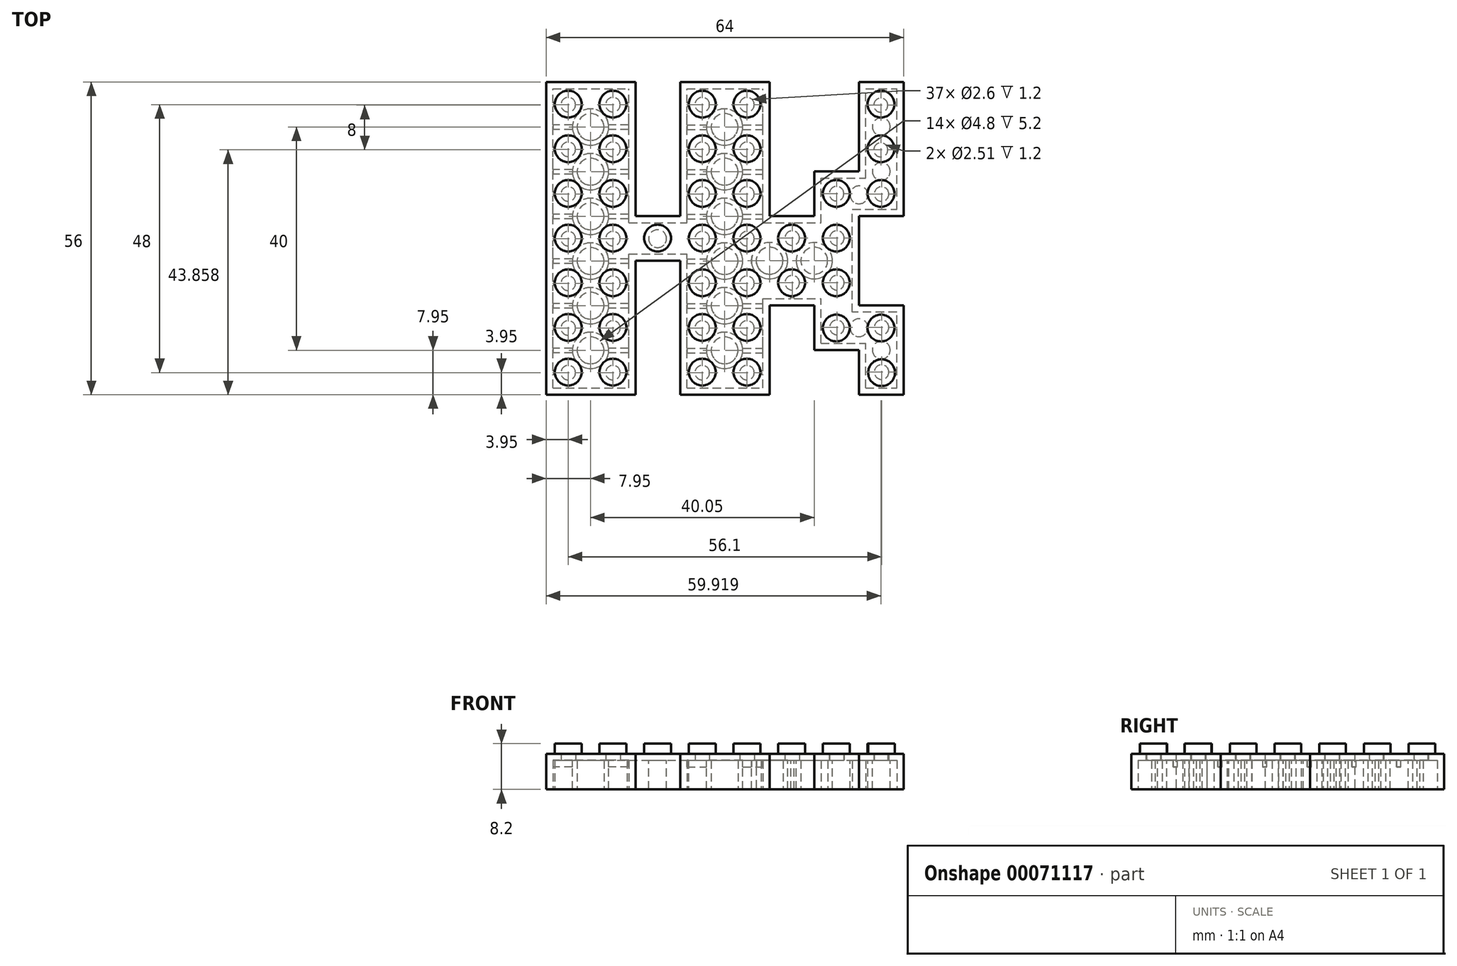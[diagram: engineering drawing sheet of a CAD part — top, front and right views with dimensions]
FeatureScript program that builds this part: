
annotation { "Feature Type Name" : "Feature", "Feature Type Description" : "" }
export const myFeature = defineFeature(function(context is Context, id is Id, definition is map)
    precondition{}
    {
        {
            var Q0;
            Q0=qCreatedBy(makeId("Top.planeOp"),FACE);
            var sketch = newSketch(context, id + "F0", { "sketchPlane" : qUnion([Q0])});
            skLineSegment(sketch, "E0.rect.bottom", {"start": v(20, 28) * mm, "end": v(-20, 28) * mm});
            skLineSegment(sketch, "E0.rect.top", {"start": v(20, -28) * mm, "end": v(-20, -28) * mm});
            skLineSegment(sketch, "E0.rect.left", {"start": v(20, 28) * mm, "end": v(20, -28) * mm});
            skLineSegment(sketch, "E0.rect.right", {"start": v(-20, 28) * mm, "end": v(-20, -28) * mm});
            skPoint(sketch, "E0.rect.middle", {"position": v(0, 0) * mm});
            skSolve(sketch);
        }
        {
            var Q0;
            Q0=makeQuery(id+"F0.imprint","IMPRINT",FACE,{"disambiguationData":[TD([[makeQuery(id+"F0.imprint","IMPRINT",EDGE,{"derivedFrom":sQuery(id+"F0.wireOp",EDGE,"E0.rect.bottom")}),1.0]])]});
            extrude(context, id + "F1", {"entities" : qUnion([Q0]), "depth" : 6.4 * mm});
        }
        {
            var Q0;
            Q0=makeQuery(id+"F1.opExtrude","CAP_FACE",FACE,{"disambiguationData":[OSD([sQuery(id+"F0.wireOp",EDGE,"E0.rect.bottom"),sQuery(id+"F0.wireOp",EDGE,"E0.rect.top"),sQuery(id+"F0.wireOp",EDGE,"E0.rect.left"),sQuery(id+"F0.wireOp",EDGE,"E0.rect.right")])],"isStart":false});
            var sketch = newSketch(context, id + "F2", { "sketchPlane" : qUnion([Q0])});
            skLineSegment(sketch, "E1.bottom", {"start": v(4, 4) * mm, "end": v(-4, 4) * mm});
            skLineSegment(sketch, "E1.top", {"start": v(4, 28) * mm, "end": v(-4, 28) * mm});
            skLineSegment(sketch, "E1.left", {"start": v(4, 4) * mm, "end": v(4, 28) * mm});
            skLineSegment(sketch, "E1.right", {"start": v(-4, 4) * mm, "end": v(-4, 28) * mm});
            skSolve(sketch);
        }
        {
            var Q0;
            Q0=makeQuery(id+"F2.imprint","IMPRINT",FACE,{"disambiguationData":[TD([[makeQuery(id+"F2.imprint","IMPRINT",EDGE,{"derivedFrom":sQuery(id+"F2.wireOp",EDGE,"E1.bottom")}),-1.0]])]});
            extrude(context, id + "F3", {"entities" : qUnion([Q0]), "operationType" : NewBodyOperationType.REMOVE, "oppositeDirection" : true, "depth" : 9.6 * mm});
        }
        {
            var Q0;
            Q0=makeQuery(id+"F1.opExtrude","CAP_FACE",FACE,{"disambiguationData":[OSD([sQuery(id+"F0.wireOp",EDGE,"E0.rect.bottom"),sQuery(id+"F0.wireOp",EDGE,"E0.rect.top"),sQuery(id+"F0.wireOp",EDGE,"E0.rect.left"),sQuery(id+"F0.wireOp",EDGE,"E0.rect.right")])],"isStart":false});
            var sketch = newSketch(context, id + "F4", { "sketchPlane" : qUnion([Q0])});
            skLineSegment(sketch, "E2.bottom", {"start": v(4, -28) * mm, "end": v(-4, -28) * mm});
            skLineSegment(sketch, "E2.top", {"start": v(4, -4) * mm, "end": v(-4, -4) * mm});
            skLineSegment(sketch, "E2.left", {"start": v(4, -28) * mm, "end": v(4, -4) * mm});
            skLineSegment(sketch, "E2.right", {"start": v(-4, -28) * mm, "end": v(-4, -4) * mm});
            skSolve(sketch);
        }
        {
            var Q0;
            Q0=makeQuery(id+"F4.imprint","IMPRINT",FACE,{"disambiguationData":[TD([[makeQuery(id+"F4.imprint","IMPRINT",EDGE,{"derivedFrom":sQuery(id+"F4.wireOp",EDGE,"E2.bottom")}),-1.0]])]});
            extrude(context, id + "F5", {"entities" : qUnion([Q0]), "operationType" : NewBodyOperationType.REMOVE, "oppositeDirection" : true, "depth" : 9.6 * mm});
        }
        {
            var Q0;
            Q0=qCreatedBy(makeId("Top.planeOp"),FACE);
            var sketch = newSketch(context, id + "F6", { "sketchPlane" : qUnion([Q0])});
            skLineSegment(sketch, "E3.bottom", {"start": v(20, 4) * mm, "end": v(36, 4) * mm});
            skLineSegment(sketch, "E3.top", {"start": v(20, -12) * mm, "end": v(36, -12) * mm});
            skLineSegment(sketch, "E3.left", {"start": v(20, 4) * mm, "end": v(20, -12) * mm});
            skLineSegment(sketch, "E3.right", {"start": v(36, 4) * mm, "end": v(36, -12) * mm});
            skSolve(sketch);
        }
        {
            var Q0;
            Q0=makeQuery(id+"F6.imprint","IMPRINT",FACE,{"disambiguationData":[TD([[makeQuery(id+"F6.imprint","IMPRINT",EDGE,{"derivedFrom":sQuery(id+"F6.wireOp",EDGE,"E3.bottom")}),-1.0]])]});
            extrude(context, id + "F7", {"entities" : qUnion([Q0]), "operationType" : NewBodyOperationType.ADD, "depth" : 6.4 * mm});
        }
        {
            var Q0;
            Q0=makeQuery(id+"Fq8iTaXQzpA7FPV_1.boolean.opBoolean","MERGE",FACE,{"derivedFrom":[makeQuery(id+"FeKJCFrg74xluvg_1.boolean.opBoolean","MERGE",FACE,{"derivedFrom":[makeQuery(id+"FFEIV1BnWD0H84f_1.boolean.opBoolean","MERGE",FACE,{"derivedFrom":[makeQuery(id+"F2oVHyxGzkOQPI6_1.boolean.opBoolean","MERGE",FACE,{"derivedFrom":[makeQuery(id+"F7.boolean.opBoolean","MERGE",FACE,{"derivedFrom":[makeQuery(id+"F1.opExtrude","CAP_FACE",FACE,{"disambiguationData":[OSD([sQuery(id+"F0.wireOp",EDGE,"E0.rect.bottom"),sQuery(id+"F0.wireOp",EDGE,"E0.rect.top"),sQuery(id+"F0.wireOp",EDGE,"E0.rect.left"),sQuery(id+"F0.wireOp",EDGE,"E0.rect.right")])],"isStart":true}),makeQuery(id+"F7.opExtrude","CAP_FACE",FACE,{"disambiguationData":[OSD([sQuery(id+"F6.wireOp",EDGE,"E3.bottom"),sQuery(id+"F6.wireOp",EDGE,"E3.top"),sQuery(id+"F6.wireOp",EDGE,"E3.left"),sQuery(id+"F6.wireOp",EDGE,"E3.right")])],"isStart":true})]}),makeQuery(id+"F2oVHyxGzkOQPI6_1.opExtrude","CAP_FACE",FACE,{"disambiguationData":[OSD([sQuery(id+"Fx6wsB5A8MVDIGl_1.wireOp",EDGE,"2b883c94-4758-4cd2-bf81-8503723d2fbf.bottom"),sQuery(id+"Fx6wsB5A8MVDIGl_1.wireOp",EDGE,"2b883c94-4758-4cd2-bf81-8503723d2fbf.top"),sQuery(id+"Fx6wsB5A8MVDIGl_1.wireOp",EDGE,"2b883c94-4758-4cd2-bf81-8503723d2fbf.left"),sQuery(id+"Fx6wsB5A8MVDIGl_1.wireOp",EDGE,"2b883c94-4758-4cd2-bf81-8503723d2fbf.right")])],"isStart":true})]}),makeQuery(id+"FFEIV1BnWD0H84f_1.opExtrude","CAP_FACE",FACE,{"disambiguationData":[OSD([sQuery(id+"Fq5423x5i0oBvdk_1.wireOp",EDGE,"50359f41-1c30-4885-bf29-1e37fb7fc2df.bottom"),sQuery(id+"Fq5423x5i0oBvdk_1.wireOp",EDGE,"50359f41-1c30-4885-bf29-1e37fb7fc2df.top"),sQuery(id+"Fq5423x5i0oBvdk_1.wireOp",EDGE,"50359f41-1c30-4885-bf29-1e37fb7fc2df.left"),sQuery(id+"Fq5423x5i0oBvdk_1.wireOp",EDGE,"50359f41-1c30-4885-bf29-1e37fb7fc2df.right")])],"isStart":true})]}),makeQuery(id+"FeKJCFrg74xluvg_1.opExtrude","CAP_FACE",FACE,{"disambiguationData":[OSD([sQuery(id+"FwcK1e5tJnhP9xu_1.wireOp",EDGE,"d4659890-7073-4dbc-80d8-35276d7f4160.bottom"),sQuery(id+"FwcK1e5tJnhP9xu_1.wireOp",EDGE,"d4659890-7073-4dbc-80d8-35276d7f4160.top"),sQuery(id+"FwcK1e5tJnhP9xu_1.wireOp",EDGE,"d4659890-7073-4dbc-80d8-35276d7f4160.left"),sQuery(id+"FwcK1e5tJnhP9xu_1.wireOp",EDGE,"d4659890-7073-4dbc-80d8-35276d7f4160.right")])],"isStart":true})]}),makeQuery(id+"Fq8iTaXQzpA7FPV_1.opExtrude","CAP_FACE",FACE,{"disambiguationData":[OSD([sQuery(id+"F0iV27WPdkTHYam_1.wireOp",EDGE,"b5bfac4e-3525-4930-abdc-5fcdb06bce00.bottom"),sQuery(id+"F0iV27WPdkTHYam_1.wireOp",EDGE,"b5bfac4e-3525-4930-abdc-5fcdb06bce00.top"),sQuery(id+"F0iV27WPdkTHYam_1.wireOp",EDGE,"b5bfac4e-3525-4930-abdc-5fcdb06bce00.left"),sQuery(id+"F0iV27WPdkTHYam_1.wireOp",EDGE,"b5bfac4e-3525-4930-abdc-5fcdb06bce00.right")])],"isStart":true})]});
            var sketch = newSketch(context, id + "F8", { "sketchPlane" : qUnion([Q0])});
            skLineSegment(sketch, "E4.bottom", {"start": v(-18.8, 26.8) * mm, "end": v(-5.2, 26.8) * mm});
            skLineSegment(sketch, "E4.top", {"start": v(-18.8, -26.8) * mm, "end": v(-5.2, -26.8) * mm});
            skLineSegment(sketch, "E4.left", {"start": v(-18.8, 26.8) * mm, "end": v(-18.8, -26.8) * mm});
            skLineSegment(sketch, "E4.right", {"start": v(-5.2, 26.8) * mm, "end": v(-5.2, -26.8) * mm});
            skSolve(sketch);
        }
        {
            var Q0;
            Q0=makeQuery(id+"F8.imprint","IMPRINT",FACE,{"disambiguationData":[TD([[makeQuery(id+"F8.imprint","IMPRINT",EDGE,{"derivedFrom":sQuery(id+"F8.wireOp",EDGE,"E4.bottom")}),-1.0]])]});
            extrude(context, id + "F9", {"entities" : qUnion([Q0]), "operationType" : NewBodyOperationType.REMOVE, "oppositeDirection" : true, "depth" : 5.2 * mm});
        }
        {
            var Q0;
            Q0=makeQuery(id+"Fq8iTaXQzpA7FPV_1.boolean.opBoolean","MERGE",FACE,{"derivedFrom":[makeQuery(id+"FeKJCFrg74xluvg_1.boolean.opBoolean","MERGE",FACE,{"derivedFrom":[makeQuery(id+"FFEIV1BnWD0H84f_1.boolean.opBoolean","MERGE",FACE,{"derivedFrom":[makeQuery(id+"F2oVHyxGzkOQPI6_1.boolean.opBoolean","MERGE",FACE,{"derivedFrom":[makeQuery(id+"F7.boolean.opBoolean","MERGE",FACE,{"derivedFrom":[makeQuery(id+"F1.opExtrude","CAP_FACE",FACE,{"disambiguationData":[OSD([sQuery(id+"F0.wireOp",EDGE,"E0.rect.bottom"),sQuery(id+"F0.wireOp",EDGE,"E0.rect.top"),sQuery(id+"F0.wireOp",EDGE,"E0.rect.left"),sQuery(id+"F0.wireOp",EDGE,"E0.rect.right")])],"isStart":true}),makeQuery(id+"F7.opExtrude","CAP_FACE",FACE,{"disambiguationData":[OSD([sQuery(id+"F6.wireOp",EDGE,"E3.bottom"),sQuery(id+"F6.wireOp",EDGE,"E3.top"),sQuery(id+"F6.wireOp",EDGE,"E3.left"),sQuery(id+"F6.wireOp",EDGE,"E3.right")])],"isStart":true})]}),makeQuery(id+"F2oVHyxGzkOQPI6_1.opExtrude","CAP_FACE",FACE,{"disambiguationData":[OSD([sQuery(id+"Fx6wsB5A8MVDIGl_1.wireOp",EDGE,"2b883c94-4758-4cd2-bf81-8503723d2fbf.bottom"),sQuery(id+"Fx6wsB5A8MVDIGl_1.wireOp",EDGE,"2b883c94-4758-4cd2-bf81-8503723d2fbf.top"),sQuery(id+"Fx6wsB5A8MVDIGl_1.wireOp",EDGE,"2b883c94-4758-4cd2-bf81-8503723d2fbf.left"),sQuery(id+"Fx6wsB5A8MVDIGl_1.wireOp",EDGE,"2b883c94-4758-4cd2-bf81-8503723d2fbf.right")])],"isStart":true})]}),makeQuery(id+"FFEIV1BnWD0H84f_1.opExtrude","CAP_FACE",FACE,{"disambiguationData":[OSD([sQuery(id+"Fq5423x5i0oBvdk_1.wireOp",EDGE,"50359f41-1c30-4885-bf29-1e37fb7fc2df.bottom"),sQuery(id+"Fq5423x5i0oBvdk_1.wireOp",EDGE,"50359f41-1c30-4885-bf29-1e37fb7fc2df.top"),sQuery(id+"Fq5423x5i0oBvdk_1.wireOp",EDGE,"50359f41-1c30-4885-bf29-1e37fb7fc2df.left"),sQuery(id+"Fq5423x5i0oBvdk_1.wireOp",EDGE,"50359f41-1c30-4885-bf29-1e37fb7fc2df.right")])],"isStart":true})]}),makeQuery(id+"FeKJCFrg74xluvg_1.opExtrude","CAP_FACE",FACE,{"disambiguationData":[OSD([sQuery(id+"FwcK1e5tJnhP9xu_1.wireOp",EDGE,"d4659890-7073-4dbc-80d8-35276d7f4160.bottom"),sQuery(id+"FwcK1e5tJnhP9xu_1.wireOp",EDGE,"d4659890-7073-4dbc-80d8-35276d7f4160.top"),sQuery(id+"FwcK1e5tJnhP9xu_1.wireOp",EDGE,"d4659890-7073-4dbc-80d8-35276d7f4160.left"),sQuery(id+"FwcK1e5tJnhP9xu_1.wireOp",EDGE,"d4659890-7073-4dbc-80d8-35276d7f4160.right")])],"isStart":true})]}),makeQuery(id+"Fq8iTaXQzpA7FPV_1.opExtrude","CAP_FACE",FACE,{"disambiguationData":[OSD([sQuery(id+"F0iV27WPdkTHYam_1.wireOp",EDGE,"b5bfac4e-3525-4930-abdc-5fcdb06bce00.bottom"),sQuery(id+"F0iV27WPdkTHYam_1.wireOp",EDGE,"b5bfac4e-3525-4930-abdc-5fcdb06bce00.top"),sQuery(id+"F0iV27WPdkTHYam_1.wireOp",EDGE,"b5bfac4e-3525-4930-abdc-5fcdb06bce00.left"),sQuery(id+"F0iV27WPdkTHYam_1.wireOp",EDGE,"b5bfac4e-3525-4930-abdc-5fcdb06bce00.right")])],"isStart":true})]});
            var sketch = newSketch(context, id + "F10", { "sketchPlane" : qUnion([Q0])});
            skLineSegment(sketch, "E5.bottom", {"start": v(-5.2, 2.8) * mm, "end": v(5.2, 2.8) * mm});
            skLineSegment(sketch, "E5.top", {"start": v(-5.2, -2.8) * mm, "end": v(5.2, -2.8) * mm});
            skLineSegment(sketch, "E5.left", {"start": v(-5.2, 2.8) * mm, "end": v(-5.2, -2.8) * mm});
            skLineSegment(sketch, "E5.right", {"start": v(5.2, 2.8) * mm, "end": v(5.2, -2.8) * mm});
            skSolve(sketch);
        }
        {
            var Q0;
            Q0=makeQuery(id+"F10.imprint","IMPRINT",FACE,{"disambiguationData":[TD([[makeQuery(id+"F10.imprint","IMPRINT",EDGE,{"derivedFrom":sQuery(id+"F10.wireOp",EDGE,"E5.bottom")}),-1.0]])]});
            extrude(context, id + "F11", {"entities" : qUnion([Q0]), "operationType" : NewBodyOperationType.REMOVE, "oppositeDirection" : true, "depth" : 5.2 * mm});
        }
        {
            var Q0;
            Q0=makeQuery(id+"Fq8iTaXQzpA7FPV_1.boolean.opBoolean","MERGE",FACE,{"derivedFrom":[makeQuery(id+"FeKJCFrg74xluvg_1.boolean.opBoolean","MERGE",FACE,{"derivedFrom":[makeQuery(id+"FFEIV1BnWD0H84f_1.boolean.opBoolean","MERGE",FACE,{"derivedFrom":[makeQuery(id+"F2oVHyxGzkOQPI6_1.boolean.opBoolean","MERGE",FACE,{"derivedFrom":[makeQuery(id+"F7.boolean.opBoolean","MERGE",FACE,{"derivedFrom":[makeQuery(id+"F1.opExtrude","CAP_FACE",FACE,{"disambiguationData":[OSD([sQuery(id+"F0.wireOp",EDGE,"E0.rect.bottom"),sQuery(id+"F0.wireOp",EDGE,"E0.rect.top"),sQuery(id+"F0.wireOp",EDGE,"E0.rect.left"),sQuery(id+"F0.wireOp",EDGE,"E0.rect.right")])],"isStart":true}),makeQuery(id+"F7.opExtrude","CAP_FACE",FACE,{"disambiguationData":[OSD([sQuery(id+"F6.wireOp",EDGE,"E3.bottom"),sQuery(id+"F6.wireOp",EDGE,"E3.top"),sQuery(id+"F6.wireOp",EDGE,"E3.left"),sQuery(id+"F6.wireOp",EDGE,"E3.right")])],"isStart":true})]}),makeQuery(id+"F2oVHyxGzkOQPI6_1.opExtrude","CAP_FACE",FACE,{"disambiguationData":[OSD([sQuery(id+"Fx6wsB5A8MVDIGl_1.wireOp",EDGE,"2b883c94-4758-4cd2-bf81-8503723d2fbf.bottom"),sQuery(id+"Fx6wsB5A8MVDIGl_1.wireOp",EDGE,"2b883c94-4758-4cd2-bf81-8503723d2fbf.top"),sQuery(id+"Fx6wsB5A8MVDIGl_1.wireOp",EDGE,"2b883c94-4758-4cd2-bf81-8503723d2fbf.left"),sQuery(id+"Fx6wsB5A8MVDIGl_1.wireOp",EDGE,"2b883c94-4758-4cd2-bf81-8503723d2fbf.right")])],"isStart":true})]}),makeQuery(id+"FFEIV1BnWD0H84f_1.opExtrude","CAP_FACE",FACE,{"disambiguationData":[OSD([sQuery(id+"Fq5423x5i0oBvdk_1.wireOp",EDGE,"50359f41-1c30-4885-bf29-1e37fb7fc2df.bottom"),sQuery(id+"Fq5423x5i0oBvdk_1.wireOp",EDGE,"50359f41-1c30-4885-bf29-1e37fb7fc2df.top"),sQuery(id+"Fq5423x5i0oBvdk_1.wireOp",EDGE,"50359f41-1c30-4885-bf29-1e37fb7fc2df.left"),sQuery(id+"Fq5423x5i0oBvdk_1.wireOp",EDGE,"50359f41-1c30-4885-bf29-1e37fb7fc2df.right")])],"isStart":true})]}),makeQuery(id+"FeKJCFrg74xluvg_1.opExtrude","CAP_FACE",FACE,{"disambiguationData":[OSD([sQuery(id+"FwcK1e5tJnhP9xu_1.wireOp",EDGE,"d4659890-7073-4dbc-80d8-35276d7f4160.bottom"),sQuery(id+"FwcK1e5tJnhP9xu_1.wireOp",EDGE,"d4659890-7073-4dbc-80d8-35276d7f4160.top"),sQuery(id+"FwcK1e5tJnhP9xu_1.wireOp",EDGE,"d4659890-7073-4dbc-80d8-35276d7f4160.left"),sQuery(id+"FwcK1e5tJnhP9xu_1.wireOp",EDGE,"d4659890-7073-4dbc-80d8-35276d7f4160.right")])],"isStart":true})]}),makeQuery(id+"Fq8iTaXQzpA7FPV_1.opExtrude","CAP_FACE",FACE,{"disambiguationData":[OSD([sQuery(id+"F0iV27WPdkTHYam_1.wireOp",EDGE,"b5bfac4e-3525-4930-abdc-5fcdb06bce00.bottom"),sQuery(id+"F0iV27WPdkTHYam_1.wireOp",EDGE,"b5bfac4e-3525-4930-abdc-5fcdb06bce00.top"),sQuery(id+"F0iV27WPdkTHYam_1.wireOp",EDGE,"b5bfac4e-3525-4930-abdc-5fcdb06bce00.left"),sQuery(id+"F0iV27WPdkTHYam_1.wireOp",EDGE,"b5bfac4e-3525-4930-abdc-5fcdb06bce00.right")])],"isStart":true})]});
            var sketch = newSketch(context, id + "F12", { "sketchPlane" : qUnion([Q0])});
            skLineSegment(sketch, "E6.bottom", {"start": v(5.2, 26.8) * mm, "end": v(18.8, 26.8) * mm});
            skLineSegment(sketch, "E6.top", {"start": v(5.2, -26.8) * mm, "end": v(18.8, -26.8) * mm});
            skLineSegment(sketch, "E6.left", {"start": v(5.2, 26.8) * mm, "end": v(5.2, -26.8) * mm});
            skLineSegment(sketch, "E6.right", {"start": v(18.8, 26.8) * mm, "end": v(18.8, -26.8) * mm});
            skSolve(sketch);
        }
        {
            var Q0;
            {var subQ3=sQuery(id+"F12.wireOp",EDGE,"E6.bottom");Q0=makeQuery(id+"F12.imprint","IMPRINT",FACE,{"disambiguationData":[TD([[makeQuery(id+"F12.imprint","IMPRINT",EDGE,{"derivedFrom":subQ3}),-1.0]])]});}
            extrude(context, id + "F13", {"entities" : qUnion([Q0]), "operationType" : NewBodyOperationType.REMOVE, "oppositeDirection" : true, "depth" : 5.2 * mm});
        }
        {
            var Q0;
            Q0=makeQuery(id+"Fq8iTaXQzpA7FPV_1.boolean.opBoolean","MERGE",FACE,{"derivedFrom":[makeQuery(id+"FeKJCFrg74xluvg_1.boolean.opBoolean","MERGE",FACE,{"derivedFrom":[makeQuery(id+"FFEIV1BnWD0H84f_1.boolean.opBoolean","MERGE",FACE,{"derivedFrom":[makeQuery(id+"F2oVHyxGzkOQPI6_1.boolean.opBoolean","MERGE",FACE,{"derivedFrom":[makeQuery(id+"F7.boolean.opBoolean","MERGE",FACE,{"derivedFrom":[makeQuery(id+"F1.opExtrude","CAP_FACE",FACE,{"disambiguationData":[OSD([sQuery(id+"F0.wireOp",EDGE,"E0.rect.bottom"),sQuery(id+"F0.wireOp",EDGE,"E0.rect.top"),sQuery(id+"F0.wireOp",EDGE,"E0.rect.left"),sQuery(id+"F0.wireOp",EDGE,"E0.rect.right")])],"isStart":true}),makeQuery(id+"F7.opExtrude","CAP_FACE",FACE,{"disambiguationData":[OSD([sQuery(id+"F6.wireOp",EDGE,"E3.bottom"),sQuery(id+"F6.wireOp",EDGE,"E3.top"),sQuery(id+"F6.wireOp",EDGE,"E3.left"),sQuery(id+"F6.wireOp",EDGE,"E3.right")])],"isStart":true})]}),makeQuery(id+"F2oVHyxGzkOQPI6_1.opExtrude","CAP_FACE",FACE,{"disambiguationData":[OSD([sQuery(id+"Fx6wsB5A8MVDIGl_1.wireOp",EDGE,"2b883c94-4758-4cd2-bf81-8503723d2fbf.bottom"),sQuery(id+"Fx6wsB5A8MVDIGl_1.wireOp",EDGE,"2b883c94-4758-4cd2-bf81-8503723d2fbf.top"),sQuery(id+"Fx6wsB5A8MVDIGl_1.wireOp",EDGE,"2b883c94-4758-4cd2-bf81-8503723d2fbf.left"),sQuery(id+"Fx6wsB5A8MVDIGl_1.wireOp",EDGE,"2b883c94-4758-4cd2-bf81-8503723d2fbf.right")])],"isStart":true})]}),makeQuery(id+"FFEIV1BnWD0H84f_1.opExtrude","CAP_FACE",FACE,{"disambiguationData":[OSD([sQuery(id+"Fq5423x5i0oBvdk_1.wireOp",EDGE,"50359f41-1c30-4885-bf29-1e37fb7fc2df.bottom"),sQuery(id+"Fq5423x5i0oBvdk_1.wireOp",EDGE,"50359f41-1c30-4885-bf29-1e37fb7fc2df.top"),sQuery(id+"Fq5423x5i0oBvdk_1.wireOp",EDGE,"50359f41-1c30-4885-bf29-1e37fb7fc2df.left"),sQuery(id+"Fq5423x5i0oBvdk_1.wireOp",EDGE,"50359f41-1c30-4885-bf29-1e37fb7fc2df.right")])],"isStart":true})]}),makeQuery(id+"FeKJCFrg74xluvg_1.opExtrude","CAP_FACE",FACE,{"disambiguationData":[OSD([sQuery(id+"FwcK1e5tJnhP9xu_1.wireOp",EDGE,"d4659890-7073-4dbc-80d8-35276d7f4160.bottom"),sQuery(id+"FwcK1e5tJnhP9xu_1.wireOp",EDGE,"d4659890-7073-4dbc-80d8-35276d7f4160.top"),sQuery(id+"FwcK1e5tJnhP9xu_1.wireOp",EDGE,"d4659890-7073-4dbc-80d8-35276d7f4160.left"),sQuery(id+"FwcK1e5tJnhP9xu_1.wireOp",EDGE,"d4659890-7073-4dbc-80d8-35276d7f4160.right")])],"isStart":true})]}),makeQuery(id+"Fq8iTaXQzpA7FPV_1.opExtrude","CAP_FACE",FACE,{"disambiguationData":[OSD([sQuery(id+"F0iV27WPdkTHYam_1.wireOp",EDGE,"b5bfac4e-3525-4930-abdc-5fcdb06bce00.bottom"),sQuery(id+"F0iV27WPdkTHYam_1.wireOp",EDGE,"b5bfac4e-3525-4930-abdc-5fcdb06bce00.top"),sQuery(id+"F0iV27WPdkTHYam_1.wireOp",EDGE,"b5bfac4e-3525-4930-abdc-5fcdb06bce00.left"),sQuery(id+"F0iV27WPdkTHYam_1.wireOp",EDGE,"b5bfac4e-3525-4930-abdc-5fcdb06bce00.right")])],"isStart":true})]});
            var sketch = newSketch(context, id + "F14", { "sketchPlane" : qUnion([Q0])});
            skLineSegment(sketch, "E7.bottom", {"start": v(18.8, 10.8) * mm, "end": v(34.8, 10.8) * mm});
            skLineSegment(sketch, "E7.top", {"start": v(18.8, -2.8) * mm, "end": v(34.8, -2.8) * mm});
            skLineSegment(sketch, "E7.left", {"start": v(18.8, 10.8) * mm, "end": v(18.8, -2.8) * mm});
            skLineSegment(sketch, "E7.right", {"start": v(34.8, 10.8) * mm, "end": v(34.8, -2.8) * mm});
            skSolve(sketch);
        }
        {
            var Q0;
            Q0=makeQuery(id+"F14.imprint","IMPRINT",FACE,{"disambiguationData":[TD([[makeQuery(id+"F14.imprint","IMPRINT",EDGE,{"derivedFrom":sQuery(id+"F14.wireOp",EDGE,"E7.bottom")}),-1.0]])]});
            extrude(context, id + "F15", {"entities" : qUnion([Q0]), "operationType" : NewBodyOperationType.REMOVE, "oppositeDirection" : true, "depth" : 5.2 * mm});
        }
        {
            var Q0;
            Q0=makeQuery(id+"Fq8iTaXQzpA7FPV_1.boolean.opBoolean","MERGE",FACE,{"derivedFrom":[makeQuery(id+"FeKJCFrg74xluvg_1.boolean.opBoolean","MERGE",FACE,{"derivedFrom":[makeQuery(id+"FFEIV1BnWD0H84f_1.boolean.opBoolean","MERGE",FACE,{"derivedFrom":[makeQuery(id+"F2oVHyxGzkOQPI6_1.boolean.opBoolean","MERGE",FACE,{"derivedFrom":[makeQuery(id+"F7.boolean.opBoolean","MERGE",FACE,{"derivedFrom":[makeQuery(id+"F1.opExtrude","CAP_FACE",FACE,{"disambiguationData":[OSD([sQuery(id+"F0.wireOp",EDGE,"E0.rect.bottom"),sQuery(id+"F0.wireOp",EDGE,"E0.rect.top"),sQuery(id+"F0.wireOp",EDGE,"E0.rect.left"),sQuery(id+"F0.wireOp",EDGE,"E0.rect.right")])],"isStart":false}),makeQuery(id+"F7.opExtrude","CAP_FACE",FACE,{"disambiguationData":[OSD([sQuery(id+"F6.wireOp",EDGE,"E3.bottom"),sQuery(id+"F6.wireOp",EDGE,"E3.top"),sQuery(id+"F6.wireOp",EDGE,"E3.left"),sQuery(id+"F6.wireOp",EDGE,"E3.right")])],"isStart":false})]}),makeQuery(id+"F2oVHyxGzkOQPI6_1.opExtrude","CAP_FACE",FACE,{"disambiguationData":[OSD([sQuery(id+"Fx6wsB5A8MVDIGl_1.wireOp",EDGE,"2b883c94-4758-4cd2-bf81-8503723d2fbf.bottom"),sQuery(id+"Fx6wsB5A8MVDIGl_1.wireOp",EDGE,"2b883c94-4758-4cd2-bf81-8503723d2fbf.top"),sQuery(id+"Fx6wsB5A8MVDIGl_1.wireOp",EDGE,"2b883c94-4758-4cd2-bf81-8503723d2fbf.left"),sQuery(id+"Fx6wsB5A8MVDIGl_1.wireOp",EDGE,"2b883c94-4758-4cd2-bf81-8503723d2fbf.right")])],"isStart":false})]}),makeQuery(id+"FFEIV1BnWD0H84f_1.opExtrude","CAP_FACE",FACE,{"disambiguationData":[OSD([sQuery(id+"Fq5423x5i0oBvdk_1.wireOp",EDGE,"50359f41-1c30-4885-bf29-1e37fb7fc2df.bottom"),sQuery(id+"Fq5423x5i0oBvdk_1.wireOp",EDGE,"50359f41-1c30-4885-bf29-1e37fb7fc2df.top"),sQuery(id+"Fq5423x5i0oBvdk_1.wireOp",EDGE,"50359f41-1c30-4885-bf29-1e37fb7fc2df.left"),sQuery(id+"Fq5423x5i0oBvdk_1.wireOp",EDGE,"50359f41-1c30-4885-bf29-1e37fb7fc2df.right")])],"isStart":false})]}),makeQuery(id+"FeKJCFrg74xluvg_1.opExtrude","CAP_FACE",FACE,{"disambiguationData":[OSD([sQuery(id+"FwcK1e5tJnhP9xu_1.wireOp",EDGE,"d4659890-7073-4dbc-80d8-35276d7f4160.bottom"),sQuery(id+"FwcK1e5tJnhP9xu_1.wireOp",EDGE,"d4659890-7073-4dbc-80d8-35276d7f4160.top"),sQuery(id+"FwcK1e5tJnhP9xu_1.wireOp",EDGE,"d4659890-7073-4dbc-80d8-35276d7f4160.left"),sQuery(id+"FwcK1e5tJnhP9xu_1.wireOp",EDGE,"d4659890-7073-4dbc-80d8-35276d7f4160.right")])],"isStart":false})]}),makeQuery(id+"Fq8iTaXQzpA7FPV_1.opExtrude","CAP_FACE",FACE,{"disambiguationData":[OSD([sQuery(id+"F0iV27WPdkTHYam_1.wireOp",EDGE,"b5bfac4e-3525-4930-abdc-5fcdb06bce00.bottom"),sQuery(id+"F0iV27WPdkTHYam_1.wireOp",EDGE,"b5bfac4e-3525-4930-abdc-5fcdb06bce00.top"),sQuery(id+"F0iV27WPdkTHYam_1.wireOp",EDGE,"b5bfac4e-3525-4930-abdc-5fcdb06bce00.left"),sQuery(id+"F0iV27WPdkTHYam_1.wireOp",EDGE,"b5bfac4e-3525-4930-abdc-5fcdb06bce00.right")])],"isStart":false})]});
            var sketch = newSketch(context, id + "F16", { "sketchPlane" : qUnion([Q0])});
            skCircle(sketch, "E8", {"center": v(-16.05, 24.05) * mm, "radius": 2.4 * mm});
            skCircle(sketch, "E9.0.1.0", {"center": v(-16.05, 16.05) * mm, "radius": 2.4 * mm});
            skCircle(sketch, "E9.0.2.0", {"center": v(-16.05, 8.05) * mm, "radius": 2.4 * mm});
            skCircle(sketch, "E9.0.3.0", {"center": v(-16.05, 0.05) * mm, "radius": 2.4 * mm});
            skCircle(sketch, "E9.0.4.0", {"center": v(-16.05, -7.95) * mm, "radius": 2.4 * mm});
            skCircle(sketch, "E9.0.5.0", {"center": v(-16.05, -15.95) * mm, "radius": 2.4 * mm});
            skCircle(sketch, "E9.0.6.0", {"center": v(-16.05, -23.95) * mm, "radius": 2.4 * mm});
            skCircle(sketch, "E9.1.0.0", {"center": v(-8.05, 24.05) * mm, "radius": 2.4 * mm});
            skCircle(sketch, "E9.1.1.0", {"center": v(-8.05, 16.05) * mm, "radius": 2.4 * mm});
            skCircle(sketch, "E9.1.2.0", {"center": v(-8.05, 8.05) * mm, "radius": 2.4 * mm});
            skCircle(sketch, "E9.1.3.0", {"center": v(-8.05, 0.05) * mm, "radius": 2.4 * mm});
            skCircle(sketch, "E9.1.4.0", {"center": v(-8.05, -7.95) * mm, "radius": 2.4 * mm});
            skCircle(sketch, "E9.1.5.0", {"center": v(-8.05, -15.95) * mm, "radius": 2.4 * mm});
            skCircle(sketch, "E9.1.6.0", {"center": v(-8.05, -23.95) * mm, "radius": 2.4 * mm});
            skLineSegment(sketch, "E9.direction1", {"start": v(-16.05, 24.05) * mm, "end": v(-8.05, 24.05) * mm, "construction": true});
            skLineSegment(sketch, "E9.direction2", {"start": v(-16.05, 24.05) * mm, "end": v(-16.05, 16.05) * mm, "construction": true});
            skSolve(sketch);
        }
        {
            var Q0;
            Q0 = qSketchRegion(id + "F16", true);
            extrude(context, id + "F17", {"entities" : qUnion([Q0]), "operationType" : NewBodyOperationType.ADD, "depth" : 1.8 * mm});
        }
        {
            var Q0;
            Q0=makeQuery(id+"Fq8iTaXQzpA7FPV_1.boolean.opBoolean","MERGE",FACE,{"derivedFrom":[makeQuery(id+"FeKJCFrg74xluvg_1.boolean.opBoolean","MERGE",FACE,{"derivedFrom":[makeQuery(id+"FFEIV1BnWD0H84f_1.boolean.opBoolean","MERGE",FACE,{"derivedFrom":[makeQuery(id+"F2oVHyxGzkOQPI6_1.boolean.opBoolean","MERGE",FACE,{"derivedFrom":[makeQuery(id+"F7.boolean.opBoolean","MERGE",FACE,{"derivedFrom":[makeQuery(id+"F1.opExtrude","CAP_FACE",FACE,{"disambiguationData":[OSD([sQuery(id+"F0.wireOp",EDGE,"E0.rect.bottom"),sQuery(id+"F0.wireOp",EDGE,"E0.rect.top"),sQuery(id+"F0.wireOp",EDGE,"E0.rect.left"),sQuery(id+"F0.wireOp",EDGE,"E0.rect.right")])],"isStart":false}),makeQuery(id+"F7.opExtrude","CAP_FACE",FACE,{"disambiguationData":[OSD([sQuery(id+"F6.wireOp",EDGE,"E3.bottom"),sQuery(id+"F6.wireOp",EDGE,"E3.top"),sQuery(id+"F6.wireOp",EDGE,"E3.left"),sQuery(id+"F6.wireOp",EDGE,"E3.right")])],"isStart":false})]}),makeQuery(id+"F2oVHyxGzkOQPI6_1.opExtrude","CAP_FACE",FACE,{"disambiguationData":[OSD([sQuery(id+"Fx6wsB5A8MVDIGl_1.wireOp",EDGE,"2b883c94-4758-4cd2-bf81-8503723d2fbf.bottom"),sQuery(id+"Fx6wsB5A8MVDIGl_1.wireOp",EDGE,"2b883c94-4758-4cd2-bf81-8503723d2fbf.top"),sQuery(id+"Fx6wsB5A8MVDIGl_1.wireOp",EDGE,"2b883c94-4758-4cd2-bf81-8503723d2fbf.left"),sQuery(id+"Fx6wsB5A8MVDIGl_1.wireOp",EDGE,"2b883c94-4758-4cd2-bf81-8503723d2fbf.right")])],"isStart":false})]}),makeQuery(id+"FFEIV1BnWD0H84f_1.opExtrude","CAP_FACE",FACE,{"disambiguationData":[OSD([sQuery(id+"Fq5423x5i0oBvdk_1.wireOp",EDGE,"50359f41-1c30-4885-bf29-1e37fb7fc2df.bottom"),sQuery(id+"Fq5423x5i0oBvdk_1.wireOp",EDGE,"50359f41-1c30-4885-bf29-1e37fb7fc2df.top"),sQuery(id+"Fq5423x5i0oBvdk_1.wireOp",EDGE,"50359f41-1c30-4885-bf29-1e37fb7fc2df.left"),sQuery(id+"Fq5423x5i0oBvdk_1.wireOp",EDGE,"50359f41-1c30-4885-bf29-1e37fb7fc2df.right")])],"isStart":false})]}),makeQuery(id+"FeKJCFrg74xluvg_1.opExtrude","CAP_FACE",FACE,{"disambiguationData":[OSD([sQuery(id+"FwcK1e5tJnhP9xu_1.wireOp",EDGE,"d4659890-7073-4dbc-80d8-35276d7f4160.bottom"),sQuery(id+"FwcK1e5tJnhP9xu_1.wireOp",EDGE,"d4659890-7073-4dbc-80d8-35276d7f4160.top"),sQuery(id+"FwcK1e5tJnhP9xu_1.wireOp",EDGE,"d4659890-7073-4dbc-80d8-35276d7f4160.left"),sQuery(id+"FwcK1e5tJnhP9xu_1.wireOp",EDGE,"d4659890-7073-4dbc-80d8-35276d7f4160.right")])],"isStart":false})]}),makeQuery(id+"Fq8iTaXQzpA7FPV_1.opExtrude","CAP_FACE",FACE,{"disambiguationData":[OSD([sQuery(id+"F0iV27WPdkTHYam_1.wireOp",EDGE,"b5bfac4e-3525-4930-abdc-5fcdb06bce00.bottom"),sQuery(id+"F0iV27WPdkTHYam_1.wireOp",EDGE,"b5bfac4e-3525-4930-abdc-5fcdb06bce00.top"),sQuery(id+"F0iV27WPdkTHYam_1.wireOp",EDGE,"b5bfac4e-3525-4930-abdc-5fcdb06bce00.left"),sQuery(id+"F0iV27WPdkTHYam_1.wireOp",EDGE,"b5bfac4e-3525-4930-abdc-5fcdb06bce00.right")])],"isStart":false})]});
            var sketch = newSketch(context, id + "F18", { "sketchPlane" : qUnion([Q0])});
            skCircle(sketch, "E10", {"center": v(7.95, 24.05) * mm, "radius": 2.4 * mm});
            skCircle(sketch, "E11.0.1.0", {"center": v(7.95, 16.05) * mm, "radius": 2.4 * mm});
            skCircle(sketch, "E11.0.2.0", {"center": v(7.95, 8.05) * mm, "radius": 2.4 * mm});
            skCircle(sketch, "E11.0.3.0", {"center": v(7.95, 0.05) * mm, "radius": 2.4 * mm});
            skCircle(sketch, "E11.0.4.0", {"center": v(7.95, -7.95) * mm, "radius": 2.4 * mm});
            skCircle(sketch, "E11.0.5.0", {"center": v(7.95, -15.95) * mm, "radius": 2.4 * mm});
            skCircle(sketch, "E11.0.6.0", {"center": v(7.95, -23.95) * mm, "radius": 2.4 * mm});
            skCircle(sketch, "E11.1.0.0", {"center": v(15.95, 24.05) * mm, "radius": 2.4 * mm});
            skCircle(sketch, "E11.1.1.0", {"center": v(15.95, 16.05) * mm, "radius": 2.4 * mm});
            skCircle(sketch, "E11.1.2.0", {"center": v(15.95, 8.05) * mm, "radius": 2.4 * mm});
            skCircle(sketch, "E11.1.3.0", {"center": v(15.95, 0.05) * mm, "radius": 2.4 * mm});
            skCircle(sketch, "E11.1.4.0", {"center": v(15.95, -7.95) * mm, "radius": 2.4 * mm});
            skCircle(sketch, "E11.1.5.0", {"center": v(15.95, -15.95) * mm, "radius": 2.4 * mm});
            skCircle(sketch, "E11.1.6.0", {"center": v(15.95, -23.95) * mm, "radius": 2.4 * mm});
            skLineSegment(sketch, "E11.direction1", {"start": v(7.95, 24.05) * mm, "end": v(15.95, 24.05) * mm, "construction": true});
            skLineSegment(sketch, "E11.direction2", {"start": v(7.95, 24.05) * mm, "end": v(7.95, 16.05) * mm, "construction": true});
            skSolve(sketch);
        }
        {
            var Q0;
            Q0 = qSketchRegion(id + "F18", true);
            extrude(context, id + "F19", {"entities" : qUnion([Q0]), "operationType" : NewBodyOperationType.ADD, "depth" : 1.8 * mm});
        }
        {
            var Q0;
            Q0=makeQuery(id+"Fq8iTaXQzpA7FPV_1.boolean.opBoolean","MERGE",FACE,{"derivedFrom":[makeQuery(id+"FeKJCFrg74xluvg_1.boolean.opBoolean","MERGE",FACE,{"derivedFrom":[makeQuery(id+"FFEIV1BnWD0H84f_1.boolean.opBoolean","MERGE",FACE,{"derivedFrom":[makeQuery(id+"F2oVHyxGzkOQPI6_1.boolean.opBoolean","MERGE",FACE,{"derivedFrom":[makeQuery(id+"F7.boolean.opBoolean","MERGE",FACE,{"derivedFrom":[makeQuery(id+"F1.opExtrude","CAP_FACE",FACE,{"disambiguationData":[OSD([sQuery(id+"F0.wireOp",EDGE,"E0.rect.bottom"),sQuery(id+"F0.wireOp",EDGE,"E0.rect.top"),sQuery(id+"F0.wireOp",EDGE,"E0.rect.left"),sQuery(id+"F0.wireOp",EDGE,"E0.rect.right")])],"isStart":false}),makeQuery(id+"F7.opExtrude","CAP_FACE",FACE,{"disambiguationData":[OSD([sQuery(id+"F6.wireOp",EDGE,"E3.bottom"),sQuery(id+"F6.wireOp",EDGE,"E3.top"),sQuery(id+"F6.wireOp",EDGE,"E3.left"),sQuery(id+"F6.wireOp",EDGE,"E3.right")])],"isStart":false})]}),makeQuery(id+"F2oVHyxGzkOQPI6_1.opExtrude","CAP_FACE",FACE,{"disambiguationData":[OSD([sQuery(id+"Fx6wsB5A8MVDIGl_1.wireOp",EDGE,"2b883c94-4758-4cd2-bf81-8503723d2fbf.bottom"),sQuery(id+"Fx6wsB5A8MVDIGl_1.wireOp",EDGE,"2b883c94-4758-4cd2-bf81-8503723d2fbf.top"),sQuery(id+"Fx6wsB5A8MVDIGl_1.wireOp",EDGE,"2b883c94-4758-4cd2-bf81-8503723d2fbf.left"),sQuery(id+"Fx6wsB5A8MVDIGl_1.wireOp",EDGE,"2b883c94-4758-4cd2-bf81-8503723d2fbf.right")])],"isStart":false})]}),makeQuery(id+"FFEIV1BnWD0H84f_1.opExtrude","CAP_FACE",FACE,{"disambiguationData":[OSD([sQuery(id+"Fq5423x5i0oBvdk_1.wireOp",EDGE,"50359f41-1c30-4885-bf29-1e37fb7fc2df.bottom"),sQuery(id+"Fq5423x5i0oBvdk_1.wireOp",EDGE,"50359f41-1c30-4885-bf29-1e37fb7fc2df.top"),sQuery(id+"Fq5423x5i0oBvdk_1.wireOp",EDGE,"50359f41-1c30-4885-bf29-1e37fb7fc2df.left"),sQuery(id+"Fq5423x5i0oBvdk_1.wireOp",EDGE,"50359f41-1c30-4885-bf29-1e37fb7fc2df.right")])],"isStart":false})]}),makeQuery(id+"FeKJCFrg74xluvg_1.opExtrude","CAP_FACE",FACE,{"disambiguationData":[OSD([sQuery(id+"FwcK1e5tJnhP9xu_1.wireOp",EDGE,"d4659890-7073-4dbc-80d8-35276d7f4160.bottom"),sQuery(id+"FwcK1e5tJnhP9xu_1.wireOp",EDGE,"d4659890-7073-4dbc-80d8-35276d7f4160.top"),sQuery(id+"FwcK1e5tJnhP9xu_1.wireOp",EDGE,"d4659890-7073-4dbc-80d8-35276d7f4160.left"),sQuery(id+"FwcK1e5tJnhP9xu_1.wireOp",EDGE,"d4659890-7073-4dbc-80d8-35276d7f4160.right")])],"isStart":false})]}),makeQuery(id+"Fq8iTaXQzpA7FPV_1.opExtrude","CAP_FACE",FACE,{"disambiguationData":[OSD([sQuery(id+"F0iV27WPdkTHYam_1.wireOp",EDGE,"b5bfac4e-3525-4930-abdc-5fcdb06bce00.bottom"),sQuery(id+"F0iV27WPdkTHYam_1.wireOp",EDGE,"b5bfac4e-3525-4930-abdc-5fcdb06bce00.top"),sQuery(id+"F0iV27WPdkTHYam_1.wireOp",EDGE,"b5bfac4e-3525-4930-abdc-5fcdb06bce00.left"),sQuery(id+"F0iV27WPdkTHYam_1.wireOp",EDGE,"b5bfac4e-3525-4930-abdc-5fcdb06bce00.right")])],"isStart":false})]});
            var sketch = newSketch(context, id + "F20", { "sketchPlane" : qUnion([Q0])});
            skCircle(sketch, "E12", {"center": v(-0.05, 0.05) * mm, "radius": 2.4 * mm});
            skSolve(sketch);
        }
        {
            var Q0;
            Q0 = qSketchRegion(id + "F20", true);
            extrude(context, id + "F21", {"entities" : qUnion([Q0]), "operationType" : NewBodyOperationType.ADD, "depth" : 1.8 * mm});
        }
        {
            var Q0;
            Q0=makeQuery(id+"Fq8iTaXQzpA7FPV_1.boolean.opBoolean","MERGE",FACE,{"derivedFrom":[makeQuery(id+"FeKJCFrg74xluvg_1.boolean.opBoolean","MERGE",FACE,{"derivedFrom":[makeQuery(id+"FFEIV1BnWD0H84f_1.boolean.opBoolean","MERGE",FACE,{"derivedFrom":[makeQuery(id+"F2oVHyxGzkOQPI6_1.boolean.opBoolean","MERGE",FACE,{"derivedFrom":[makeQuery(id+"F7.boolean.opBoolean","MERGE",FACE,{"derivedFrom":[makeQuery(id+"F1.opExtrude","CAP_FACE",FACE,{"disambiguationData":[OSD([sQuery(id+"F0.wireOp",EDGE,"E0.rect.bottom"),sQuery(id+"F0.wireOp",EDGE,"E0.rect.top"),sQuery(id+"F0.wireOp",EDGE,"E0.rect.left"),sQuery(id+"F0.wireOp",EDGE,"E0.rect.right")])],"isStart":false}),makeQuery(id+"F7.opExtrude","CAP_FACE",FACE,{"disambiguationData":[OSD([sQuery(id+"F6.wireOp",EDGE,"E3.bottom"),sQuery(id+"F6.wireOp",EDGE,"E3.top"),sQuery(id+"F6.wireOp",EDGE,"E3.left"),sQuery(id+"F6.wireOp",EDGE,"E3.right")])],"isStart":false})]}),makeQuery(id+"F2oVHyxGzkOQPI6_1.opExtrude","CAP_FACE",FACE,{"disambiguationData":[OSD([sQuery(id+"Fx6wsB5A8MVDIGl_1.wireOp",EDGE,"2b883c94-4758-4cd2-bf81-8503723d2fbf.bottom"),sQuery(id+"Fx6wsB5A8MVDIGl_1.wireOp",EDGE,"2b883c94-4758-4cd2-bf81-8503723d2fbf.top"),sQuery(id+"Fx6wsB5A8MVDIGl_1.wireOp",EDGE,"2b883c94-4758-4cd2-bf81-8503723d2fbf.left"),sQuery(id+"Fx6wsB5A8MVDIGl_1.wireOp",EDGE,"2b883c94-4758-4cd2-bf81-8503723d2fbf.right")])],"isStart":false})]}),makeQuery(id+"FFEIV1BnWD0H84f_1.opExtrude","CAP_FACE",FACE,{"disambiguationData":[OSD([sQuery(id+"Fq5423x5i0oBvdk_1.wireOp",EDGE,"50359f41-1c30-4885-bf29-1e37fb7fc2df.bottom"),sQuery(id+"Fq5423x5i0oBvdk_1.wireOp",EDGE,"50359f41-1c30-4885-bf29-1e37fb7fc2df.top"),sQuery(id+"Fq5423x5i0oBvdk_1.wireOp",EDGE,"50359f41-1c30-4885-bf29-1e37fb7fc2df.left"),sQuery(id+"Fq5423x5i0oBvdk_1.wireOp",EDGE,"50359f41-1c30-4885-bf29-1e37fb7fc2df.right")])],"isStart":false})]}),makeQuery(id+"FeKJCFrg74xluvg_1.opExtrude","CAP_FACE",FACE,{"disambiguationData":[OSD([sQuery(id+"FwcK1e5tJnhP9xu_1.wireOp",EDGE,"d4659890-7073-4dbc-80d8-35276d7f4160.bottom"),sQuery(id+"FwcK1e5tJnhP9xu_1.wireOp",EDGE,"d4659890-7073-4dbc-80d8-35276d7f4160.top"),sQuery(id+"FwcK1e5tJnhP9xu_1.wireOp",EDGE,"d4659890-7073-4dbc-80d8-35276d7f4160.left"),sQuery(id+"FwcK1e5tJnhP9xu_1.wireOp",EDGE,"d4659890-7073-4dbc-80d8-35276d7f4160.right")])],"isStart":false})]}),makeQuery(id+"Fq8iTaXQzpA7FPV_1.opExtrude","CAP_FACE",FACE,{"disambiguationData":[OSD([sQuery(id+"F0iV27WPdkTHYam_1.wireOp",EDGE,"b5bfac4e-3525-4930-abdc-5fcdb06bce00.bottom"),sQuery(id+"F0iV27WPdkTHYam_1.wireOp",EDGE,"b5bfac4e-3525-4930-abdc-5fcdb06bce00.top"),sQuery(id+"F0iV27WPdkTHYam_1.wireOp",EDGE,"b5bfac4e-3525-4930-abdc-5fcdb06bce00.left"),sQuery(id+"F0iV27WPdkTHYam_1.wireOp",EDGE,"b5bfac4e-3525-4930-abdc-5fcdb06bce00.right")])],"isStart":false})]});
            var sketch = newSketch(context, id + "F22", { "sketchPlane" : qUnion([Q0])});
            skCircle(sketch, "E13", {"center": v(23.95, 0.05) * mm, "radius": 2.4 * mm});
            skCircle(sketch, "E14.0.1.0", {"center": v(23.95, -7.95) * mm, "radius": 2.4 * mm});
            skCircle(sketch, "E14.1.0.0", {"center": v(31.95, 0.05) * mm, "radius": 2.4 * mm});
            skCircle(sketch, "E14.1.1.0", {"center": v(31.95, -7.95) * mm, "radius": 2.4 * mm});
            skLineSegment(sketch, "E14.direction1", {"start": v(23.95, 0.05) * mm, "end": v(31.95, 0.05) * mm, "construction": true});
            skLineSegment(sketch, "E14.direction2", {"start": v(23.95, 0.05) * mm, "end": v(23.95, -7.95) * mm, "construction": true});
            skSolve(sketch);
        }
        {
            var Q0;
            Q0 = qSketchRegion(id + "F22", true);
            extrude(context, id + "F23", {"entities" : qUnion([Q0]), "operationType" : NewBodyOperationType.ADD, "depth" : 1.8 * mm});
        }
        {
            var Q0;
            Q0=makeQuery(id+"F70k3oBn6R9tMks_1.boolean.opBoolean","MERGE",FACE,{"derivedFrom":[makeQuery(id+"FboYl22dZ4P2C6K_1.boolean.opBoolean","MERGE",FACE,{"derivedFrom":[makeQuery(id+"Fv0jVLsngCFdKep_1.boolean.opBoolean","MERGE",FACE,{"derivedFrom":[makeQuery(id+"FTqp87gxJNhKm0U_1.boolean.opBoolean","MERGE",FACE,{"derivedFrom":[makeQuery(id+"FwQk8LqVCU26Die_1.boolean.opBoolean","MERGE",FACE,{"derivedFrom":[makeQuery(id+"FLeHIfUcP1pMywO_1.boolean.opBoolean","MERGE",FACE,{"derivedFrom":[makeQuery(id+"F15.boolean.opBoolean","MERGE",FACE,{"derivedFrom":[makeQuery(id+"F13.boolean.opBoolean","MERGE",FACE,{"derivedFrom":[makeQuery(id+"F11.boolean.opBoolean","MERGE",FACE,{"derivedFrom":[makeQuery(id+"F9.boolean.opBoolean","COPY",FACE,{"derivedFrom":makeQuery(id+"F9.opExtrude","CAP_FACE",FACE,{"disambiguationData":[OSD([sQuery(id+"F8.wireOp",EDGE,"E4.bottom"),sQuery(id+"F8.wireOp",EDGE,"E4.top"),sQuery(id+"F8.wireOp",EDGE,"E4.left"),sQuery(id+"F8.wireOp",EDGE,"E4.right")])],"isStart":false})}),makeQuery(id+"F11.opExtrude","CAP_FACE",FACE,{"disambiguationData":[OSD([sQuery(id+"F10.wireOp",EDGE,"E5.bottom"),sQuery(id+"F10.wireOp",EDGE,"E5.top"),sQuery(id+"F10.wireOp",EDGE,"E5.left"),sQuery(id+"F10.wireOp",EDGE,"E5.right")])],"isStart":false})]}),makeQuery(id+"F13.opExtrude","CAP_FACE",FACE,{"disambiguationData":[OSD([sQuery(id+"F12.wireOp",EDGE,"E6.bottom"),sQuery(id+"F12.wireOp",EDGE,"E6.top"),sQuery(id+"F12.wireOp",EDGE,"E6.left"),sQuery(id+"F12.wireOp",EDGE,"E6.right")])],"isStart":false})]}),makeQuery(id+"F15.opExtrude","CAP_FACE",FACE,{"disambiguationData":[OSD([sQuery(id+"F14.wireOp",EDGE,"E7.bottom"),sQuery(id+"F14.wireOp",EDGE,"E7.top"),sQuery(id+"F14.wireOp",EDGE,"E7.left"),sQuery(id+"F14.wireOp",EDGE,"E7.right")])],"isStart":false})]}),makeQuery(id+"FLeHIfUcP1pMywO_1.opExtrude","CAP_FACE",FACE,{"disambiguationData":[OSD([sQuery(id+"FTZ6GaKnTPrCfL5_1.wireOp",EDGE,"bcd34f6a-441e-43e3-9ce3-27bc5c12bc98.bottom"),sQuery(id+"FTZ6GaKnTPrCfL5_1.wireOp",EDGE,"bcd34f6a-441e-43e3-9ce3-27bc5c12bc98.top"),sQuery(id+"FTZ6GaKnTPrCfL5_1.wireOp",EDGE,"bcd34f6a-441e-43e3-9ce3-27bc5c12bc98.left"),sQuery(id+"FTZ6GaKnTPrCfL5_1.wireOp",EDGE,"bcd34f6a-441e-43e3-9ce3-27bc5c12bc98.right")])],"isStart":false})]}),makeQuery(id+"FwQk8LqVCU26Die_1.opExtrude","CAP_FACE",FACE,{"disambiguationData":[OSD([sQuery(id+"FgrSyFUl6aEH2ef_1.wireOp",EDGE,"54af7014-0953-4d53-a5ce-d9ebf4f7c6c1.bottom"),sQuery(id+"FgrSyFUl6aEH2ef_1.wireOp",EDGE,"54af7014-0953-4d53-a5ce-d9ebf4f7c6c1.top"),sQuery(id+"FgrSyFUl6aEH2ef_1.wireOp",EDGE,"54af7014-0953-4d53-a5ce-d9ebf4f7c6c1.left"),sQuery(id+"FgrSyFUl6aEH2ef_1.wireOp",EDGE,"54af7014-0953-4d53-a5ce-d9ebf4f7c6c1.right")])],"isStart":false})]}),makeQuery(id+"FTqp87gxJNhKm0U_1.opExtrude","CAP_FACE",FACE,{"disambiguationData":[OSD([sQuery(id+"FEsEemNcm7LhUNJ_1.wireOp",EDGE,"33d16069-cf5b-4e2e-9ee9-9ef5784b0b54.bottom"),sQuery(id+"FEsEemNcm7LhUNJ_1.wireOp",EDGE,"33d16069-cf5b-4e2e-9ee9-9ef5784b0b54.top"),sQuery(id+"FEsEemNcm7LhUNJ_1.wireOp",EDGE,"33d16069-cf5b-4e2e-9ee9-9ef5784b0b54.left"),sQuery(id+"FEsEemNcm7LhUNJ_1.wireOp",EDGE,"33d16069-cf5b-4e2e-9ee9-9ef5784b0b54.right")])],"isStart":false})]}),makeQuery(id+"Fv0jVLsngCFdKep_1.opExtrude","CAP_FACE",FACE,{"disambiguationData":[OSD([sQuery(id+"Frn2WxzwbMYrr47_1.wireOp",EDGE,"4df7dbd9-e337-4b2a-b1d6-0b3c9c44f6ce.bottom"),sQuery(id+"Frn2WxzwbMYrr47_1.wireOp",EDGE,"4df7dbd9-e337-4b2a-b1d6-0b3c9c44f6ce.top"),sQuery(id+"Frn2WxzwbMYrr47_1.wireOp",EDGE,"4df7dbd9-e337-4b2a-b1d6-0b3c9c44f6ce.left"),sQuery(id+"Frn2WxzwbMYrr47_1.wireOp",EDGE,"4df7dbd9-e337-4b2a-b1d6-0b3c9c44f6ce.right")])],"isStart":false})]}),makeQuery(id+"FboYl22dZ4P2C6K_1.opExtrude","CAP_FACE",FACE,{"disambiguationData":[OSD([sQuery(id+"F3AztrFnM7CpuWE_1.wireOp",EDGE,"699950d3-c24f-4b12-af00-4c001ecf99bb.bottom"),sQuery(id+"F3AztrFnM7CpuWE_1.wireOp",EDGE,"699950d3-c24f-4b12-af00-4c001ecf99bb.top"),sQuery(id+"F3AztrFnM7CpuWE_1.wireOp",EDGE,"699950d3-c24f-4b12-af00-4c001ecf99bb.left"),sQuery(id+"F3AztrFnM7CpuWE_1.wireOp",EDGE,"699950d3-c24f-4b12-af00-4c001ecf99bb.right")])],"isStart":false})]}),makeQuery(id+"F70k3oBn6R9tMks_1.opExtrude","CAP_FACE",FACE,{"disambiguationData":[OSD([sQuery(id+"FrefDcf4LNBQmv9_1.wireOp",EDGE,"222680ed-d087-479c-bee2-353590fc5722.bottom"),sQuery(id+"FrefDcf4LNBQmv9_1.wireOp",EDGE,"222680ed-d087-479c-bee2-353590fc5722.top"),sQuery(id+"FrefDcf4LNBQmv9_1.wireOp",EDGE,"222680ed-d087-479c-bee2-353590fc5722.left"),sQuery(id+"FrefDcf4LNBQmv9_1.wireOp",EDGE,"222680ed-d087-479c-bee2-353590fc5722.right")])],"isStart":false})]});
            var sketch = newSketch(context, id + "F24", { "sketchPlane" : qUnion([Q0])});
            skCircle(sketch, "E15", {"center": v(-16.05, 24.05) * mm, "radius": 1.3 * mm});
            skCircle(sketch, "E16.0.1.0", {"center": v(-16.05, 16.05) * mm, "radius": 1.3 * mm});
            skCircle(sketch, "E16.0.2.0", {"center": v(-16.05, 8.05) * mm, "radius": 1.3 * mm});
            skCircle(sketch, "E16.0.3.0", {"center": v(-16.05, 0.05) * mm, "radius": 1.3 * mm});
            skCircle(sketch, "E16.0.4.0", {"center": v(-16.05, -7.95) * mm, "radius": 1.3 * mm});
            skCircle(sketch, "E16.0.5.0", {"center": v(-16.05, -15.95) * mm, "radius": 1.3 * mm});
            skCircle(sketch, "E16.0.6.0", {"center": v(-16.05, -23.95) * mm, "radius": 1.3 * mm});
            skCircle(sketch, "E16.1.0.0", {"center": v(-8.05, 24.05) * mm, "radius": 1.3 * mm});
            skCircle(sketch, "E16.1.1.0", {"center": v(-8.05, 16.05) * mm, "radius": 1.3 * mm});
            skCircle(sketch, "E16.1.2.0", {"center": v(-8.05, 8.05) * mm, "radius": 1.3 * mm});
            skCircle(sketch, "E16.1.3.0", {"center": v(-8.05, 0.05) * mm, "radius": 1.3 * mm});
            skCircle(sketch, "E16.1.4.0", {"center": v(-8.05, -7.95) * mm, "radius": 1.3 * mm});
            skCircle(sketch, "E16.1.5.0", {"center": v(-8.05, -15.95) * mm, "radius": 1.3 * mm});
            skCircle(sketch, "E16.1.6.0", {"center": v(-8.05, -23.95) * mm, "radius": 1.3 * mm});
            skLineSegment(sketch, "E16.direction1", {"start": v(-16.05, 24.05) * mm, "end": v(-8.05, 24.05) * mm, "construction": true});
            skLineSegment(sketch, "E16.direction2", {"start": v(-16.05, 24.05) * mm, "end": v(-16.05, 16.05) * mm, "construction": true});
            skLineSegment(sketch, "E17", {"start": v(-8.05, 0.05) * mm, "end": v(-16.05, 8.05) * mm, "construction": true});
            skLineSegment(sketch, "E18", {"start": v(-8.05, 8.05) * mm, "end": v(-16.05, 0.05) * mm, "construction": true});
            skLineSegment(sketch, "E19", {"start": v(-8.05, 24.05) * mm, "end": v(-16.05, 16.05) * mm, "construction": true});
            skLineSegment(sketch, "E20", {"start": v(-8.05, 16.05) * mm, "end": v(-16.05, 24.05) * mm, "construction": true});
            skLineSegment(sketch, "E21", {"start": v(-8.05, -7.95) * mm, "end": v(-16.05, -15.95) * mm, "construction": true});
            skLineSegment(sketch, "E22", {"start": v(-8.05, -15.95) * mm, "end": v(-16.05, -7.95) * mm, "construction": true});
            skLineSegment(sketch, "E23", {"start": v(-8.05, 8.05) * mm, "end": v(-16.05, 16.05) * mm, "construction": true});
            skLineSegment(sketch, "E24", {"start": v(-8.05, 16.05) * mm, "end": v(-16.05, 8.05) * mm, "construction": true});
            skLineSegment(sketch, "E25", {"start": v(-8.05, 0.05) * mm, "end": v(-16.05, -7.95) * mm, "construction": true});
            skLineSegment(sketch, "E26", {"start": v(-8.05, -7.95) * mm, "end": v(-16.05, 0.05) * mm, "construction": true});
            skLineSegment(sketch, "E27", {"start": v(-8.05, -23.95) * mm, "end": v(-16.05, -15.95) * mm, "construction": true});
            skLineSegment(sketch, "E28", {"start": v(-8.05, -15.95) * mm, "end": v(-16.05, -23.95) * mm, "construction": true});
            skLineSegment(sketch, "E29", {"start": v(-16.05, 24.05) * mm, "end": v(0, 24.05) * mm, "construction": true});
            skLineSegment(sketch, "E30", {"start": v(0, 24.05) * mm, "end": v(-26.44, 24.05) * mm, "construction": true});
            skSolve(sketch);
        }
        {
            var Q0;
            Q0 = qSketchRegion(id + "F24", true);
            extrude(context, id + "F25", {"entities" : qUnion([Q0]), "operationType" : NewBodyOperationType.REMOVE, "oppositeDirection" : true, "depth" : 1.2 * mm});
        }
        {
            var Q0;
            Q0=makeQuery(id+"F70k3oBn6R9tMks_1.boolean.opBoolean","MERGE",FACE,{"derivedFrom":[makeQuery(id+"FboYl22dZ4P2C6K_1.boolean.opBoolean","MERGE",FACE,{"derivedFrom":[makeQuery(id+"Fv0jVLsngCFdKep_1.boolean.opBoolean","MERGE",FACE,{"derivedFrom":[makeQuery(id+"FTqp87gxJNhKm0U_1.boolean.opBoolean","MERGE",FACE,{"derivedFrom":[makeQuery(id+"FwQk8LqVCU26Die_1.boolean.opBoolean","MERGE",FACE,{"derivedFrom":[makeQuery(id+"FLeHIfUcP1pMywO_1.boolean.opBoolean","MERGE",FACE,{"derivedFrom":[makeQuery(id+"F15.boolean.opBoolean","MERGE",FACE,{"derivedFrom":[makeQuery(id+"F13.boolean.opBoolean","MERGE",FACE,{"derivedFrom":[makeQuery(id+"F11.boolean.opBoolean","MERGE",FACE,{"derivedFrom":[makeQuery(id+"F9.boolean.opBoolean","COPY",FACE,{"derivedFrom":makeQuery(id+"F9.opExtrude","CAP_FACE",FACE,{"disambiguationData":[OSD([sQuery(id+"F8.wireOp",EDGE,"E4.bottom"),sQuery(id+"F8.wireOp",EDGE,"E4.top"),sQuery(id+"F8.wireOp",EDGE,"E4.left"),sQuery(id+"F8.wireOp",EDGE,"E4.right")])],"isStart":false})}),makeQuery(id+"F11.opExtrude","CAP_FACE",FACE,{"disambiguationData":[OSD([sQuery(id+"F10.wireOp",EDGE,"E5.bottom"),sQuery(id+"F10.wireOp",EDGE,"E5.top"),sQuery(id+"F10.wireOp",EDGE,"E5.left"),sQuery(id+"F10.wireOp",EDGE,"E5.right")])],"isStart":false})]}),makeQuery(id+"F13.opExtrude","CAP_FACE",FACE,{"disambiguationData":[OSD([sQuery(id+"F12.wireOp",EDGE,"E6.bottom"),sQuery(id+"F12.wireOp",EDGE,"E6.top"),sQuery(id+"F12.wireOp",EDGE,"E6.left"),sQuery(id+"F12.wireOp",EDGE,"E6.right")])],"isStart":false})]}),makeQuery(id+"F15.opExtrude","CAP_FACE",FACE,{"disambiguationData":[OSD([sQuery(id+"F14.wireOp",EDGE,"E7.bottom"),sQuery(id+"F14.wireOp",EDGE,"E7.top"),sQuery(id+"F14.wireOp",EDGE,"E7.left"),sQuery(id+"F14.wireOp",EDGE,"E7.right")])],"isStart":false})]}),makeQuery(id+"FLeHIfUcP1pMywO_1.opExtrude","CAP_FACE",FACE,{"disambiguationData":[OSD([sQuery(id+"FTZ6GaKnTPrCfL5_1.wireOp",EDGE,"bcd34f6a-441e-43e3-9ce3-27bc5c12bc98.bottom"),sQuery(id+"FTZ6GaKnTPrCfL5_1.wireOp",EDGE,"bcd34f6a-441e-43e3-9ce3-27bc5c12bc98.top"),sQuery(id+"FTZ6GaKnTPrCfL5_1.wireOp",EDGE,"bcd34f6a-441e-43e3-9ce3-27bc5c12bc98.left"),sQuery(id+"FTZ6GaKnTPrCfL5_1.wireOp",EDGE,"bcd34f6a-441e-43e3-9ce3-27bc5c12bc98.right")])],"isStart":false})]}),makeQuery(id+"FwQk8LqVCU26Die_1.opExtrude","CAP_FACE",FACE,{"disambiguationData":[OSD([sQuery(id+"FgrSyFUl6aEH2ef_1.wireOp",EDGE,"54af7014-0953-4d53-a5ce-d9ebf4f7c6c1.bottom"),sQuery(id+"FgrSyFUl6aEH2ef_1.wireOp",EDGE,"54af7014-0953-4d53-a5ce-d9ebf4f7c6c1.top"),sQuery(id+"FgrSyFUl6aEH2ef_1.wireOp",EDGE,"54af7014-0953-4d53-a5ce-d9ebf4f7c6c1.left"),sQuery(id+"FgrSyFUl6aEH2ef_1.wireOp",EDGE,"54af7014-0953-4d53-a5ce-d9ebf4f7c6c1.right")])],"isStart":false})]}),makeQuery(id+"FTqp87gxJNhKm0U_1.opExtrude","CAP_FACE",FACE,{"disambiguationData":[OSD([sQuery(id+"FEsEemNcm7LhUNJ_1.wireOp",EDGE,"33d16069-cf5b-4e2e-9ee9-9ef5784b0b54.bottom"),sQuery(id+"FEsEemNcm7LhUNJ_1.wireOp",EDGE,"33d16069-cf5b-4e2e-9ee9-9ef5784b0b54.top"),sQuery(id+"FEsEemNcm7LhUNJ_1.wireOp",EDGE,"33d16069-cf5b-4e2e-9ee9-9ef5784b0b54.left"),sQuery(id+"FEsEemNcm7LhUNJ_1.wireOp",EDGE,"33d16069-cf5b-4e2e-9ee9-9ef5784b0b54.right")])],"isStart":false})]}),makeQuery(id+"Fv0jVLsngCFdKep_1.opExtrude","CAP_FACE",FACE,{"disambiguationData":[OSD([sQuery(id+"Frn2WxzwbMYrr47_1.wireOp",EDGE,"4df7dbd9-e337-4b2a-b1d6-0b3c9c44f6ce.bottom"),sQuery(id+"Frn2WxzwbMYrr47_1.wireOp",EDGE,"4df7dbd9-e337-4b2a-b1d6-0b3c9c44f6ce.top"),sQuery(id+"Frn2WxzwbMYrr47_1.wireOp",EDGE,"4df7dbd9-e337-4b2a-b1d6-0b3c9c44f6ce.left"),sQuery(id+"Frn2WxzwbMYrr47_1.wireOp",EDGE,"4df7dbd9-e337-4b2a-b1d6-0b3c9c44f6ce.right")])],"isStart":false})]}),makeQuery(id+"FboYl22dZ4P2C6K_1.opExtrude","CAP_FACE",FACE,{"disambiguationData":[OSD([sQuery(id+"F3AztrFnM7CpuWE_1.wireOp",EDGE,"699950d3-c24f-4b12-af00-4c001ecf99bb.bottom"),sQuery(id+"F3AztrFnM7CpuWE_1.wireOp",EDGE,"699950d3-c24f-4b12-af00-4c001ecf99bb.top"),sQuery(id+"F3AztrFnM7CpuWE_1.wireOp",EDGE,"699950d3-c24f-4b12-af00-4c001ecf99bb.left"),sQuery(id+"F3AztrFnM7CpuWE_1.wireOp",EDGE,"699950d3-c24f-4b12-af00-4c001ecf99bb.right")])],"isStart":false})]}),makeQuery(id+"F70k3oBn6R9tMks_1.opExtrude","CAP_FACE",FACE,{"disambiguationData":[OSD([sQuery(id+"FrefDcf4LNBQmv9_1.wireOp",EDGE,"222680ed-d087-479c-bee2-353590fc5722.bottom"),sQuery(id+"FrefDcf4LNBQmv9_1.wireOp",EDGE,"222680ed-d087-479c-bee2-353590fc5722.top"),sQuery(id+"FrefDcf4LNBQmv9_1.wireOp",EDGE,"222680ed-d087-479c-bee2-353590fc5722.left"),sQuery(id+"FrefDcf4LNBQmv9_1.wireOp",EDGE,"222680ed-d087-479c-bee2-353590fc5722.right")])],"isStart":false})]});
            var sketch = newSketch(context, id + "F26", { "sketchPlane" : qUnion([Q0])});
            skCircle(sketch, "E31", {"center": v(7.95, 24.05) * mm, "radius": 1.3 * mm});
            skCircle(sketch, "E32.0.1.0", {"center": v(7.95, 16.05) * mm, "radius": 1.3 * mm});
            skCircle(sketch, "E32.0.2.0", {"center": v(7.95, 8.05) * mm, "radius": 1.3 * mm});
            skCircle(sketch, "E32.0.3.0", {"center": v(7.95, 0.05) * mm, "radius": 1.3 * mm});
            skCircle(sketch, "E32.0.4.0", {"center": v(7.95, -7.95) * mm, "radius": 1.3 * mm});
            skCircle(sketch, "E32.0.5.0", {"center": v(7.95, -15.95) * mm, "radius": 1.3 * mm});
            skCircle(sketch, "E32.0.6.0", {"center": v(7.95, -23.95) * mm, "radius": 1.3 * mm});
            skCircle(sketch, "E32.1.0.0", {"center": v(15.95, 24.05) * mm, "radius": 1.3 * mm});
            skCircle(sketch, "E32.1.1.0", {"center": v(15.95, 16.05) * mm, "radius": 1.3 * mm});
            skCircle(sketch, "E32.1.2.0", {"center": v(15.95, 8.05) * mm, "radius": 1.3 * mm});
            skCircle(sketch, "E32.1.3.0", {"center": v(15.95, 0.05) * mm, "radius": 1.3 * mm});
            skCircle(sketch, "E32.1.4.0", {"center": v(15.95, -7.95) * mm, "radius": 1.3 * mm});
            skCircle(sketch, "E32.1.5.0", {"center": v(15.95, -15.95) * mm, "radius": 1.3 * mm});
            skCircle(sketch, "E32.1.6.0", {"center": v(15.95, -23.95) * mm, "radius": 1.3 * mm});
            skLineSegment(sketch, "E32.direction1", {"start": v(7.95, 24.05) * mm, "end": v(15.95, 24.05) * mm, "construction": true});
            skLineSegment(sketch, "E32.direction2", {"start": v(7.95, 24.05) * mm, "end": v(7.95, 16.05) * mm, "construction": true});
            skLineSegment(sketch, "E33", {"start": v(15.95, 16.05) * mm, "end": v(7.95, 24.05) * mm, "construction": true});
            skLineSegment(sketch, "E34", {"start": v(15.95, 24.05) * mm, "end": v(7.95, 16.05) * mm, "construction": true});
            skLineSegment(sketch, "E35", {"start": v(15.95, 8.05) * mm, "end": v(7.95, 16.05) * mm, "construction": true});
            skLineSegment(sketch, "E36", {"start": v(15.95, 16.05) * mm, "end": v(7.95, 8.05) * mm, "construction": true});
            skLineSegment(sketch, "E37", {"start": v(15.95, 0.05) * mm, "end": v(7.95, 8.05) * mm, "construction": true});
            skLineSegment(sketch, "E38", {"start": v(15.95, 0.05) * mm, "end": v(7.95, -7.95) * mm, "construction": true});
            skLineSegment(sketch, "E39", {"start": v(15.95, -15.95) * mm, "end": v(7.95, -7.95) * mm, "construction": true});
            skLineSegment(sketch, "E40", {"start": v(15.95, -15.95) * mm, "end": v(7.95, -23.95) * mm, "construction": true});
            skLineSegment(sketch, "E41", {"start": v(15.95, -23.95) * mm, "end": v(7.95, -15.95) * mm, "construction": true});
            skLineSegment(sketch, "E42", {"start": v(15.95, -7.95) * mm, "end": v(7.95, -15.95) * mm, "construction": true});
            skLineSegment(sketch, "E43", {"start": v(15.95, -7.95) * mm, "end": v(7.95, 0.05) * mm, "construction": true});
            skLineSegment(sketch, "E44", {"start": v(15.95, 8.05) * mm, "end": v(7.95, 0.05) * mm, "construction": true});
            skLineSegment(sketch, "E45", {"start": v(7.95, 24.05) * mm, "end": v(25.23, 24.05) * mm, "construction": true});
            skLineSegment(sketch, "E46", {"start": v(25.23, 24.05) * mm, "end": v(0.85, 24.05) * mm, "construction": true});
            skSolve(sketch);
        }
        {
            var Q0;
            Q0 = qSketchRegion(id + "F26", true);
            extrude(context, id + "F27", {"entities" : qUnion([Q0]), "operationType" : NewBodyOperationType.REMOVE, "oppositeDirection" : true, "depth" : 1.2 * mm});
        }
        {
            var Q0;
            Q0=makeQuery(id+"F70k3oBn6R9tMks_1.boolean.opBoolean","MERGE",FACE,{"derivedFrom":[makeQuery(id+"FboYl22dZ4P2C6K_1.boolean.opBoolean","MERGE",FACE,{"derivedFrom":[makeQuery(id+"Fv0jVLsngCFdKep_1.boolean.opBoolean","MERGE",FACE,{"derivedFrom":[makeQuery(id+"FTqp87gxJNhKm0U_1.boolean.opBoolean","MERGE",FACE,{"derivedFrom":[makeQuery(id+"FwQk8LqVCU26Die_1.boolean.opBoolean","MERGE",FACE,{"derivedFrom":[makeQuery(id+"FLeHIfUcP1pMywO_1.boolean.opBoolean","MERGE",FACE,{"derivedFrom":[makeQuery(id+"F15.boolean.opBoolean","MERGE",FACE,{"derivedFrom":[makeQuery(id+"F13.boolean.opBoolean","MERGE",FACE,{"derivedFrom":[makeQuery(id+"F11.boolean.opBoolean","MERGE",FACE,{"derivedFrom":[makeQuery(id+"F9.boolean.opBoolean","COPY",FACE,{"derivedFrom":makeQuery(id+"F9.opExtrude","CAP_FACE",FACE,{"disambiguationData":[OSD([sQuery(id+"F8.wireOp",EDGE,"E4.bottom"),sQuery(id+"F8.wireOp",EDGE,"E4.top"),sQuery(id+"F8.wireOp",EDGE,"E4.left"),sQuery(id+"F8.wireOp",EDGE,"E4.right")])],"isStart":false})}),makeQuery(id+"F11.opExtrude","CAP_FACE",FACE,{"disambiguationData":[OSD([sQuery(id+"F10.wireOp",EDGE,"E5.bottom"),sQuery(id+"F10.wireOp",EDGE,"E5.top"),sQuery(id+"F10.wireOp",EDGE,"E5.left"),sQuery(id+"F10.wireOp",EDGE,"E5.right")])],"isStart":false})]}),makeQuery(id+"F13.opExtrude","CAP_FACE",FACE,{"disambiguationData":[OSD([sQuery(id+"F12.wireOp",EDGE,"E6.bottom"),sQuery(id+"F12.wireOp",EDGE,"E6.top"),sQuery(id+"F12.wireOp",EDGE,"E6.left"),sQuery(id+"F12.wireOp",EDGE,"E6.right")])],"isStart":false})]}),makeQuery(id+"F15.opExtrude","CAP_FACE",FACE,{"disambiguationData":[OSD([sQuery(id+"F14.wireOp",EDGE,"E7.bottom"),sQuery(id+"F14.wireOp",EDGE,"E7.top"),sQuery(id+"F14.wireOp",EDGE,"E7.left"),sQuery(id+"F14.wireOp",EDGE,"E7.right")])],"isStart":false})]}),makeQuery(id+"FLeHIfUcP1pMywO_1.opExtrude","CAP_FACE",FACE,{"disambiguationData":[OSD([sQuery(id+"FTZ6GaKnTPrCfL5_1.wireOp",EDGE,"bcd34f6a-441e-43e3-9ce3-27bc5c12bc98.bottom"),sQuery(id+"FTZ6GaKnTPrCfL5_1.wireOp",EDGE,"bcd34f6a-441e-43e3-9ce3-27bc5c12bc98.top"),sQuery(id+"FTZ6GaKnTPrCfL5_1.wireOp",EDGE,"bcd34f6a-441e-43e3-9ce3-27bc5c12bc98.left"),sQuery(id+"FTZ6GaKnTPrCfL5_1.wireOp",EDGE,"bcd34f6a-441e-43e3-9ce3-27bc5c12bc98.right")])],"isStart":false})]}),makeQuery(id+"FwQk8LqVCU26Die_1.opExtrude","CAP_FACE",FACE,{"disambiguationData":[OSD([sQuery(id+"FgrSyFUl6aEH2ef_1.wireOp",EDGE,"54af7014-0953-4d53-a5ce-d9ebf4f7c6c1.bottom"),sQuery(id+"FgrSyFUl6aEH2ef_1.wireOp",EDGE,"54af7014-0953-4d53-a5ce-d9ebf4f7c6c1.top"),sQuery(id+"FgrSyFUl6aEH2ef_1.wireOp",EDGE,"54af7014-0953-4d53-a5ce-d9ebf4f7c6c1.left"),sQuery(id+"FgrSyFUl6aEH2ef_1.wireOp",EDGE,"54af7014-0953-4d53-a5ce-d9ebf4f7c6c1.right")])],"isStart":false})]}),makeQuery(id+"FTqp87gxJNhKm0U_1.opExtrude","CAP_FACE",FACE,{"disambiguationData":[OSD([sQuery(id+"FEsEemNcm7LhUNJ_1.wireOp",EDGE,"33d16069-cf5b-4e2e-9ee9-9ef5784b0b54.bottom"),sQuery(id+"FEsEemNcm7LhUNJ_1.wireOp",EDGE,"33d16069-cf5b-4e2e-9ee9-9ef5784b0b54.top"),sQuery(id+"FEsEemNcm7LhUNJ_1.wireOp",EDGE,"33d16069-cf5b-4e2e-9ee9-9ef5784b0b54.left"),sQuery(id+"FEsEemNcm7LhUNJ_1.wireOp",EDGE,"33d16069-cf5b-4e2e-9ee9-9ef5784b0b54.right")])],"isStart":false})]}),makeQuery(id+"Fv0jVLsngCFdKep_1.opExtrude","CAP_FACE",FACE,{"disambiguationData":[OSD([sQuery(id+"Frn2WxzwbMYrr47_1.wireOp",EDGE,"4df7dbd9-e337-4b2a-b1d6-0b3c9c44f6ce.bottom"),sQuery(id+"Frn2WxzwbMYrr47_1.wireOp",EDGE,"4df7dbd9-e337-4b2a-b1d6-0b3c9c44f6ce.top"),sQuery(id+"Frn2WxzwbMYrr47_1.wireOp",EDGE,"4df7dbd9-e337-4b2a-b1d6-0b3c9c44f6ce.left"),sQuery(id+"Frn2WxzwbMYrr47_1.wireOp",EDGE,"4df7dbd9-e337-4b2a-b1d6-0b3c9c44f6ce.right")])],"isStart":false})]}),makeQuery(id+"FboYl22dZ4P2C6K_1.opExtrude","CAP_FACE",FACE,{"disambiguationData":[OSD([sQuery(id+"F3AztrFnM7CpuWE_1.wireOp",EDGE,"699950d3-c24f-4b12-af00-4c001ecf99bb.bottom"),sQuery(id+"F3AztrFnM7CpuWE_1.wireOp",EDGE,"699950d3-c24f-4b12-af00-4c001ecf99bb.top"),sQuery(id+"F3AztrFnM7CpuWE_1.wireOp",EDGE,"699950d3-c24f-4b12-af00-4c001ecf99bb.left"),sQuery(id+"F3AztrFnM7CpuWE_1.wireOp",EDGE,"699950d3-c24f-4b12-af00-4c001ecf99bb.right")])],"isStart":false})]}),makeQuery(id+"F70k3oBn6R9tMks_1.opExtrude","CAP_FACE",FACE,{"disambiguationData":[OSD([sQuery(id+"FrefDcf4LNBQmv9_1.wireOp",EDGE,"222680ed-d087-479c-bee2-353590fc5722.bottom"),sQuery(id+"FrefDcf4LNBQmv9_1.wireOp",EDGE,"222680ed-d087-479c-bee2-353590fc5722.top"),sQuery(id+"FrefDcf4LNBQmv9_1.wireOp",EDGE,"222680ed-d087-479c-bee2-353590fc5722.left"),sQuery(id+"FrefDcf4LNBQmv9_1.wireOp",EDGE,"222680ed-d087-479c-bee2-353590fc5722.right")])],"isStart":false})]});
            var sketch = newSketch(context, id + "F28", { "sketchPlane" : qUnion([Q0])});
            skCircle(sketch, "E47", {"center": v(-0.05, 0.05) * mm, "radius": 1.6 * mm});
            skSolve(sketch);
        }
        {
            var Q0;
            Q0 = qSketchRegion(id + "F28", true);
            var Q1;
            Q1=makeQuery(id+"F7.boolean.opBoolean","MERGE",FACE,{"derivedFrom":[makeQuery(id+"F1.opExtrude","CAP_FACE",FACE,{"disambiguationData":[OSD([sQuery(id+"F0.wireOp",EDGE,"E0.rect.bottom"),sQuery(id+"F0.wireOp",EDGE,"E0.rect.top"),sQuery(id+"F0.wireOp",EDGE,"E0.rect.left"),sQuery(id+"F0.wireOp",EDGE,"E0.rect.right")])],"isStart":true}),makeQuery(id+"F7.opExtrude","CAP_FACE",FACE,{"disambiguationData":[OSD([sQuery(id+"F6.wireOp",EDGE,"E3.bottom"),sQuery(id+"F6.wireOp",EDGE,"E3.top"),sQuery(id+"F6.wireOp",EDGE,"E3.left"),sQuery(id+"F6.wireOp",EDGE,"E3.right")])],"isStart":true})]});
            extrude(context, id + "F29", {"entities" : qUnion([Q0]), "operationType" : NewBodyOperationType.ADD, "endBound" : BoundingType.UP_TO_SURFACE, "endBoundEntityFace" : qUnion([Q1]), "depth" : 1.2 * mm});
        }
        {
            var Q0;
            Q0=makeQuery(id+"F70k3oBn6R9tMks_1.boolean.opBoolean","MERGE",FACE,{"derivedFrom":[makeQuery(id+"FboYl22dZ4P2C6K_1.boolean.opBoolean","MERGE",FACE,{"derivedFrom":[makeQuery(id+"Fv0jVLsngCFdKep_1.boolean.opBoolean","MERGE",FACE,{"derivedFrom":[makeQuery(id+"FTqp87gxJNhKm0U_1.boolean.opBoolean","MERGE",FACE,{"derivedFrom":[makeQuery(id+"FwQk8LqVCU26Die_1.boolean.opBoolean","MERGE",FACE,{"derivedFrom":[makeQuery(id+"FLeHIfUcP1pMywO_1.boolean.opBoolean","MERGE",FACE,{"derivedFrom":[makeQuery(id+"F15.boolean.opBoolean","MERGE",FACE,{"derivedFrom":[makeQuery(id+"F13.boolean.opBoolean","MERGE",FACE,{"derivedFrom":[makeQuery(id+"F11.boolean.opBoolean","MERGE",FACE,{"derivedFrom":[makeQuery(id+"F9.boolean.opBoolean","COPY",FACE,{"derivedFrom":makeQuery(id+"F9.opExtrude","CAP_FACE",FACE,{"disambiguationData":[OSD([sQuery(id+"F8.wireOp",EDGE,"E4.bottom"),sQuery(id+"F8.wireOp",EDGE,"E4.top"),sQuery(id+"F8.wireOp",EDGE,"E4.left"),sQuery(id+"F8.wireOp",EDGE,"E4.right")])],"isStart":false})}),makeQuery(id+"F11.opExtrude","CAP_FACE",FACE,{"disambiguationData":[OSD([sQuery(id+"F10.wireOp",EDGE,"E5.bottom"),sQuery(id+"F10.wireOp",EDGE,"E5.top"),sQuery(id+"F10.wireOp",EDGE,"E5.left"),sQuery(id+"F10.wireOp",EDGE,"E5.right")])],"isStart":false})]}),makeQuery(id+"F13.opExtrude","CAP_FACE",FACE,{"disambiguationData":[OSD([sQuery(id+"F12.wireOp",EDGE,"E6.bottom"),sQuery(id+"F12.wireOp",EDGE,"E6.top"),sQuery(id+"F12.wireOp",EDGE,"E6.left"),sQuery(id+"F12.wireOp",EDGE,"E6.right")])],"isStart":false})]}),makeQuery(id+"F15.opExtrude","CAP_FACE",FACE,{"disambiguationData":[OSD([sQuery(id+"F14.wireOp",EDGE,"E7.bottom"),sQuery(id+"F14.wireOp",EDGE,"E7.top"),sQuery(id+"F14.wireOp",EDGE,"E7.left"),sQuery(id+"F14.wireOp",EDGE,"E7.right")])],"isStart":false})]}),makeQuery(id+"FLeHIfUcP1pMywO_1.opExtrude","CAP_FACE",FACE,{"disambiguationData":[OSD([sQuery(id+"FTZ6GaKnTPrCfL5_1.wireOp",EDGE,"bcd34f6a-441e-43e3-9ce3-27bc5c12bc98.bottom"),sQuery(id+"FTZ6GaKnTPrCfL5_1.wireOp",EDGE,"bcd34f6a-441e-43e3-9ce3-27bc5c12bc98.top"),sQuery(id+"FTZ6GaKnTPrCfL5_1.wireOp",EDGE,"bcd34f6a-441e-43e3-9ce3-27bc5c12bc98.left"),sQuery(id+"FTZ6GaKnTPrCfL5_1.wireOp",EDGE,"bcd34f6a-441e-43e3-9ce3-27bc5c12bc98.right")])],"isStart":false})]}),makeQuery(id+"FwQk8LqVCU26Die_1.opExtrude","CAP_FACE",FACE,{"disambiguationData":[OSD([sQuery(id+"FgrSyFUl6aEH2ef_1.wireOp",EDGE,"54af7014-0953-4d53-a5ce-d9ebf4f7c6c1.bottom"),sQuery(id+"FgrSyFUl6aEH2ef_1.wireOp",EDGE,"54af7014-0953-4d53-a5ce-d9ebf4f7c6c1.top"),sQuery(id+"FgrSyFUl6aEH2ef_1.wireOp",EDGE,"54af7014-0953-4d53-a5ce-d9ebf4f7c6c1.left"),sQuery(id+"FgrSyFUl6aEH2ef_1.wireOp",EDGE,"54af7014-0953-4d53-a5ce-d9ebf4f7c6c1.right")])],"isStart":false})]}),makeQuery(id+"FTqp87gxJNhKm0U_1.opExtrude","CAP_FACE",FACE,{"disambiguationData":[OSD([sQuery(id+"FEsEemNcm7LhUNJ_1.wireOp",EDGE,"33d16069-cf5b-4e2e-9ee9-9ef5784b0b54.bottom"),sQuery(id+"FEsEemNcm7LhUNJ_1.wireOp",EDGE,"33d16069-cf5b-4e2e-9ee9-9ef5784b0b54.top"),sQuery(id+"FEsEemNcm7LhUNJ_1.wireOp",EDGE,"33d16069-cf5b-4e2e-9ee9-9ef5784b0b54.left"),sQuery(id+"FEsEemNcm7LhUNJ_1.wireOp",EDGE,"33d16069-cf5b-4e2e-9ee9-9ef5784b0b54.right")])],"isStart":false})]}),makeQuery(id+"Fv0jVLsngCFdKep_1.opExtrude","CAP_FACE",FACE,{"disambiguationData":[OSD([sQuery(id+"Frn2WxzwbMYrr47_1.wireOp",EDGE,"4df7dbd9-e337-4b2a-b1d6-0b3c9c44f6ce.bottom"),sQuery(id+"Frn2WxzwbMYrr47_1.wireOp",EDGE,"4df7dbd9-e337-4b2a-b1d6-0b3c9c44f6ce.top"),sQuery(id+"Frn2WxzwbMYrr47_1.wireOp",EDGE,"4df7dbd9-e337-4b2a-b1d6-0b3c9c44f6ce.left"),sQuery(id+"Frn2WxzwbMYrr47_1.wireOp",EDGE,"4df7dbd9-e337-4b2a-b1d6-0b3c9c44f6ce.right")])],"isStart":false})]}),makeQuery(id+"FboYl22dZ4P2C6K_1.opExtrude","CAP_FACE",FACE,{"disambiguationData":[OSD([sQuery(id+"F3AztrFnM7CpuWE_1.wireOp",EDGE,"699950d3-c24f-4b12-af00-4c001ecf99bb.bottom"),sQuery(id+"F3AztrFnM7CpuWE_1.wireOp",EDGE,"699950d3-c24f-4b12-af00-4c001ecf99bb.top"),sQuery(id+"F3AztrFnM7CpuWE_1.wireOp",EDGE,"699950d3-c24f-4b12-af00-4c001ecf99bb.left"),sQuery(id+"F3AztrFnM7CpuWE_1.wireOp",EDGE,"699950d3-c24f-4b12-af00-4c001ecf99bb.right")])],"isStart":false})]}),makeQuery(id+"F70k3oBn6R9tMks_1.opExtrude","CAP_FACE",FACE,{"disambiguationData":[OSD([sQuery(id+"FrefDcf4LNBQmv9_1.wireOp",EDGE,"222680ed-d087-479c-bee2-353590fc5722.bottom"),sQuery(id+"FrefDcf4LNBQmv9_1.wireOp",EDGE,"222680ed-d087-479c-bee2-353590fc5722.top"),sQuery(id+"FrefDcf4LNBQmv9_1.wireOp",EDGE,"222680ed-d087-479c-bee2-353590fc5722.left"),sQuery(id+"FrefDcf4LNBQmv9_1.wireOp",EDGE,"222680ed-d087-479c-bee2-353590fc5722.right")])],"isStart":false})]});
            var sketch = newSketch(context, id + "F30", { "sketchPlane" : qUnion([Q0])});
            skCircle(sketch, "E48", {"center": v(32.05, -0.05) * mm, "radius": 1.3 * mm});
            skCircle(sketch, "E49.0.1.0", {"center": v(32.05, 7.95) * mm, "radius": 1.3 * mm});
            skCircle(sketch, "E49.1.0.0", {"center": v(24.05, -0.05) * mm, "radius": 1.3 * mm});
            skCircle(sketch, "E49.1.1.0", {"center": v(24.05, 7.95) * mm, "radius": 1.3 * mm});
            skLineSegment(sketch, "E49.direction1", {"start": v(32.05, -0.05) * mm, "end": v(24.05, -0.05) * mm, "construction": true});
            skLineSegment(sketch, "E49.direction2", {"start": v(32.05, -0.05) * mm, "end": v(32.05, 7.95) * mm, "construction": true});
            skLineSegment(sketch, "E50", {"start": v(15.95, 8.05) * mm, "end": v(24.05, -0.05) * mm, "construction": true});
            skLineSegment(sketch, "E51", {"start": v(32.05, 7.95) * mm, "end": v(24.05, -0.05) * mm, "construction": true});
            skLineSegment(sketch, "E52", {"start": v(32.05, -0.05) * mm, "end": v(24.05, 7.95) * mm, "construction": true});
            skLineSegment(sketch, "E53", {"start": v(24.05, 7.95) * mm, "end": v(15.95, 0.05) * mm, "construction": true});
            skSolve(sketch);
        }
        {
            var Q0;
            Q0 = qSketchRegion(id + "F30", true);
            extrude(context, id + "F31", {"entities" : qUnion([Q0]), "operationType" : NewBodyOperationType.REMOVE, "oppositeDirection" : true, "depth" : 1.2 * mm});
        }
        {
            var Q0;
            Q0=qCreatedBy(makeId("Top.planeOp"),FACE);
            var sketch = newSketch(context, id + "F32", { "sketchPlane" : qUnion([Q0])});
            skLineSegment(sketch, "E54.bottom", {"start": v(28, -20) * mm, "end": v(36, -20) * mm});
            skLineSegment(sketch, "E54.top", {"start": v(28, -12) * mm, "end": v(36, -12) * mm});
            skLineSegment(sketch, "E54.left", {"start": v(28, -20) * mm, "end": v(28, -12) * mm});
            skLineSegment(sketch, "E54.right", {"start": v(36, -20) * mm, "end": v(36, -12) * mm});
            skSolve(sketch);
        }
        {
            var Q0;
            Q0=makeQuery(id+"F32.imprint","IMPRINT",FACE,{"disambiguationData":[TD([[makeQuery(id+"F32.imprint","IMPRINT",EDGE,{"derivedFrom":sQuery(id+"F32.wireOp",EDGE,"E54.bottom")}),1.0]])]});
            extrude(context, id + "F33", {"entities" : qUnion([Q0]), "operationType" : NewBodyOperationType.ADD, "depth" : 6.4 * mm});
        }
        {
            var Q0;
            Q0=qCreatedBy(makeId("Top.planeOp"),FACE);
            var sketch = newSketch(context, id + "F34", { "sketchPlane" : qUnion([Q0])});
            skLineSegment(sketch, "E55.bottom", {"start": v(36, -12) * mm, "end": v(44, -12) * mm});
            skLineSegment(sketch, "E55.top", {"start": v(36, -20) * mm, "end": v(44, -20) * mm});
            skLineSegment(sketch, "E55.left", {"start": v(36, -12) * mm, "end": v(36, -20) * mm});
            skLineSegment(sketch, "E55.right", {"start": v(44, -12) * mm, "end": v(44, -20) * mm});
            skSolve(sketch);
        }
        {
            var Q0;
            Q0=makeQuery(id+"F34.imprint","IMPRINT",FACE,{"disambiguationData":[TD([[makeQuery(id+"F34.imprint","IMPRINT",EDGE,{"derivedFrom":sQuery(id+"F34.wireOp",EDGE,"E55.bottom")}),-1.0]])]});
            extrude(context, id + "F35", {"entities" : qUnion([Q0]), "operationType" : NewBodyOperationType.ADD, "depth" : 6.4 * mm});
        }
        {
            var Q0;
            Q0=qCreatedBy(makeId("Top.planeOp"),FACE);
            var sketch = newSketch(context, id + "F36", { "sketchPlane" : qUnion([Q0])});
            skLineSegment(sketch, "E56.bottom", {"start": v(36, -20) * mm, "end": v(44, -20) * mm});
            skLineSegment(sketch, "E56.top", {"start": v(36, -28) * mm, "end": v(44, -28) * mm});
            skLineSegment(sketch, "E56.left", {"start": v(36, -20) * mm, "end": v(36, -28) * mm});
            skLineSegment(sketch, "E56.right", {"start": v(44, -20) * mm, "end": v(44, -28) * mm});
            skSolve(sketch);
        }
        {
            var Q0;
            Q0=makeQuery(id+"F36.imprint","IMPRINT",FACE,{"disambiguationData":[TD([[makeQuery(id+"F36.imprint","IMPRINT",EDGE,{"derivedFrom":sQuery(id+"F36.wireOp",EDGE,"E56.bottom")}),-1.0]])]});
            extrude(context, id + "F37", {"entities" : qUnion([Q0]), "operationType" : NewBodyOperationType.ADD, "depth" : 6.4 * mm});
        }
        {
            var Q0;
            Q0=qCreatedBy(makeId("Top.planeOp"),FACE);
            var sketch = newSketch(context, id + "F38", { "sketchPlane" : qUnion([Q0])});
            skLineSegment(sketch, "E57.bottom", {"start": v(28, 12) * mm, "end": v(44, 12) * mm});
            skLineSegment(sketch, "E57.top", {"start": v(28, 4) * mm, "end": v(44, 4) * mm});
            skLineSegment(sketch, "E57.left", {"start": v(28, 12) * mm, "end": v(28, 4) * mm});
            skLineSegment(sketch, "E57.right", {"start": v(44, 12) * mm, "end": v(44, 4) * mm});
            skSolve(sketch);
        }
        {
            var Q0;
            Q0=makeQuery(id+"F38.imprint","IMPRINT",FACE,{"disambiguationData":[TD([[makeQuery(id+"F38.imprint","IMPRINT",EDGE,{"derivedFrom":sQuery(id+"F38.wireOp",EDGE,"E57.bottom")}),-1.0]])]});
            extrude(context, id + "F39", {"entities" : qUnion([Q0]), "operationType" : NewBodyOperationType.ADD, "depth" : 6.4 * mm});
        }
        {
            var Q0;
            Q0=qCreatedBy(makeId("Top.planeOp"),FACE);
            var sketch = newSketch(context, id + "F40", { "sketchPlane" : qUnion([Q0])});
            skLineSegment(sketch, "E58.bottom", {"start": v(36, 28) * mm, "end": v(44, 28) * mm});
            skLineSegment(sketch, "E58.top", {"start": v(36, 12) * mm, "end": v(44, 12) * mm});
            skLineSegment(sketch, "E58.left", {"start": v(36, 28) * mm, "end": v(36, 12) * mm});
            skLineSegment(sketch, "E58.right", {"start": v(44, 28) * mm, "end": v(44, 12) * mm});
            skSolve(sketch);
        }
        {
            var Q0;
            Q0=makeQuery(id+"F40.imprint","IMPRINT",FACE,{"disambiguationData":[TD([[makeQuery(id+"F40.imprint","IMPRINT",EDGE,{"derivedFrom":sQuery(id+"F40.wireOp",EDGE,"E58.bottom")}),-1.0]])]});
            extrude(context, id + "F41", {"entities" : qUnion([Q0]), "operationType" : NewBodyOperationType.ADD, "depth" : 6.4 * mm});
        }
        {
            var Q0;
            Q0=makeQuery(id+"F41.boolean.opBoolean","MERGE",FACE,{"derivedFrom":[makeQuery(id+"F39.boolean.opBoolean","MERGE",FACE,{"derivedFrom":[makeQuery(id+"F37.boolean.opBoolean","MERGE",FACE,{"derivedFrom":[makeQuery(id+"F35.boolean.opBoolean","MERGE",FACE,{"derivedFrom":[makeQuery(id+"F33.boolean.opBoolean","MERGE",FACE,{"derivedFrom":[makeQuery(id+"F7.boolean.opBoolean","MERGE",FACE,{"derivedFrom":[makeQuery(id+"F1.opExtrude","CAP_FACE",FACE,{"disambiguationData":[OSD([sQuery(id+"F0.wireOp",EDGE,"E0.rect.bottom"),sQuery(id+"F0.wireOp",EDGE,"E0.rect.top"),sQuery(id+"F0.wireOp",EDGE,"E0.rect.left"),sQuery(id+"F0.wireOp",EDGE,"E0.rect.right")])],"isStart":false}),makeQuery(id+"F7.opExtrude","CAP_FACE",FACE,{"disambiguationData":[OSD([sQuery(id+"F6.wireOp",EDGE,"E3.bottom"),sQuery(id+"F6.wireOp",EDGE,"E3.top"),sQuery(id+"F6.wireOp",EDGE,"E3.left"),sQuery(id+"F6.wireOp",EDGE,"E3.right")])],"isStart":false})]}),makeQuery(id+"F33.opExtrude","CAP_FACE",FACE,{"disambiguationData":[OSD([sQuery(id+"F32.wireOp",EDGE,"E54.bottom"),sQuery(id+"F32.wireOp",EDGE,"E54.top"),sQuery(id+"F32.wireOp",EDGE,"E54.left"),sQuery(id+"F32.wireOp",EDGE,"E54.right")])],"isStart":false})]}),makeQuery(id+"F35.opExtrude","CAP_FACE",FACE,{"disambiguationData":[OSD([sQuery(id+"F34.wireOp",EDGE,"E55.bottom"),sQuery(id+"F34.wireOp",EDGE,"E55.top"),sQuery(id+"F34.wireOp",EDGE,"E55.left"),sQuery(id+"F34.wireOp",EDGE,"E55.right")])],"isStart":false})]}),makeQuery(id+"F37.opExtrude","CAP_FACE",FACE,{"disambiguationData":[OSD([sQuery(id+"F36.wireOp",EDGE,"E56.bottom"),sQuery(id+"F36.wireOp",EDGE,"E56.top"),sQuery(id+"F36.wireOp",EDGE,"E56.left"),sQuery(id+"F36.wireOp",EDGE,"E56.right")])],"isStart":false})]}),makeQuery(id+"F39.opExtrude","CAP_FACE",FACE,{"disambiguationData":[OSD([sQuery(id+"F38.wireOp",EDGE,"E57.bottom"),sQuery(id+"F38.wireOp",EDGE,"E57.top"),sQuery(id+"F38.wireOp",EDGE,"E57.left"),sQuery(id+"F38.wireOp",EDGE,"E57.right")])],"isStart":false})]}),makeQuery(id+"F41.opExtrude","CAP_FACE",FACE,{"disambiguationData":[OSD([sQuery(id+"F40.wireOp",EDGE,"E58.bottom"),sQuery(id+"F40.wireOp",EDGE,"E58.top"),sQuery(id+"F40.wireOp",EDGE,"E58.left"),sQuery(id+"F40.wireOp",EDGE,"E58.right")])],"isStart":false})]});
            var sketch = newSketch(context, id + "F42", { "sketchPlane" : qUnion([Q0])});
            skCircle(sketch, "E59", {"center": v(31.95, 8.05) * mm, "radius": 2.4 * mm});
            skCircle(sketch, "E60.1.0.0", {"center": v(39.95, 8.05) * mm, "radius": 2.4 * mm});
            skLineSegment(sketch, "E60.direction1", {"start": v(31.95, 8.05) * mm, "end": v(39.95, 8.05) * mm, "construction": true});
            skSolve(sketch);
        }
        {
            var Q0;
            Q0 = qSketchRegion(id + "F42", true);
            extrude(context, id + "F43", {"entities" : qUnion([Q0]), "operationType" : NewBodyOperationType.ADD, "depth" : 1.8 * mm});
        }
        {
            var Q0;
            Q0=makeQuery(id+"F41.boolean.opBoolean","MERGE",FACE,{"derivedFrom":[makeQuery(id+"F39.boolean.opBoolean","MERGE",FACE,{"derivedFrom":[makeQuery(id+"F37.boolean.opBoolean","MERGE",FACE,{"derivedFrom":[makeQuery(id+"F35.boolean.opBoolean","MERGE",FACE,{"derivedFrom":[makeQuery(id+"F33.boolean.opBoolean","MERGE",FACE,{"derivedFrom":[makeQuery(id+"F7.boolean.opBoolean","MERGE",FACE,{"derivedFrom":[makeQuery(id+"F1.opExtrude","CAP_FACE",FACE,{"disambiguationData":[OSD([sQuery(id+"F0.wireOp",EDGE,"E0.rect.bottom"),sQuery(id+"F0.wireOp",EDGE,"E0.rect.top"),sQuery(id+"F0.wireOp",EDGE,"E0.rect.left"),sQuery(id+"F0.wireOp",EDGE,"E0.rect.right")])],"isStart":false}),makeQuery(id+"F7.opExtrude","CAP_FACE",FACE,{"disambiguationData":[OSD([sQuery(id+"F6.wireOp",EDGE,"E3.bottom"),sQuery(id+"F6.wireOp",EDGE,"E3.top"),sQuery(id+"F6.wireOp",EDGE,"E3.left"),sQuery(id+"F6.wireOp",EDGE,"E3.right")])],"isStart":false})]}),makeQuery(id+"F33.opExtrude","CAP_FACE",FACE,{"disambiguationData":[OSD([sQuery(id+"F32.wireOp",EDGE,"E54.bottom"),sQuery(id+"F32.wireOp",EDGE,"E54.top"),sQuery(id+"F32.wireOp",EDGE,"E54.left"),sQuery(id+"F32.wireOp",EDGE,"E54.right")])],"isStart":false})]}),makeQuery(id+"F35.opExtrude","CAP_FACE",FACE,{"disambiguationData":[OSD([sQuery(id+"F34.wireOp",EDGE,"E55.bottom"),sQuery(id+"F34.wireOp",EDGE,"E55.top"),sQuery(id+"F34.wireOp",EDGE,"E55.left"),sQuery(id+"F34.wireOp",EDGE,"E55.right")])],"isStart":false})]}),makeQuery(id+"F37.opExtrude","CAP_FACE",FACE,{"disambiguationData":[OSD([sQuery(id+"F36.wireOp",EDGE,"E56.bottom"),sQuery(id+"F36.wireOp",EDGE,"E56.top"),sQuery(id+"F36.wireOp",EDGE,"E56.left"),sQuery(id+"F36.wireOp",EDGE,"E56.right")])],"isStart":false})]}),makeQuery(id+"F39.opExtrude","CAP_FACE",FACE,{"disambiguationData":[OSD([sQuery(id+"F38.wireOp",EDGE,"E57.bottom"),sQuery(id+"F38.wireOp",EDGE,"E57.top"),sQuery(id+"F38.wireOp",EDGE,"E57.left"),sQuery(id+"F38.wireOp",EDGE,"E57.right")])],"isStart":false})]}),makeQuery(id+"F41.opExtrude","CAP_FACE",FACE,{"disambiguationData":[OSD([sQuery(id+"F40.wireOp",EDGE,"E58.bottom"),sQuery(id+"F40.wireOp",EDGE,"E58.top"),sQuery(id+"F40.wireOp",EDGE,"E58.left"),sQuery(id+"F40.wireOp",EDGE,"E58.right")])],"isStart":false})]});
            var sketch = newSketch(context, id + "F44", { "sketchPlane" : qUnion([Q0])});
            skCircle(sketch, "E61", {"center": v(39.95, 24.05) * mm, "radius": 2.4 * mm});
            skCircle(sketch, "E62.0.1.0", {"center": v(39.95, 16.05) * mm, "radius": 2.4 * mm});
            skLineSegment(sketch, "E62.direction1", {"start": v(39.95, 24.05) * mm, "end": v(64.95, 24.05) * mm, "construction": true});
            skLineSegment(sketch, "E62.direction2", {"start": v(39.95, 24.05) * mm, "end": v(39.95, 16.05) * mm, "construction": true});
            skSolve(sketch);
        }
        {
            var Q0;
            Q0 = qSketchRegion(id + "F44", true);
            extrude(context, id + "F45", {"entities" : qUnion([Q0]), "operationType" : NewBodyOperationType.ADD, "depth" : 1.8 * mm});
        }
        {
            var Q0;
            Q0=makeQuery(id+"F41.boolean.opBoolean","MERGE",FACE,{"derivedFrom":[makeQuery(id+"F39.boolean.opBoolean","MERGE",FACE,{"derivedFrom":[makeQuery(id+"F37.boolean.opBoolean","MERGE",FACE,{"derivedFrom":[makeQuery(id+"F35.boolean.opBoolean","MERGE",FACE,{"derivedFrom":[makeQuery(id+"F33.boolean.opBoolean","MERGE",FACE,{"derivedFrom":[makeQuery(id+"F7.boolean.opBoolean","MERGE",FACE,{"derivedFrom":[makeQuery(id+"F1.opExtrude","CAP_FACE",FACE,{"disambiguationData":[OSD([sQuery(id+"F0.wireOp",EDGE,"E0.rect.bottom"),sQuery(id+"F0.wireOp",EDGE,"E0.rect.top"),sQuery(id+"F0.wireOp",EDGE,"E0.rect.left"),sQuery(id+"F0.wireOp",EDGE,"E0.rect.right")])],"isStart":false}),makeQuery(id+"F7.opExtrude","CAP_FACE",FACE,{"disambiguationData":[OSD([sQuery(id+"F6.wireOp",EDGE,"E3.bottom"),sQuery(id+"F6.wireOp",EDGE,"E3.top"),sQuery(id+"F6.wireOp",EDGE,"E3.left"),sQuery(id+"F6.wireOp",EDGE,"E3.right")])],"isStart":false})]}),makeQuery(id+"F33.opExtrude","CAP_FACE",FACE,{"disambiguationData":[OSD([sQuery(id+"F32.wireOp",EDGE,"E54.bottom"),sQuery(id+"F32.wireOp",EDGE,"E54.top"),sQuery(id+"F32.wireOp",EDGE,"E54.left"),sQuery(id+"F32.wireOp",EDGE,"E54.right")])],"isStart":false})]}),makeQuery(id+"F35.opExtrude","CAP_FACE",FACE,{"disambiguationData":[OSD([sQuery(id+"F34.wireOp",EDGE,"E55.bottom"),sQuery(id+"F34.wireOp",EDGE,"E55.top"),sQuery(id+"F34.wireOp",EDGE,"E55.left"),sQuery(id+"F34.wireOp",EDGE,"E55.right")])],"isStart":false})]}),makeQuery(id+"F37.opExtrude","CAP_FACE",FACE,{"disambiguationData":[OSD([sQuery(id+"F36.wireOp",EDGE,"E56.bottom"),sQuery(id+"F36.wireOp",EDGE,"E56.top"),sQuery(id+"F36.wireOp",EDGE,"E56.left"),sQuery(id+"F36.wireOp",EDGE,"E56.right")])],"isStart":false})]}),makeQuery(id+"F39.opExtrude","CAP_FACE",FACE,{"disambiguationData":[OSD([sQuery(id+"F38.wireOp",EDGE,"E57.bottom"),sQuery(id+"F38.wireOp",EDGE,"E57.top"),sQuery(id+"F38.wireOp",EDGE,"E57.left"),sQuery(id+"F38.wireOp",EDGE,"E57.right")])],"isStart":false})]}),makeQuery(id+"F41.opExtrude","CAP_FACE",FACE,{"disambiguationData":[OSD([sQuery(id+"F40.wireOp",EDGE,"E58.bottom"),sQuery(id+"F40.wireOp",EDGE,"E58.top"),sQuery(id+"F40.wireOp",EDGE,"E58.left"),sQuery(id+"F40.wireOp",EDGE,"E58.right")])],"isStart":false})]});
            var sketch = newSketch(context, id + "F46", { "sketchPlane" : qUnion([Q0])});
            skCircle(sketch, "E63", {"center": v(31.95, -16.05) * mm, "radius": 2.4 * mm});
            skCircle(sketch, "E64.1.0.0", {"center": v(39.95, -16.05) * mm, "radius": 2.4 * mm});
            skLineSegment(sketch, "E64.direction1", {"start": v(31.95, -16.05) * mm, "end": v(39.95, -16.05) * mm, "construction": true});
            skSolve(sketch);
        }
        {
            var Q0;
            Q0 = qSketchRegion(id + "F46", true);
            extrude(context, id + "F47", {"entities" : qUnion([Q0]), "operationType" : NewBodyOperationType.ADD, "depth" : 1.8 * mm});
        }
        {
            var Q0;
            Q0=makeQuery(id+"F41.boolean.opBoolean","MERGE",FACE,{"derivedFrom":[makeQuery(id+"F39.boolean.opBoolean","MERGE",FACE,{"derivedFrom":[makeQuery(id+"F37.boolean.opBoolean","MERGE",FACE,{"derivedFrom":[makeQuery(id+"F35.boolean.opBoolean","MERGE",FACE,{"derivedFrom":[makeQuery(id+"F33.boolean.opBoolean","MERGE",FACE,{"derivedFrom":[makeQuery(id+"F7.boolean.opBoolean","MERGE",FACE,{"derivedFrom":[makeQuery(id+"F1.opExtrude","CAP_FACE",FACE,{"disambiguationData":[OSD([sQuery(id+"F0.wireOp",EDGE,"E0.rect.bottom"),sQuery(id+"F0.wireOp",EDGE,"E0.rect.top"),sQuery(id+"F0.wireOp",EDGE,"E0.rect.left"),sQuery(id+"F0.wireOp",EDGE,"E0.rect.right")])],"isStart":false}),makeQuery(id+"F7.opExtrude","CAP_FACE",FACE,{"disambiguationData":[OSD([sQuery(id+"F6.wireOp",EDGE,"E3.bottom"),sQuery(id+"F6.wireOp",EDGE,"E3.top"),sQuery(id+"F6.wireOp",EDGE,"E3.left"),sQuery(id+"F6.wireOp",EDGE,"E3.right")])],"isStart":false})]}),makeQuery(id+"F33.opExtrude","CAP_FACE",FACE,{"disambiguationData":[OSD([sQuery(id+"F32.wireOp",EDGE,"E54.bottom"),sQuery(id+"F32.wireOp",EDGE,"E54.top"),sQuery(id+"F32.wireOp",EDGE,"E54.left"),sQuery(id+"F32.wireOp",EDGE,"E54.right")])],"isStart":false})]}),makeQuery(id+"F35.opExtrude","CAP_FACE",FACE,{"disambiguationData":[OSD([sQuery(id+"F34.wireOp",EDGE,"E55.bottom"),sQuery(id+"F34.wireOp",EDGE,"E55.top"),sQuery(id+"F34.wireOp",EDGE,"E55.left"),sQuery(id+"F34.wireOp",EDGE,"E55.right")])],"isStart":false})]}),makeQuery(id+"F37.opExtrude","CAP_FACE",FACE,{"disambiguationData":[OSD([sQuery(id+"F36.wireOp",EDGE,"E56.bottom"),sQuery(id+"F36.wireOp",EDGE,"E56.top"),sQuery(id+"F36.wireOp",EDGE,"E56.left"),sQuery(id+"F36.wireOp",EDGE,"E56.right")])],"isStart":false})]}),makeQuery(id+"F39.opExtrude","CAP_FACE",FACE,{"disambiguationData":[OSD([sQuery(id+"F38.wireOp",EDGE,"E57.bottom"),sQuery(id+"F38.wireOp",EDGE,"E57.top"),sQuery(id+"F38.wireOp",EDGE,"E57.left"),sQuery(id+"F38.wireOp",EDGE,"E57.right")])],"isStart":false})]}),makeQuery(id+"F41.opExtrude","CAP_FACE",FACE,{"disambiguationData":[OSD([sQuery(id+"F40.wireOp",EDGE,"E58.bottom"),sQuery(id+"F40.wireOp",EDGE,"E58.top"),sQuery(id+"F40.wireOp",EDGE,"E58.left"),sQuery(id+"F40.wireOp",EDGE,"E58.right")])],"isStart":false})]});
            var sketch = newSketch(context, id + "F48", { "sketchPlane" : qUnion([Q0])});
            skCircle(sketch, "E65", {"center": v(40.05, -24.05) * mm, "radius": 2.4 * mm});
            skSolve(sketch);
        }
        {
            var Q0;
            Q0 = qSketchRegion(id + "F48", true);
            extrude(context, id + "F49", {"entities" : qUnion([Q0]), "operationType" : NewBodyOperationType.ADD, "depth" : 1.8 * mm});
        }
        {
            var Q0;
            Q0=makeQuery(id+"F41.boolean.opBoolean","MERGE",FACE,{"derivedFrom":[makeQuery(id+"F39.boolean.opBoolean","MERGE",FACE,{"derivedFrom":[makeQuery(id+"F37.boolean.opBoolean","MERGE",FACE,{"derivedFrom":[makeQuery(id+"F35.boolean.opBoolean","MERGE",FACE,{"derivedFrom":[makeQuery(id+"F33.boolean.opBoolean","MERGE",FACE,{"derivedFrom":[makeQuery(id+"F7.boolean.opBoolean","MERGE",FACE,{"derivedFrom":[makeQuery(id+"F1.opExtrude","CAP_FACE",FACE,{"disambiguationData":[OSD([sQuery(id+"F0.wireOp",EDGE,"E0.rect.bottom"),sQuery(id+"F0.wireOp",EDGE,"E0.rect.top"),sQuery(id+"F0.wireOp",EDGE,"E0.rect.left"),sQuery(id+"F0.wireOp",EDGE,"E0.rect.right")])],"isStart":true}),makeQuery(id+"F7.opExtrude","CAP_FACE",FACE,{"disambiguationData":[OSD([sQuery(id+"F6.wireOp",EDGE,"E3.bottom"),sQuery(id+"F6.wireOp",EDGE,"E3.top"),sQuery(id+"F6.wireOp",EDGE,"E3.left"),sQuery(id+"F6.wireOp",EDGE,"E3.right")])],"isStart":true})]}),makeQuery(id+"F33.opExtrude","CAP_FACE",FACE,{"disambiguationData":[OSD([sQuery(id+"F32.wireOp",EDGE,"E54.bottom"),sQuery(id+"F32.wireOp",EDGE,"E54.top"),sQuery(id+"F32.wireOp",EDGE,"E54.left"),sQuery(id+"F32.wireOp",EDGE,"E54.right")])],"isStart":true})]}),makeQuery(id+"F35.opExtrude","CAP_FACE",FACE,{"disambiguationData":[OSD([sQuery(id+"F34.wireOp",EDGE,"E55.bottom"),sQuery(id+"F34.wireOp",EDGE,"E55.top"),sQuery(id+"F34.wireOp",EDGE,"E55.left"),sQuery(id+"F34.wireOp",EDGE,"E55.right")])],"isStart":true})]}),makeQuery(id+"F37.opExtrude","CAP_FACE",FACE,{"disambiguationData":[OSD([sQuery(id+"F36.wireOp",EDGE,"E56.bottom"),sQuery(id+"F36.wireOp",EDGE,"E56.top"),sQuery(id+"F36.wireOp",EDGE,"E56.left"),sQuery(id+"F36.wireOp",EDGE,"E56.right")])],"isStart":true})]}),makeQuery(id+"F39.opExtrude","CAP_FACE",FACE,{"disambiguationData":[OSD([sQuery(id+"F38.wireOp",EDGE,"E57.bottom"),sQuery(id+"F38.wireOp",EDGE,"E57.top"),sQuery(id+"F38.wireOp",EDGE,"E57.left"),sQuery(id+"F38.wireOp",EDGE,"E57.right")])],"isStart":true})]}),makeQuery(id+"F41.opExtrude","CAP_FACE",FACE,{"disambiguationData":[OSD([sQuery(id+"F40.wireOp",EDGE,"E58.bottom"),sQuery(id+"F40.wireOp",EDGE,"E58.top"),sQuery(id+"F40.wireOp",EDGE,"E58.left"),sQuery(id+"F40.wireOp",EDGE,"E58.right")])],"isStart":true})]});
            var sketch = newSketch(context, id + "F50", { "sketchPlane" : qUnion([Q0])});
            skLineSegment(sketch, "E66.bottom", {"start": v(29.2, 18.8) * mm, "end": v(34.8, 18.8) * mm});
            skLineSegment(sketch, "E66.top", {"start": v(29.2, 10.8) * mm, "end": v(34.8, 10.8) * mm});
            skLineSegment(sketch, "E66.left", {"start": v(29.2, 18.8) * mm, "end": v(29.2, 10.8) * mm});
            skLineSegment(sketch, "E66.right", {"start": v(34.8, 18.8) * mm, "end": v(34.8, 10.8) * mm});
            skSolve(sketch);
        }
        {
            var Q0;
            Q0 = qSketchRegion(id + "F50", true);
            extrude(context, id + "F51", {"entities" : qUnion([Q0]), "operationType" : NewBodyOperationType.REMOVE, "oppositeDirection" : true, "depth" : 5.2 * mm});
        }
        {
            var Q0;
            Q0=makeQuery(id+"F41.boolean.opBoolean","MERGE",FACE,{"derivedFrom":[makeQuery(id+"F39.boolean.opBoolean","MERGE",FACE,{"derivedFrom":[makeQuery(id+"F37.boolean.opBoolean","MERGE",FACE,{"derivedFrom":[makeQuery(id+"F35.boolean.opBoolean","MERGE",FACE,{"derivedFrom":[makeQuery(id+"F33.boolean.opBoolean","MERGE",FACE,{"derivedFrom":[makeQuery(id+"F7.boolean.opBoolean","MERGE",FACE,{"derivedFrom":[makeQuery(id+"F1.opExtrude","CAP_FACE",FACE,{"disambiguationData":[OSD([sQuery(id+"F0.wireOp",EDGE,"E0.rect.bottom"),sQuery(id+"F0.wireOp",EDGE,"E0.rect.top"),sQuery(id+"F0.wireOp",EDGE,"E0.rect.left"),sQuery(id+"F0.wireOp",EDGE,"E0.rect.right")])],"isStart":true}),makeQuery(id+"F7.opExtrude","CAP_FACE",FACE,{"disambiguationData":[OSD([sQuery(id+"F6.wireOp",EDGE,"E3.bottom"),sQuery(id+"F6.wireOp",EDGE,"E3.top"),sQuery(id+"F6.wireOp",EDGE,"E3.left"),sQuery(id+"F6.wireOp",EDGE,"E3.right")])],"isStart":true})]}),makeQuery(id+"F33.opExtrude","CAP_FACE",FACE,{"disambiguationData":[OSD([sQuery(id+"F32.wireOp",EDGE,"E54.bottom"),sQuery(id+"F32.wireOp",EDGE,"E54.top"),sQuery(id+"F32.wireOp",EDGE,"E54.left"),sQuery(id+"F32.wireOp",EDGE,"E54.right")])],"isStart":true})]}),makeQuery(id+"F35.opExtrude","CAP_FACE",FACE,{"disambiguationData":[OSD([sQuery(id+"F34.wireOp",EDGE,"E55.bottom"),sQuery(id+"F34.wireOp",EDGE,"E55.top"),sQuery(id+"F34.wireOp",EDGE,"E55.left"),sQuery(id+"F34.wireOp",EDGE,"E55.right")])],"isStart":true})]}),makeQuery(id+"F37.opExtrude","CAP_FACE",FACE,{"disambiguationData":[OSD([sQuery(id+"F36.wireOp",EDGE,"E56.bottom"),sQuery(id+"F36.wireOp",EDGE,"E56.top"),sQuery(id+"F36.wireOp",EDGE,"E56.left"),sQuery(id+"F36.wireOp",EDGE,"E56.right")])],"isStart":true})]}),makeQuery(id+"F39.opExtrude","CAP_FACE",FACE,{"disambiguationData":[OSD([sQuery(id+"F38.wireOp",EDGE,"E57.bottom"),sQuery(id+"F38.wireOp",EDGE,"E57.top"),sQuery(id+"F38.wireOp",EDGE,"E57.left"),sQuery(id+"F38.wireOp",EDGE,"E57.right")])],"isStart":true})]}),makeQuery(id+"F41.opExtrude","CAP_FACE",FACE,{"disambiguationData":[OSD([sQuery(id+"F40.wireOp",EDGE,"E58.bottom"),sQuery(id+"F40.wireOp",EDGE,"E58.top"),sQuery(id+"F40.wireOp",EDGE,"E58.left"),sQuery(id+"F40.wireOp",EDGE,"E58.right")])],"isStart":true})]});
            var sketch = newSketch(context, id + "F52", { "sketchPlane" : qUnion([Q0])});
            skLineSegment(sketch, "E67.bottom", {"start": v(42.8, 18.8) * mm, "end": v(34.8, 18.8) * mm});
            skLineSegment(sketch, "E67.top", {"start": v(42.8, 13.2) * mm, "end": v(34.8, 13.2) * mm});
            skLineSegment(sketch, "E67.left", {"start": v(42.8, 18.8) * mm, "end": v(42.8, 13.2) * mm});
            skLineSegment(sketch, "E67.right", {"start": v(34.8, 18.8) * mm, "end": v(34.8, 13.2) * mm});
            skSolve(sketch);
        }
        {
            var Q0;
            Q0 = qSketchRegion(id + "F52", true);
            extrude(context, id + "F53", {"entities" : qUnion([Q0]), "operationType" : NewBodyOperationType.REMOVE, "oppositeDirection" : true, "depth" : 5.2 * mm});
        }
        {
            var Q0;
            Q0=makeQuery(id+"F41.boolean.opBoolean","MERGE",FACE,{"derivedFrom":[makeQuery(id+"F39.boolean.opBoolean","MERGE",FACE,{"derivedFrom":[makeQuery(id+"F37.boolean.opBoolean","MERGE",FACE,{"derivedFrom":[makeQuery(id+"F35.boolean.opBoolean","MERGE",FACE,{"derivedFrom":[makeQuery(id+"F33.boolean.opBoolean","MERGE",FACE,{"derivedFrom":[makeQuery(id+"F7.boolean.opBoolean","MERGE",FACE,{"derivedFrom":[makeQuery(id+"F1.opExtrude","CAP_FACE",FACE,{"disambiguationData":[OSD([sQuery(id+"F0.wireOp",EDGE,"E0.rect.bottom"),sQuery(id+"F0.wireOp",EDGE,"E0.rect.top"),sQuery(id+"F0.wireOp",EDGE,"E0.rect.left"),sQuery(id+"F0.wireOp",EDGE,"E0.rect.right")])],"isStart":true}),makeQuery(id+"F7.opExtrude","CAP_FACE",FACE,{"disambiguationData":[OSD([sQuery(id+"F6.wireOp",EDGE,"E3.bottom"),sQuery(id+"F6.wireOp",EDGE,"E3.top"),sQuery(id+"F6.wireOp",EDGE,"E3.left"),sQuery(id+"F6.wireOp",EDGE,"E3.right")])],"isStart":true})]}),makeQuery(id+"F33.opExtrude","CAP_FACE",FACE,{"disambiguationData":[OSD([sQuery(id+"F32.wireOp",EDGE,"E54.bottom"),sQuery(id+"F32.wireOp",EDGE,"E54.top"),sQuery(id+"F32.wireOp",EDGE,"E54.left"),sQuery(id+"F32.wireOp",EDGE,"E54.right")])],"isStart":true})]}),makeQuery(id+"F35.opExtrude","CAP_FACE",FACE,{"disambiguationData":[OSD([sQuery(id+"F34.wireOp",EDGE,"E55.bottom"),sQuery(id+"F34.wireOp",EDGE,"E55.top"),sQuery(id+"F34.wireOp",EDGE,"E55.left"),sQuery(id+"F34.wireOp",EDGE,"E55.right")])],"isStart":true})]}),makeQuery(id+"F37.opExtrude","CAP_FACE",FACE,{"disambiguationData":[OSD([sQuery(id+"F36.wireOp",EDGE,"E56.bottom"),sQuery(id+"F36.wireOp",EDGE,"E56.top"),sQuery(id+"F36.wireOp",EDGE,"E56.left"),sQuery(id+"F36.wireOp",EDGE,"E56.right")])],"isStart":true})]}),makeQuery(id+"F39.opExtrude","CAP_FACE",FACE,{"disambiguationData":[OSD([sQuery(id+"F38.wireOp",EDGE,"E57.bottom"),sQuery(id+"F38.wireOp",EDGE,"E57.top"),sQuery(id+"F38.wireOp",EDGE,"E57.left"),sQuery(id+"F38.wireOp",EDGE,"E57.right")])],"isStart":true})]}),makeQuery(id+"F41.opExtrude","CAP_FACE",FACE,{"disambiguationData":[OSD([sQuery(id+"F40.wireOp",EDGE,"E58.bottom"),sQuery(id+"F40.wireOp",EDGE,"E58.top"),sQuery(id+"F40.wireOp",EDGE,"E58.left"),sQuery(id+"F40.wireOp",EDGE,"E58.right")])],"isStart":true})]});
            var sketch = newSketch(context, id + "F54", { "sketchPlane" : qUnion([Q0])});
            skLineSegment(sketch, "E68.bottom", {"start": v(37.2, 26.8) * mm, "end": v(42.8, 26.8) * mm});
            skLineSegment(sketch, "E68.top", {"start": v(37.2, 18.8) * mm, "end": v(42.8, 18.8) * mm});
            skLineSegment(sketch, "E68.left", {"start": v(37.2, 26.8) * mm, "end": v(37.2, 18.8) * mm});
            skLineSegment(sketch, "E68.right", {"start": v(42.8, 26.8) * mm, "end": v(42.8, 18.8) * mm});
            skSolve(sketch);
        }
        {
            var Q0;
            Q0 = qSketchRegion(id + "F54", true);
            extrude(context, id + "F55", {"entities" : qUnion([Q0]), "operationType" : NewBodyOperationType.REMOVE, "oppositeDirection" : true, "depth" : 5.2 * mm});
        }
        {
            var Q0;
            Q0=makeQuery(id+"F41.boolean.opBoolean","MERGE",FACE,{"derivedFrom":[makeQuery(id+"F39.boolean.opBoolean","MERGE",FACE,{"derivedFrom":[makeQuery(id+"F37.boolean.opBoolean","MERGE",FACE,{"derivedFrom":[makeQuery(id+"F35.boolean.opBoolean","MERGE",FACE,{"derivedFrom":[makeQuery(id+"F33.boolean.opBoolean","MERGE",FACE,{"derivedFrom":[makeQuery(id+"F7.boolean.opBoolean","MERGE",FACE,{"derivedFrom":[makeQuery(id+"F1.opExtrude","CAP_FACE",FACE,{"disambiguationData":[OSD([sQuery(id+"F0.wireOp",EDGE,"E0.rect.bottom"),sQuery(id+"F0.wireOp",EDGE,"E0.rect.top"),sQuery(id+"F0.wireOp",EDGE,"E0.rect.left"),sQuery(id+"F0.wireOp",EDGE,"E0.rect.right")])],"isStart":true}),makeQuery(id+"F7.opExtrude","CAP_FACE",FACE,{"disambiguationData":[OSD([sQuery(id+"F6.wireOp",EDGE,"E3.bottom"),sQuery(id+"F6.wireOp",EDGE,"E3.top"),sQuery(id+"F6.wireOp",EDGE,"E3.left"),sQuery(id+"F6.wireOp",EDGE,"E3.right")])],"isStart":true})]}),makeQuery(id+"F33.opExtrude","CAP_FACE",FACE,{"disambiguationData":[OSD([sQuery(id+"F32.wireOp",EDGE,"E54.bottom"),sQuery(id+"F32.wireOp",EDGE,"E54.top"),sQuery(id+"F32.wireOp",EDGE,"E54.left"),sQuery(id+"F32.wireOp",EDGE,"E54.right")])],"isStart":true})]}),makeQuery(id+"F35.opExtrude","CAP_FACE",FACE,{"disambiguationData":[OSD([sQuery(id+"F34.wireOp",EDGE,"E55.bottom"),sQuery(id+"F34.wireOp",EDGE,"E55.top"),sQuery(id+"F34.wireOp",EDGE,"E55.left"),sQuery(id+"F34.wireOp",EDGE,"E55.right")])],"isStart":true})]}),makeQuery(id+"F37.opExtrude","CAP_FACE",FACE,{"disambiguationData":[OSD([sQuery(id+"F36.wireOp",EDGE,"E56.bottom"),sQuery(id+"F36.wireOp",EDGE,"E56.top"),sQuery(id+"F36.wireOp",EDGE,"E56.left"),sQuery(id+"F36.wireOp",EDGE,"E56.right")])],"isStart":true})]}),makeQuery(id+"F39.opExtrude","CAP_FACE",FACE,{"disambiguationData":[OSD([sQuery(id+"F38.wireOp",EDGE,"E57.bottom"),sQuery(id+"F38.wireOp",EDGE,"E57.top"),sQuery(id+"F38.wireOp",EDGE,"E57.left"),sQuery(id+"F38.wireOp",EDGE,"E57.right")])],"isStart":true})]}),makeQuery(id+"F41.opExtrude","CAP_FACE",FACE,{"disambiguationData":[OSD([sQuery(id+"F40.wireOp",EDGE,"E58.bottom"),sQuery(id+"F40.wireOp",EDGE,"E58.top"),sQuery(id+"F40.wireOp",EDGE,"E58.left"),sQuery(id+"F40.wireOp",EDGE,"E58.right")])],"isStart":true})]});
            var sketch = newSketch(context, id + "F56", { "sketchPlane" : qUnion([Q0])});
            skLineSegment(sketch, "E69.bottom", {"start": v(29.2, -2.8) * mm, "end": v(34.8, -2.8) * mm});
            skLineSegment(sketch, "E69.top", {"start": v(29.2, -10.8) * mm, "end": v(34.8, -10.8) * mm});
            skLineSegment(sketch, "E69.left", {"start": v(29.2, -2.8) * mm, "end": v(29.2, -10.8) * mm});
            skLineSegment(sketch, "E69.right", {"start": v(34.8, -2.8) * mm, "end": v(34.8, -10.8) * mm});
            skSolve(sketch);
        }
        {
            var Q0;
            Q0=makeQuery(id+"F56.imprint","IMPRINT",FACE,{"disambiguationData":[TD([[makeQuery(id+"F56.imprint","IMPRINT",EDGE,{"derivedFrom":sQuery(id+"F56.wireOp",EDGE,"E69.bottom")}),-1.0]])]});
            extrude(context, id + "F57", {"entities" : qUnion([Q0]), "operationType" : NewBodyOperationType.REMOVE, "oppositeDirection" : true, "depth" : 5.2 * mm});
        }
        {
            var Q0;
            Q0=makeQuery(id+"F41.boolean.opBoolean","MERGE",FACE,{"derivedFrom":[makeQuery(id+"F39.boolean.opBoolean","MERGE",FACE,{"derivedFrom":[makeQuery(id+"F37.boolean.opBoolean","MERGE",FACE,{"derivedFrom":[makeQuery(id+"F35.boolean.opBoolean","MERGE",FACE,{"derivedFrom":[makeQuery(id+"F33.boolean.opBoolean","MERGE",FACE,{"derivedFrom":[makeQuery(id+"F7.boolean.opBoolean","MERGE",FACE,{"derivedFrom":[makeQuery(id+"F1.opExtrude","CAP_FACE",FACE,{"disambiguationData":[OSD([sQuery(id+"F0.wireOp",EDGE,"E0.rect.bottom"),sQuery(id+"F0.wireOp",EDGE,"E0.rect.top"),sQuery(id+"F0.wireOp",EDGE,"E0.rect.left"),sQuery(id+"F0.wireOp",EDGE,"E0.rect.right")])],"isStart":true}),makeQuery(id+"F7.opExtrude","CAP_FACE",FACE,{"disambiguationData":[OSD([sQuery(id+"F6.wireOp",EDGE,"E3.bottom"),sQuery(id+"F6.wireOp",EDGE,"E3.top"),sQuery(id+"F6.wireOp",EDGE,"E3.left"),sQuery(id+"F6.wireOp",EDGE,"E3.right")])],"isStart":true})]}),makeQuery(id+"F33.opExtrude","CAP_FACE",FACE,{"disambiguationData":[OSD([sQuery(id+"F32.wireOp",EDGE,"E54.bottom"),sQuery(id+"F32.wireOp",EDGE,"E54.top"),sQuery(id+"F32.wireOp",EDGE,"E54.left"),sQuery(id+"F32.wireOp",EDGE,"E54.right")])],"isStart":true})]}),makeQuery(id+"F35.opExtrude","CAP_FACE",FACE,{"disambiguationData":[OSD([sQuery(id+"F34.wireOp",EDGE,"E55.bottom"),sQuery(id+"F34.wireOp",EDGE,"E55.top"),sQuery(id+"F34.wireOp",EDGE,"E55.left"),sQuery(id+"F34.wireOp",EDGE,"E55.right")])],"isStart":true})]}),makeQuery(id+"F37.opExtrude","CAP_FACE",FACE,{"disambiguationData":[OSD([sQuery(id+"F36.wireOp",EDGE,"E56.bottom"),sQuery(id+"F36.wireOp",EDGE,"E56.top"),sQuery(id+"F36.wireOp",EDGE,"E56.left"),sQuery(id+"F36.wireOp",EDGE,"E56.right")])],"isStart":true})]}),makeQuery(id+"F39.opExtrude","CAP_FACE",FACE,{"disambiguationData":[OSD([sQuery(id+"F38.wireOp",EDGE,"E57.bottom"),sQuery(id+"F38.wireOp",EDGE,"E57.top"),sQuery(id+"F38.wireOp",EDGE,"E57.left"),sQuery(id+"F38.wireOp",EDGE,"E57.right")])],"isStart":true})]}),makeQuery(id+"F41.opExtrude","CAP_FACE",FACE,{"disambiguationData":[OSD([sQuery(id+"F40.wireOp",EDGE,"E58.bottom"),sQuery(id+"F40.wireOp",EDGE,"E58.top"),sQuery(id+"F40.wireOp",EDGE,"E58.left"),sQuery(id+"F40.wireOp",EDGE,"E58.right")])],"isStart":true})]});
            var sketch = newSketch(context, id + "F58", { "sketchPlane" : qUnion([Q0])});
            skLineSegment(sketch, "E70.bottom", {"start": v(34.8, -5.2) * mm, "end": v(42.8, -5.2) * mm});
            skLineSegment(sketch, "E70.top", {"start": v(34.8, -10.8) * mm, "end": v(42.8, -10.8) * mm});
            skLineSegment(sketch, "E70.left", {"start": v(34.8, -5.2) * mm, "end": v(34.8, -10.8) * mm});
            skLineSegment(sketch, "E70.right", {"start": v(42.8, -5.2) * mm, "end": v(42.8, -10.8) * mm});
            skSolve(sketch);
        }
        {
            var Q0;
            Q0=makeQuery(id+"F58.imprint","IMPRINT",FACE,{"disambiguationData":[TD([[makeQuery(id+"F58.imprint","IMPRINT",EDGE,{"derivedFrom":sQuery(id+"F58.wireOp",EDGE,"E70.bottom")}),-1.0]])]});
            extrude(context, id + "F59", {"entities" : qUnion([Q0]), "operationType" : NewBodyOperationType.REMOVE, "oppositeDirection" : true, "depth" : 5.2 * mm});
        }
        {
            var Q0;
            Q0=makeQuery(id+"F41.boolean.opBoolean","MERGE",FACE,{"derivedFrom":[makeQuery(id+"F39.boolean.opBoolean","MERGE",FACE,{"derivedFrom":[makeQuery(id+"F37.boolean.opBoolean","MERGE",FACE,{"derivedFrom":[makeQuery(id+"F35.boolean.opBoolean","MERGE",FACE,{"derivedFrom":[makeQuery(id+"F33.boolean.opBoolean","MERGE",FACE,{"derivedFrom":[makeQuery(id+"F7.boolean.opBoolean","MERGE",FACE,{"derivedFrom":[makeQuery(id+"F1.opExtrude","CAP_FACE",FACE,{"disambiguationData":[OSD([sQuery(id+"F0.wireOp",EDGE,"E0.rect.bottom"),sQuery(id+"F0.wireOp",EDGE,"E0.rect.top"),sQuery(id+"F0.wireOp",EDGE,"E0.rect.left"),sQuery(id+"F0.wireOp",EDGE,"E0.rect.right")])],"isStart":true}),makeQuery(id+"F7.opExtrude","CAP_FACE",FACE,{"disambiguationData":[OSD([sQuery(id+"F6.wireOp",EDGE,"E3.bottom"),sQuery(id+"F6.wireOp",EDGE,"E3.top"),sQuery(id+"F6.wireOp",EDGE,"E3.left"),sQuery(id+"F6.wireOp",EDGE,"E3.right")])],"isStart":true})]}),makeQuery(id+"F33.opExtrude","CAP_FACE",FACE,{"disambiguationData":[OSD([sQuery(id+"F32.wireOp",EDGE,"E54.bottom"),sQuery(id+"F32.wireOp",EDGE,"E54.top"),sQuery(id+"F32.wireOp",EDGE,"E54.left"),sQuery(id+"F32.wireOp",EDGE,"E54.right")])],"isStart":true})]}),makeQuery(id+"F35.opExtrude","CAP_FACE",FACE,{"disambiguationData":[OSD([sQuery(id+"F34.wireOp",EDGE,"E55.bottom"),sQuery(id+"F34.wireOp",EDGE,"E55.top"),sQuery(id+"F34.wireOp",EDGE,"E55.left"),sQuery(id+"F34.wireOp",EDGE,"E55.right")])],"isStart":true})]}),makeQuery(id+"F37.opExtrude","CAP_FACE",FACE,{"disambiguationData":[OSD([sQuery(id+"F36.wireOp",EDGE,"E56.bottom"),sQuery(id+"F36.wireOp",EDGE,"E56.top"),sQuery(id+"F36.wireOp",EDGE,"E56.left"),sQuery(id+"F36.wireOp",EDGE,"E56.right")])],"isStart":true})]}),makeQuery(id+"F39.opExtrude","CAP_FACE",FACE,{"disambiguationData":[OSD([sQuery(id+"F38.wireOp",EDGE,"E57.bottom"),sQuery(id+"F38.wireOp",EDGE,"E57.top"),sQuery(id+"F38.wireOp",EDGE,"E57.left"),sQuery(id+"F38.wireOp",EDGE,"E57.right")])],"isStart":true})]}),makeQuery(id+"F41.opExtrude","CAP_FACE",FACE,{"disambiguationData":[OSD([sQuery(id+"F40.wireOp",EDGE,"E58.bottom"),sQuery(id+"F40.wireOp",EDGE,"E58.top"),sQuery(id+"F40.wireOp",EDGE,"E58.left"),sQuery(id+"F40.wireOp",EDGE,"E58.right")])],"isStart":true})]});
            var sketch = newSketch(context, id + "F60", { "sketchPlane" : qUnion([Q0])});
            skLineSegment(sketch, "E71.bottom", {"start": v(37.2, -10.8) * mm, "end": v(42.8, -10.8) * mm});
            skLineSegment(sketch, "E71.top", {"start": v(37.2, -26.8) * mm, "end": v(42.8, -26.8) * mm});
            skLineSegment(sketch, "E71.left", {"start": v(37.2, -10.8) * mm, "end": v(37.2, -26.8) * mm});
            skLineSegment(sketch, "E71.right", {"start": v(42.8, -10.8) * mm, "end": v(42.8, -26.8) * mm});
            skSolve(sketch);
        }
        {
            var Q0;
            Q0=makeQuery(id+"F60.imprint","IMPRINT",FACE,{"disambiguationData":[TD([[makeQuery(id+"F60.imprint","IMPRINT",EDGE,{"derivedFrom":sQuery(id+"F60.wireOp",EDGE,"E71.bottom")}),-1.0]])]});
            extrude(context, id + "F61", {"entities" : qUnion([Q0]), "operationType" : NewBodyOperationType.REMOVE, "oppositeDirection" : true, "depth" : 5.2 * mm});
        }
        {
            var Q0;
            Q0=makeQuery(id+"F61.boolean.opBoolean","MERGE",FACE,{"derivedFrom":[makeQuery(id+"F59.boolean.opBoolean","MERGE",FACE,{"derivedFrom":[makeQuery(id+"F57.boolean.opBoolean","MERGE",FACE,{"derivedFrom":[makeQuery(id+"F55.boolean.opBoolean","MERGE",FACE,{"derivedFrom":[makeQuery(id+"F53.boolean.opBoolean","MERGE",FACE,{"derivedFrom":[makeQuery(id+"F51.boolean.opBoolean","MERGE",FACE,{"derivedFrom":[makeQuery(id+"F15.boolean.opBoolean","MERGE",FACE,{"derivedFrom":[makeQuery(id+"F13.boolean.opBoolean","MERGE",FACE,{"derivedFrom":[makeQuery(id+"F11.boolean.opBoolean","MERGE",FACE,{"derivedFrom":[makeQuery(id+"F9.boolean.opBoolean","COPY",FACE,{"derivedFrom":makeQuery(id+"F9.opExtrude","CAP_FACE",FACE,{"disambiguationData":[OSD([sQuery(id+"F8.wireOp",EDGE,"E4.bottom"),sQuery(id+"F8.wireOp",EDGE,"E4.top"),sQuery(id+"F8.wireOp",EDGE,"E4.left"),sQuery(id+"F8.wireOp",EDGE,"E4.right")])],"isStart":false})}),makeQuery(id+"F11.opExtrude","CAP_FACE",FACE,{"disambiguationData":[OSD([sQuery(id+"F10.wireOp",EDGE,"E5.bottom"),sQuery(id+"F10.wireOp",EDGE,"E5.top"),sQuery(id+"F10.wireOp",EDGE,"E5.left"),sQuery(id+"F10.wireOp",EDGE,"E5.right")])],"isStart":false})]}),makeQuery(id+"F13.opExtrude","CAP_FACE",FACE,{"disambiguationData":[OSD([sQuery(id+"F12.wireOp",EDGE,"E6.bottom"),sQuery(id+"F12.wireOp",EDGE,"E6.top"),sQuery(id+"F12.wireOp",EDGE,"E6.left"),sQuery(id+"F12.wireOp",EDGE,"E6.right")])],"isStart":false})]}),makeQuery(id+"F15.opExtrude","CAP_FACE",FACE,{"disambiguationData":[OSD([sQuery(id+"F14.wireOp",EDGE,"E7.bottom"),sQuery(id+"F14.wireOp",EDGE,"E7.top"),sQuery(id+"F14.wireOp",EDGE,"E7.left"),sQuery(id+"F14.wireOp",EDGE,"E7.right")])],"isStart":false})]}),makeQuery(id+"F51.opExtrude","CAP_FACE",FACE,{"disambiguationData":[OSD([sQuery(id+"F50.wireOp",EDGE,"E66.bottom"),sQuery(id+"F50.wireOp",EDGE,"E66.top"),sQuery(id+"F50.wireOp",EDGE,"E66.left"),sQuery(id+"F50.wireOp",EDGE,"E66.right")])],"isStart":false})]}),makeQuery(id+"F53.opExtrude","CAP_FACE",FACE,{"disambiguationData":[OSD([sQuery(id+"F52.wireOp",EDGE,"E67.bottom"),sQuery(id+"F52.wireOp",EDGE,"E67.top"),sQuery(id+"F52.wireOp",EDGE,"E67.left"),sQuery(id+"F52.wireOp",EDGE,"E67.right")])],"isStart":false})]}),makeQuery(id+"F55.opExtrude","CAP_FACE",FACE,{"disambiguationData":[OSD([sQuery(id+"F54.wireOp",EDGE,"E68.bottom"),sQuery(id+"F54.wireOp",EDGE,"E68.top"),sQuery(id+"F54.wireOp",EDGE,"E68.left"),sQuery(id+"F54.wireOp",EDGE,"E68.right")])],"isStart":false})]}),makeQuery(id+"F57.opExtrude","CAP_FACE",FACE,{"disambiguationData":[OSD([sQuery(id+"F56.wireOp",EDGE,"E69.bottom"),sQuery(id+"F56.wireOp",EDGE,"E69.top"),sQuery(id+"F56.wireOp",EDGE,"E69.left"),sQuery(id+"F56.wireOp",EDGE,"E69.right")])],"isStart":false})]}),makeQuery(id+"F59.opExtrude","CAP_FACE",FACE,{"disambiguationData":[OSD([sQuery(id+"F58.wireOp",EDGE,"E70.bottom"),sQuery(id+"F58.wireOp",EDGE,"E70.top"),sQuery(id+"F58.wireOp",EDGE,"E70.left"),sQuery(id+"F58.wireOp",EDGE,"E70.right")])],"isStart":false})]}),makeQuery(id+"F61.opExtrude","CAP_FACE",FACE,{"disambiguationData":[OSD([sQuery(id+"F60.wireOp",EDGE,"E71.bottom"),sQuery(id+"F60.wireOp",EDGE,"E71.top"),sQuery(id+"F60.wireOp",EDGE,"E71.left"),sQuery(id+"F60.wireOp",EDGE,"E71.right")])],"isStart":false})]});
            var sketch = newSketch(context, id + "F62", { "sketchPlane" : qUnion([Q0])});
            skCircle(sketch, "E72", {"center": v(32, -8) * mm, "radius": 1.3 * mm});
            skSolve(sketch);
        }
        {
            var Q0;
            Q0=makeQuery(id+"F62.imprint","IMPRINT",FACE,{"disambiguationData":[TD([[makeQuery(id+"F62.imprint","IMPRINT",EDGE,{"derivedFrom":sQuery(id+"F62.wireOp",EDGE,"E72")}),1.0]])]});
            var Q1;
            Q1=makeQuery(id+"F41.boolean.opBoolean","MERGE",FACE,{"derivedFrom":[makeQuery(id+"F39.boolean.opBoolean","MERGE",FACE,{"derivedFrom":[makeQuery(id+"F37.boolean.opBoolean","MERGE",FACE,{"derivedFrom":[makeQuery(id+"F35.boolean.opBoolean","MERGE",FACE,{"derivedFrom":[makeQuery(id+"F33.boolean.opBoolean","MERGE",FACE,{"derivedFrom":[makeQuery(id+"F7.boolean.opBoolean","MERGE",FACE,{"derivedFrom":[makeQuery(id+"F1.opExtrude","CAP_FACE",FACE,{"disambiguationData":[OSD([sQuery(id+"F0.wireOp",EDGE,"E0.rect.bottom"),sQuery(id+"F0.wireOp",EDGE,"E0.rect.top"),sQuery(id+"F0.wireOp",EDGE,"E0.rect.left"),sQuery(id+"F0.wireOp",EDGE,"E0.rect.right")])],"isStart":true}),makeQuery(id+"F7.opExtrude","CAP_FACE",FACE,{"disambiguationData":[OSD([sQuery(id+"F6.wireOp",EDGE,"E3.bottom"),sQuery(id+"F6.wireOp",EDGE,"E3.top"),sQuery(id+"F6.wireOp",EDGE,"E3.left"),sQuery(id+"F6.wireOp",EDGE,"E3.right")])],"isStart":true})]}),makeQuery(id+"F33.opExtrude","CAP_FACE",FACE,{"disambiguationData":[OSD([sQuery(id+"F32.wireOp",EDGE,"E54.bottom"),sQuery(id+"F32.wireOp",EDGE,"E54.top"),sQuery(id+"F32.wireOp",EDGE,"E54.left"),sQuery(id+"F32.wireOp",EDGE,"E54.right")])],"isStart":true})]}),makeQuery(id+"F35.opExtrude","CAP_FACE",FACE,{"disambiguationData":[OSD([sQuery(id+"F34.wireOp",EDGE,"E55.bottom"),sQuery(id+"F34.wireOp",EDGE,"E55.top"),sQuery(id+"F34.wireOp",EDGE,"E55.left"),sQuery(id+"F34.wireOp",EDGE,"E55.right")])],"isStart":true})]}),makeQuery(id+"F37.opExtrude","CAP_FACE",FACE,{"disambiguationData":[OSD([sQuery(id+"F36.wireOp",EDGE,"E56.bottom"),sQuery(id+"F36.wireOp",EDGE,"E56.top"),sQuery(id+"F36.wireOp",EDGE,"E56.left"),sQuery(id+"F36.wireOp",EDGE,"E56.right")])],"isStart":true})]}),makeQuery(id+"F39.opExtrude","CAP_FACE",FACE,{"disambiguationData":[OSD([sQuery(id+"F38.wireOp",EDGE,"E57.bottom"),sQuery(id+"F38.wireOp",EDGE,"E57.top"),sQuery(id+"F38.wireOp",EDGE,"E57.left"),sQuery(id+"F38.wireOp",EDGE,"E57.right")])],"isStart":true})]}),makeQuery(id+"F41.opExtrude","CAP_FACE",FACE,{"disambiguationData":[OSD([sQuery(id+"F40.wireOp",EDGE,"E58.bottom"),sQuery(id+"F40.wireOp",EDGE,"E58.top"),sQuery(id+"F40.wireOp",EDGE,"E58.left"),sQuery(id+"F40.wireOp",EDGE,"E58.right")])],"isStart":true})]});
            extrude(context, id + "F63", {"entities" : qUnion([Q0]), "operationType" : NewBodyOperationType.REMOVE, "oppositeDirection" : true, "endBoundEntityFace" : qUnion([Q1]), "depth" : 1.2 * mm});
        }
        {
            var Q0;
            Q0=makeQuery(id+"F61.boolean.opBoolean","MERGE",FACE,{"derivedFrom":[makeQuery(id+"F59.boolean.opBoolean","MERGE",FACE,{"derivedFrom":[makeQuery(id+"F57.boolean.opBoolean","MERGE",FACE,{"derivedFrom":[makeQuery(id+"F55.boolean.opBoolean","MERGE",FACE,{"derivedFrom":[makeQuery(id+"F53.boolean.opBoolean","MERGE",FACE,{"derivedFrom":[makeQuery(id+"F51.boolean.opBoolean","MERGE",FACE,{"derivedFrom":[makeQuery(id+"F15.boolean.opBoolean","MERGE",FACE,{"derivedFrom":[makeQuery(id+"F13.boolean.opBoolean","MERGE",FACE,{"derivedFrom":[makeQuery(id+"F11.boolean.opBoolean","MERGE",FACE,{"derivedFrom":[makeQuery(id+"F9.boolean.opBoolean","COPY",FACE,{"derivedFrom":makeQuery(id+"F9.opExtrude","CAP_FACE",FACE,{"disambiguationData":[OSD([sQuery(id+"F8.wireOp",EDGE,"E4.bottom"),sQuery(id+"F8.wireOp",EDGE,"E4.top"),sQuery(id+"F8.wireOp",EDGE,"E4.left"),sQuery(id+"F8.wireOp",EDGE,"E4.right")])],"isStart":false})}),makeQuery(id+"F11.opExtrude","CAP_FACE",FACE,{"disambiguationData":[OSD([sQuery(id+"F10.wireOp",EDGE,"E5.bottom"),sQuery(id+"F10.wireOp",EDGE,"E5.top"),sQuery(id+"F10.wireOp",EDGE,"E5.left"),sQuery(id+"F10.wireOp",EDGE,"E5.right")])],"isStart":false})]}),makeQuery(id+"F13.opExtrude","CAP_FACE",FACE,{"disambiguationData":[OSD([sQuery(id+"F12.wireOp",EDGE,"E6.bottom"),sQuery(id+"F12.wireOp",EDGE,"E6.top"),sQuery(id+"F12.wireOp",EDGE,"E6.left"),sQuery(id+"F12.wireOp",EDGE,"E6.right")])],"isStart":false})]}),makeQuery(id+"F15.opExtrude","CAP_FACE",FACE,{"disambiguationData":[OSD([sQuery(id+"F14.wireOp",EDGE,"E7.bottom"),sQuery(id+"F14.wireOp",EDGE,"E7.top"),sQuery(id+"F14.wireOp",EDGE,"E7.left"),sQuery(id+"F14.wireOp",EDGE,"E7.right")])],"isStart":false})]}),makeQuery(id+"F51.opExtrude","CAP_FACE",FACE,{"disambiguationData":[OSD([sQuery(id+"F50.wireOp",EDGE,"E66.bottom"),sQuery(id+"F50.wireOp",EDGE,"E66.top"),sQuery(id+"F50.wireOp",EDGE,"E66.left"),sQuery(id+"F50.wireOp",EDGE,"E66.right")])],"isStart":false})]}),makeQuery(id+"F53.opExtrude","CAP_FACE",FACE,{"disambiguationData":[OSD([sQuery(id+"F52.wireOp",EDGE,"E67.bottom"),sQuery(id+"F52.wireOp",EDGE,"E67.top"),sQuery(id+"F52.wireOp",EDGE,"E67.left"),sQuery(id+"F52.wireOp",EDGE,"E67.right")])],"isStart":false})]}),makeQuery(id+"F55.opExtrude","CAP_FACE",FACE,{"disambiguationData":[OSD([sQuery(id+"F54.wireOp",EDGE,"E68.bottom"),sQuery(id+"F54.wireOp",EDGE,"E68.top"),sQuery(id+"F54.wireOp",EDGE,"E68.left"),sQuery(id+"F54.wireOp",EDGE,"E68.right")])],"isStart":false})]}),makeQuery(id+"F57.opExtrude","CAP_FACE",FACE,{"disambiguationData":[OSD([sQuery(id+"F56.wireOp",EDGE,"E69.bottom"),sQuery(id+"F56.wireOp",EDGE,"E69.top"),sQuery(id+"F56.wireOp",EDGE,"E69.left"),sQuery(id+"F56.wireOp",EDGE,"E69.right")])],"isStart":false})]}),makeQuery(id+"F59.opExtrude","CAP_FACE",FACE,{"disambiguationData":[OSD([sQuery(id+"F58.wireOp",EDGE,"E70.bottom"),sQuery(id+"F58.wireOp",EDGE,"E70.top"),sQuery(id+"F58.wireOp",EDGE,"E70.left"),sQuery(id+"F58.wireOp",EDGE,"E70.right")])],"isStart":false})]}),makeQuery(id+"F61.opExtrude","CAP_FACE",FACE,{"disambiguationData":[OSD([sQuery(id+"F60.wireOp",EDGE,"E71.bottom"),sQuery(id+"F60.wireOp",EDGE,"E71.top"),sQuery(id+"F60.wireOp",EDGE,"E71.left"),sQuery(id+"F60.wireOp",EDGE,"E71.right")])],"isStart":false})]});
            var sketch = newSketch(context, id + "F64", { "sketchPlane" : qUnion([Q0])});
            skCircle(sketch, "E73", {"center": v(40.05, -7.95) * mm, "radius": 1.3 * mm});
            skSolve(sketch);
        }
        {
            var Q0;
            Q0 = qSketchRegion(id + "F64", true);
            var Q1;
            Q1=qCreatedBy(makeId("Top.planeOp"),FACE);
            extrude(context, id + "F65", {"entities" : qUnion([Q0]), "operationType" : NewBodyOperationType.REMOVE, "oppositeDirection" : true, "endBoundEntityFace" : qUnion([Q1]), "depth" : 1.2 * mm});
        }
        {
            var Q0;
            Q0=makeQuery(id+"F61.boolean.opBoolean","MERGE",FACE,{"derivedFrom":[makeQuery(id+"F59.boolean.opBoolean","MERGE",FACE,{"derivedFrom":[makeQuery(id+"F57.boolean.opBoolean","MERGE",FACE,{"derivedFrom":[makeQuery(id+"F55.boolean.opBoolean","MERGE",FACE,{"derivedFrom":[makeQuery(id+"F53.boolean.opBoolean","MERGE",FACE,{"derivedFrom":[makeQuery(id+"F51.boolean.opBoolean","MERGE",FACE,{"derivedFrom":[makeQuery(id+"F15.boolean.opBoolean","MERGE",FACE,{"derivedFrom":[makeQuery(id+"F13.boolean.opBoolean","MERGE",FACE,{"derivedFrom":[makeQuery(id+"F11.boolean.opBoolean","MERGE",FACE,{"derivedFrom":[makeQuery(id+"F9.boolean.opBoolean","COPY",FACE,{"derivedFrom":makeQuery(id+"F9.opExtrude","CAP_FACE",FACE,{"disambiguationData":[OSD([sQuery(id+"F8.wireOp",EDGE,"E4.bottom"),sQuery(id+"F8.wireOp",EDGE,"E4.top"),sQuery(id+"F8.wireOp",EDGE,"E4.left"),sQuery(id+"F8.wireOp",EDGE,"E4.right")])],"isStart":false})}),makeQuery(id+"F11.opExtrude","CAP_FACE",FACE,{"disambiguationData":[OSD([sQuery(id+"F10.wireOp",EDGE,"E5.bottom"),sQuery(id+"F10.wireOp",EDGE,"E5.top"),sQuery(id+"F10.wireOp",EDGE,"E5.left"),sQuery(id+"F10.wireOp",EDGE,"E5.right")])],"isStart":false})]}),makeQuery(id+"F13.opExtrude","CAP_FACE",FACE,{"disambiguationData":[OSD([sQuery(id+"F12.wireOp",EDGE,"E6.bottom"),sQuery(id+"F12.wireOp",EDGE,"E6.top"),sQuery(id+"F12.wireOp",EDGE,"E6.left"),sQuery(id+"F12.wireOp",EDGE,"E6.right")])],"isStart":false})]}),makeQuery(id+"F15.opExtrude","CAP_FACE",FACE,{"disambiguationData":[OSD([sQuery(id+"F14.wireOp",EDGE,"E7.bottom"),sQuery(id+"F14.wireOp",EDGE,"E7.top"),sQuery(id+"F14.wireOp",EDGE,"E7.left"),sQuery(id+"F14.wireOp",EDGE,"E7.right")])],"isStart":false})]}),makeQuery(id+"F51.opExtrude","CAP_FACE",FACE,{"disambiguationData":[OSD([sQuery(id+"F50.wireOp",EDGE,"E66.bottom"),sQuery(id+"F50.wireOp",EDGE,"E66.top"),sQuery(id+"F50.wireOp",EDGE,"E66.left"),sQuery(id+"F50.wireOp",EDGE,"E66.right")])],"isStart":false})]}),makeQuery(id+"F53.opExtrude","CAP_FACE",FACE,{"disambiguationData":[OSD([sQuery(id+"F52.wireOp",EDGE,"E67.bottom"),sQuery(id+"F52.wireOp",EDGE,"E67.top"),sQuery(id+"F52.wireOp",EDGE,"E67.left"),sQuery(id+"F52.wireOp",EDGE,"E67.right")])],"isStart":false})]}),makeQuery(id+"F55.opExtrude","CAP_FACE",FACE,{"disambiguationData":[OSD([sQuery(id+"F54.wireOp",EDGE,"E68.bottom"),sQuery(id+"F54.wireOp",EDGE,"E68.top"),sQuery(id+"F54.wireOp",EDGE,"E68.left"),sQuery(id+"F54.wireOp",EDGE,"E68.right")])],"isStart":false})]}),makeQuery(id+"F57.opExtrude","CAP_FACE",FACE,{"disambiguationData":[OSD([sQuery(id+"F56.wireOp",EDGE,"E69.bottom"),sQuery(id+"F56.wireOp",EDGE,"E69.top"),sQuery(id+"F56.wireOp",EDGE,"E69.left"),sQuery(id+"F56.wireOp",EDGE,"E69.right")])],"isStart":false})]}),makeQuery(id+"F59.opExtrude","CAP_FACE",FACE,{"disambiguationData":[OSD([sQuery(id+"F58.wireOp",EDGE,"E70.bottom"),sQuery(id+"F58.wireOp",EDGE,"E70.top"),sQuery(id+"F58.wireOp",EDGE,"E70.left"),sQuery(id+"F58.wireOp",EDGE,"E70.right")])],"isStart":false})]}),makeQuery(id+"F61.opExtrude","CAP_FACE",FACE,{"disambiguationData":[OSD([sQuery(id+"F60.wireOp",EDGE,"E71.bottom"),sQuery(id+"F60.wireOp",EDGE,"E71.top"),sQuery(id+"F60.wireOp",EDGE,"E71.left"),sQuery(id+"F60.wireOp",EDGE,"E71.right")])],"isStart":false})]});
            var sketch = newSketch(context, id + "F66", { "sketchPlane" : qUnion([Q0])});
            skCircle(sketch, "E74", {"center": v(39.92, -23.86) * mm, "radius": 1.26 * mm});
            skCircle(sketch, "E75.0.1.0", {"center": v(39.92, -15.86) * mm, "radius": 1.26 * mm});
            skLineSegment(sketch, "E75.direction1", {"start": v(39.92, -23.86) * mm, "end": v(64.92, -23.86) * mm, "construction": true});
            skLineSegment(sketch, "E75.direction2", {"start": v(39.92, -23.86) * mm, "end": v(39.92, -15.86) * mm, "construction": true});
            skSolve(sketch);
        }
        {
            var Q0;
            Q0 = qSketchRegion(id + "F66", true);
            var Q1;
            Q1=makeQuery(id+"F41.boolean.opBoolean","MERGE",FACE,{"derivedFrom":[makeQuery(id+"F39.boolean.opBoolean","MERGE",FACE,{"derivedFrom":[makeQuery(id+"F37.boolean.opBoolean","MERGE",FACE,{"derivedFrom":[makeQuery(id+"F35.boolean.opBoolean","MERGE",FACE,{"derivedFrom":[makeQuery(id+"F33.boolean.opBoolean","MERGE",FACE,{"derivedFrom":[makeQuery(id+"F7.boolean.opBoolean","MERGE",FACE,{"derivedFrom":[makeQuery(id+"F1.opExtrude","CAP_FACE",FACE,{"disambiguationData":[OSD([sQuery(id+"F0.wireOp",EDGE,"E0.rect.bottom"),sQuery(id+"F0.wireOp",EDGE,"E0.rect.top"),sQuery(id+"F0.wireOp",EDGE,"E0.rect.left"),sQuery(id+"F0.wireOp",EDGE,"E0.rect.right")])],"isStart":true}),makeQuery(id+"F7.opExtrude","CAP_FACE",FACE,{"disambiguationData":[OSD([sQuery(id+"F6.wireOp",EDGE,"E3.bottom"),sQuery(id+"F6.wireOp",EDGE,"E3.top"),sQuery(id+"F6.wireOp",EDGE,"E3.left"),sQuery(id+"F6.wireOp",EDGE,"E3.right")])],"isStart":true})]}),makeQuery(id+"F33.opExtrude","CAP_FACE",FACE,{"disambiguationData":[OSD([sQuery(id+"F32.wireOp",EDGE,"E54.bottom"),sQuery(id+"F32.wireOp",EDGE,"E54.top"),sQuery(id+"F32.wireOp",EDGE,"E54.left"),sQuery(id+"F32.wireOp",EDGE,"E54.right")])],"isStart":true})]}),makeQuery(id+"F35.opExtrude","CAP_FACE",FACE,{"disambiguationData":[OSD([sQuery(id+"F34.wireOp",EDGE,"E55.bottom"),sQuery(id+"F34.wireOp",EDGE,"E55.top"),sQuery(id+"F34.wireOp",EDGE,"E55.left"),sQuery(id+"F34.wireOp",EDGE,"E55.right")])],"isStart":true})]}),makeQuery(id+"F37.opExtrude","CAP_FACE",FACE,{"disambiguationData":[OSD([sQuery(id+"F36.wireOp",EDGE,"E56.bottom"),sQuery(id+"F36.wireOp",EDGE,"E56.top"),sQuery(id+"F36.wireOp",EDGE,"E56.left"),sQuery(id+"F36.wireOp",EDGE,"E56.right")])],"isStart":true})]}),makeQuery(id+"F39.opExtrude","CAP_FACE",FACE,{"disambiguationData":[OSD([sQuery(id+"F38.wireOp",EDGE,"E57.bottom"),sQuery(id+"F38.wireOp",EDGE,"E57.top"),sQuery(id+"F38.wireOp",EDGE,"E57.left"),sQuery(id+"F38.wireOp",EDGE,"E57.right")])],"isStart":true})]}),makeQuery(id+"F41.opExtrude","CAP_FACE",FACE,{"disambiguationData":[OSD([sQuery(id+"F40.wireOp",EDGE,"E58.bottom"),sQuery(id+"F40.wireOp",EDGE,"E58.top"),sQuery(id+"F40.wireOp",EDGE,"E58.left"),sQuery(id+"F40.wireOp",EDGE,"E58.right")])],"isStart":true})]});
            extrude(context, id + "F67", {"entities" : qUnion([Q0]), "operationType" : NewBodyOperationType.REMOVE, "oppositeDirection" : true, "endBoundEntityFace" : qUnion([Q1]), "depth" : 1.2 * mm});
        }
        {
            var Q0;
            Q0=makeQuery(id+"F61.boolean.opBoolean","MERGE",FACE,{"derivedFrom":[makeQuery(id+"F59.boolean.opBoolean","MERGE",FACE,{"derivedFrom":[makeQuery(id+"F57.boolean.opBoolean","MERGE",FACE,{"derivedFrom":[makeQuery(id+"F55.boolean.opBoolean","MERGE",FACE,{"derivedFrom":[makeQuery(id+"F53.boolean.opBoolean","MERGE",FACE,{"derivedFrom":[makeQuery(id+"F51.boolean.opBoolean","MERGE",FACE,{"derivedFrom":[makeQuery(id+"F15.boolean.opBoolean","MERGE",FACE,{"derivedFrom":[makeQuery(id+"F13.boolean.opBoolean","MERGE",FACE,{"derivedFrom":[makeQuery(id+"F11.boolean.opBoolean","MERGE",FACE,{"derivedFrom":[makeQuery(id+"F9.boolean.opBoolean","COPY",FACE,{"derivedFrom":makeQuery(id+"F9.opExtrude","CAP_FACE",FACE,{"disambiguationData":[OSD([sQuery(id+"F8.wireOp",EDGE,"E4.bottom"),sQuery(id+"F8.wireOp",EDGE,"E4.top"),sQuery(id+"F8.wireOp",EDGE,"E4.left"),sQuery(id+"F8.wireOp",EDGE,"E4.right")])],"isStart":false})}),makeQuery(id+"F11.opExtrude","CAP_FACE",FACE,{"disambiguationData":[OSD([sQuery(id+"F10.wireOp",EDGE,"E5.bottom"),sQuery(id+"F10.wireOp",EDGE,"E5.top"),sQuery(id+"F10.wireOp",EDGE,"E5.left"),sQuery(id+"F10.wireOp",EDGE,"E5.right")])],"isStart":false})]}),makeQuery(id+"F13.opExtrude","CAP_FACE",FACE,{"disambiguationData":[OSD([sQuery(id+"F12.wireOp",EDGE,"E6.bottom"),sQuery(id+"F12.wireOp",EDGE,"E6.top"),sQuery(id+"F12.wireOp",EDGE,"E6.left"),sQuery(id+"F12.wireOp",EDGE,"E6.right")])],"isStart":false})]}),makeQuery(id+"F15.opExtrude","CAP_FACE",FACE,{"disambiguationData":[OSD([sQuery(id+"F14.wireOp",EDGE,"E7.bottom"),sQuery(id+"F14.wireOp",EDGE,"E7.top"),sQuery(id+"F14.wireOp",EDGE,"E7.left"),sQuery(id+"F14.wireOp",EDGE,"E7.right")])],"isStart":false})]}),makeQuery(id+"F51.opExtrude","CAP_FACE",FACE,{"disambiguationData":[OSD([sQuery(id+"F50.wireOp",EDGE,"E66.bottom"),sQuery(id+"F50.wireOp",EDGE,"E66.top"),sQuery(id+"F50.wireOp",EDGE,"E66.left"),sQuery(id+"F50.wireOp",EDGE,"E66.right")])],"isStart":false})]}),makeQuery(id+"F53.opExtrude","CAP_FACE",FACE,{"disambiguationData":[OSD([sQuery(id+"F52.wireOp",EDGE,"E67.bottom"),sQuery(id+"F52.wireOp",EDGE,"E67.top"),sQuery(id+"F52.wireOp",EDGE,"E67.left"),sQuery(id+"F52.wireOp",EDGE,"E67.right")])],"isStart":false})]}),makeQuery(id+"F55.opExtrude","CAP_FACE",FACE,{"disambiguationData":[OSD([sQuery(id+"F54.wireOp",EDGE,"E68.bottom"),sQuery(id+"F54.wireOp",EDGE,"E68.top"),sQuery(id+"F54.wireOp",EDGE,"E68.left"),sQuery(id+"F54.wireOp",EDGE,"E68.right")])],"isStart":false})]}),makeQuery(id+"F57.opExtrude","CAP_FACE",FACE,{"disambiguationData":[OSD([sQuery(id+"F56.wireOp",EDGE,"E69.bottom"),sQuery(id+"F56.wireOp",EDGE,"E69.top"),sQuery(id+"F56.wireOp",EDGE,"E69.left"),sQuery(id+"F56.wireOp",EDGE,"E69.right")])],"isStart":false})]}),makeQuery(id+"F59.opExtrude","CAP_FACE",FACE,{"disambiguationData":[OSD([sQuery(id+"F58.wireOp",EDGE,"E70.bottom"),sQuery(id+"F58.wireOp",EDGE,"E70.top"),sQuery(id+"F58.wireOp",EDGE,"E70.left"),sQuery(id+"F58.wireOp",EDGE,"E70.right")])],"isStart":false})]}),makeQuery(id+"F61.opExtrude","CAP_FACE",FACE,{"disambiguationData":[OSD([sQuery(id+"F60.wireOp",EDGE,"E71.bottom"),sQuery(id+"F60.wireOp",EDGE,"E71.top"),sQuery(id+"F60.wireOp",EDGE,"E71.left"),sQuery(id+"F60.wireOp",EDGE,"E71.right")])],"isStart":false})]});
            var sketch = newSketch(context, id + "F68", { "sketchPlane" : qUnion([Q0])});
            skCircle(sketch, "E76", {"center": v(40.05, 15.95) * mm, "radius": 1.3 * mm});
            skCircle(sketch, "E77.1.0.0", {"center": v(32.05, 15.95) * mm, "radius": 1.3 * mm});
            skLineSegment(sketch, "E77.direction1", {"start": v(40.05, 15.95) * mm, "end": v(32.05, 15.95) * mm, "construction": true});
            skCircle(sketch, "E78.0.1.0", {"center": v(40.05, 23.95) * mm, "radius": 1.3 * mm});
            skLineSegment(sketch, "E78.direction1", {"start": v(40.05, 15.95) * mm, "end": v(65.05, 15.95) * mm, "construction": true});
            skLineSegment(sketch, "E78.direction2", {"start": v(40.05, 15.95) * mm, "end": v(40.05, 23.95) * mm, "construction": true});
            skSolve(sketch);
        }
        {
            var Q0;
            Q0 = qSketchRegion(id + "F68", true);
            var Q1;
            Q1=qCreatedBy(makeId("Top.planeOp"),FACE);
            extrude(context, id + "F69", {"entities" : qUnion([Q0]), "operationType" : NewBodyOperationType.REMOVE, "oppositeDirection" : true, "endBoundEntityFace" : qUnion([Q1]), "depth" : 1.2 * mm});
        }
        {
            var Q0;
            Q0=makeQuery(id+"F24.imprint","IMPRINT",FACE,{"disambiguationData":[TD([[makeQuery(id+"F24.imprint","IMPRINT",EDGE,{"derivedFrom":sQuery(id+"F24.wireOp",EDGE,"E15")}),-1.0]])]});
            var sketch = newSketch(context, id + "F70", { "sketchPlane" : qUnion([Q0])});
            skCircle(sketch, "E79", {"center": v(-12.05, 20.05) * mm, "radius": 3.25 * mm});
            skCircle(sketch, "E80.0.1.0", {"center": v(-12.05, 12.05) * mm, "radius": 3.25 * mm});
            skCircle(sketch, "E80.0.2.0", {"center": v(-12.05, 4.05) * mm, "radius": 3.25 * mm});
            skCircle(sketch, "E80.0.3.0", {"center": v(-12.05, -3.95) * mm, "radius": 3.25 * mm});
            skCircle(sketch, "E80.0.4.0", {"center": v(-12.05, -11.95) * mm, "radius": 3.25 * mm});
            skCircle(sketch, "E80.0.5.0", {"center": v(-12.05, -19.95) * mm, "radius": 3.25 * mm});
            skCircle(sketch, "E80.1.0.0", {"center": v(11.95, 20.05) * mm, "radius": 3.25 * mm});
            skCircle(sketch, "E80.1.1.0", {"center": v(11.95, 12.05) * mm, "radius": 3.25 * mm});
            skCircle(sketch, "E80.1.2.0", {"center": v(11.95, 4.05) * mm, "radius": 3.25 * mm});
            skCircle(sketch, "E80.1.3.0", {"center": v(11.95, -3.95) * mm, "radius": 3.25 * mm});
            skCircle(sketch, "E80.1.4.0", {"center": v(11.95, -11.95) * mm, "radius": 3.25 * mm});
            skCircle(sketch, "E80.1.5.0", {"center": v(11.95, -19.95) * mm, "radius": 3.25 * mm});
            skLineSegment(sketch, "E80.direction1", {"start": v(-12.05, 20.05) * mm, "end": v(11.95, 20.05) * mm, "construction": true});
            skLineSegment(sketch, "E80.direction2", {"start": v(-12.05, 20.05) * mm, "end": v(-12.05, 12.05) * mm, "construction": true});
            skSolve(sketch);
        }
        {
            var Q0;
            Q0 = qSketchRegion(id + "F70", true);
            var Q1;
            Q1=qCreatedBy(makeId("Top.planeOp"),FACE);
            extrude(context, id + "F71", {"entities" : qUnion([Q0]), "operationType" : NewBodyOperationType.ADD, "endBound" : BoundingType.UP_TO_SURFACE, "endBoundEntityFace" : qUnion([Q1]), "depth" : 25 * mm});
        }
        {
            var Q0;
            Q0=qCreatedBy(makeId("Top.planeOp"),FACE);
            var sketch = newSketch(context, id + "F72", { "sketchPlane" : qUnion([Q0])});
            skCircle(sketch, "E81", {"center": v(-12.05, -20.05) * mm, "radius": 2.4 * mm});
            skCircle(sketch, "E82.0.1.0", {"center": v(-12.05, -12.05) * mm, "radius": 2.4 * mm});
            skCircle(sketch, "E82.0.2.0", {"center": v(-12.05, -4.05) * mm, "radius": 2.4 * mm});
            skCircle(sketch, "E82.0.3.0", {"center": v(-12.05, 3.95) * mm, "radius": 2.4 * mm});
            skCircle(sketch, "E82.0.4.0", {"center": v(-12.05, 11.95) * mm, "radius": 2.4 * mm});
            skCircle(sketch, "E82.0.5.0", {"center": v(-12.05, 19.95) * mm, "radius": 2.4 * mm});
            skCircle(sketch, "E82.1.0.0", {"center": v(11.95, -20.05) * mm, "radius": 2.4 * mm});
            skCircle(sketch, "E82.1.1.0", {"center": v(11.95, -12.05) * mm, "radius": 2.4 * mm});
            skCircle(sketch, "E82.1.2.0", {"center": v(11.95, -4.05) * mm, "radius": 2.4 * mm});
            skCircle(sketch, "E82.1.3.0", {"center": v(11.95, 3.95) * mm, "radius": 2.4 * mm});
            skCircle(sketch, "E82.1.4.0", {"center": v(11.95, 11.95) * mm, "radius": 2.4 * mm});
            skCircle(sketch, "E82.1.5.0", {"center": v(11.95, 19.95) * mm, "radius": 2.4 * mm});
            skLineSegment(sketch, "E82.direction1", {"start": v(-12.05, -20.05) * mm, "end": v(11.95, -20.05) * mm, "construction": true});
            skLineSegment(sketch, "E82.direction2", {"start": v(-12.05, -20.05) * mm, "end": v(-12.05, -12.05) * mm, "construction": true});
            skSolve(sketch);
        }
        {
            var Q0;
            Q0 = qSketchRegion(id + "F72", true);
            var Q1;
            Q1=makeQuery(id+"F61.boolean.opBoolean","MERGE",FACE,{"derivedFrom":[makeQuery(id+"F59.boolean.opBoolean","MERGE",FACE,{"derivedFrom":[makeQuery(id+"F57.boolean.opBoolean","MERGE",FACE,{"derivedFrom":[makeQuery(id+"F55.boolean.opBoolean","MERGE",FACE,{"derivedFrom":[makeQuery(id+"F53.boolean.opBoolean","MERGE",FACE,{"derivedFrom":[makeQuery(id+"F51.boolean.opBoolean","MERGE",FACE,{"derivedFrom":[makeQuery(id+"F15.boolean.opBoolean","MERGE",FACE,{"derivedFrom":[makeQuery(id+"F13.boolean.opBoolean","MERGE",FACE,{"derivedFrom":[makeQuery(id+"F11.boolean.opBoolean","MERGE",FACE,{"derivedFrom":[makeQuery(id+"F9.boolean.opBoolean","COPY",FACE,{"derivedFrom":makeQuery(id+"F9.opExtrude","CAP_FACE",FACE,{"disambiguationData":[OSD([sQuery(id+"F8.wireOp",EDGE,"E4.bottom"),sQuery(id+"F8.wireOp",EDGE,"E4.top"),sQuery(id+"F8.wireOp",EDGE,"E4.left"),sQuery(id+"F8.wireOp",EDGE,"E4.right")])],"isStart":false})}),makeQuery(id+"F11.opExtrude","CAP_FACE",FACE,{"disambiguationData":[OSD([sQuery(id+"F10.wireOp",EDGE,"E5.bottom"),sQuery(id+"F10.wireOp",EDGE,"E5.top"),sQuery(id+"F10.wireOp",EDGE,"E5.left"),sQuery(id+"F10.wireOp",EDGE,"E5.right")])],"isStart":false})]}),makeQuery(id+"F13.opExtrude","CAP_FACE",FACE,{"disambiguationData":[OSD([sQuery(id+"F12.wireOp",EDGE,"E6.bottom"),sQuery(id+"F12.wireOp",EDGE,"E6.top"),sQuery(id+"F12.wireOp",EDGE,"E6.left"),sQuery(id+"F12.wireOp",EDGE,"E6.right")])],"isStart":false})]}),makeQuery(id+"F15.opExtrude","CAP_FACE",FACE,{"disambiguationData":[OSD([sQuery(id+"F14.wireOp",EDGE,"E7.bottom"),sQuery(id+"F14.wireOp",EDGE,"E7.top"),sQuery(id+"F14.wireOp",EDGE,"E7.left"),sQuery(id+"F14.wireOp",EDGE,"E7.right")])],"isStart":false})]}),makeQuery(id+"F51.opExtrude","CAP_FACE",FACE,{"disambiguationData":[OSD([sQuery(id+"F50.wireOp",EDGE,"E66.bottom"),sQuery(id+"F50.wireOp",EDGE,"E66.top"),sQuery(id+"F50.wireOp",EDGE,"E66.left"),sQuery(id+"F50.wireOp",EDGE,"E66.right")])],"isStart":false})]}),makeQuery(id+"F53.opExtrude","CAP_FACE",FACE,{"disambiguationData":[OSD([sQuery(id+"F52.wireOp",EDGE,"E67.bottom"),sQuery(id+"F52.wireOp",EDGE,"E67.top"),sQuery(id+"F52.wireOp",EDGE,"E67.left"),sQuery(id+"F52.wireOp",EDGE,"E67.right")])],"isStart":false})]}),makeQuery(id+"F55.opExtrude","CAP_FACE",FACE,{"disambiguationData":[OSD([sQuery(id+"F54.wireOp",EDGE,"E68.bottom"),sQuery(id+"F54.wireOp",EDGE,"E68.top"),sQuery(id+"F54.wireOp",EDGE,"E68.left"),sQuery(id+"F54.wireOp",EDGE,"E68.right")])],"isStart":false})]}),makeQuery(id+"F57.opExtrude","CAP_FACE",FACE,{"disambiguationData":[OSD([sQuery(id+"F56.wireOp",EDGE,"E69.bottom"),sQuery(id+"F56.wireOp",EDGE,"E69.top"),sQuery(id+"F56.wireOp",EDGE,"E69.left"),sQuery(id+"F56.wireOp",EDGE,"E69.right")])],"isStart":false})]}),makeQuery(id+"F59.opExtrude","CAP_FACE",FACE,{"disambiguationData":[OSD([sQuery(id+"F58.wireOp",EDGE,"E70.bottom"),sQuery(id+"F58.wireOp",EDGE,"E70.top"),sQuery(id+"F58.wireOp",EDGE,"E70.left"),sQuery(id+"F58.wireOp",EDGE,"E70.right")])],"isStart":false})]}),makeQuery(id+"F61.opExtrude","CAP_FACE",FACE,{"disambiguationData":[OSD([sQuery(id+"F60.wireOp",EDGE,"E71.bottom"),sQuery(id+"F60.wireOp",EDGE,"E71.top"),sQuery(id+"F60.wireOp",EDGE,"E71.left"),sQuery(id+"F60.wireOp",EDGE,"E71.right")])],"isStart":false})]});
            extrude(context, id + "F73", {"entities" : qUnion([Q0]), "operationType" : NewBodyOperationType.REMOVE, "endBound" : BoundingType.UP_TO_SURFACE, "endBoundEntityFace" : qUnion([Q1]), "depth" : 25 * mm});
        }
        {
            var Q0;
            Q0=makeQuery(id+"F24.imprint","IMPRINT",FACE,{"disambiguationData":[TD([[makeQuery(id+"F24.imprint","IMPRINT",EDGE,{"derivedFrom":sQuery(id+"F24.wireOp",EDGE,"E15")}),-1.0]])]});
            var sketch = newSketch(context, id + "F74", { "sketchPlane" : qUnion([Q0])});
            skCircle(sketch, "E83", {"center": v(20, 4) * mm, "radius": 3.25 * mm});
            skCircle(sketch, "E84.1.0.0", {"center": v(28, 4) * mm, "radius": 3.25 * mm});
            skLineSegment(sketch, "E84.direction1", {"start": v(20, 4) * mm, "end": v(28, 4) * mm, "construction": true});
            skSolve(sketch);
        }
        {
            var Q0;
            Q0 = qSketchRegion(id + "F74", true);
            var Q1;
            Q1=makeQuery(id+"F41.boolean.opBoolean","MERGE",FACE,{"derivedFrom":[makeQuery(id+"F39.boolean.opBoolean","MERGE",FACE,{"derivedFrom":[makeQuery(id+"F37.boolean.opBoolean","MERGE",FACE,{"derivedFrom":[makeQuery(id+"F35.boolean.opBoolean","MERGE",FACE,{"derivedFrom":[makeQuery(id+"F33.boolean.opBoolean","MERGE",FACE,{"derivedFrom":[makeQuery(id+"F7.boolean.opBoolean","MERGE",FACE,{"derivedFrom":[makeQuery(id+"F1.opExtrude","CAP_FACE",FACE,{"disambiguationData":[OSD([sQuery(id+"F0.wireOp",EDGE,"E0.rect.bottom"),sQuery(id+"F0.wireOp",EDGE,"E0.rect.top"),sQuery(id+"F0.wireOp",EDGE,"E0.rect.left"),sQuery(id+"F0.wireOp",EDGE,"E0.rect.right")])],"isStart":true}),makeQuery(id+"F7.opExtrude","CAP_FACE",FACE,{"disambiguationData":[OSD([sQuery(id+"F6.wireOp",EDGE,"E3.bottom"),sQuery(id+"F6.wireOp",EDGE,"E3.top"),sQuery(id+"F6.wireOp",EDGE,"E3.left"),sQuery(id+"F6.wireOp",EDGE,"E3.right")])],"isStart":true})]}),makeQuery(id+"F33.opExtrude","CAP_FACE",FACE,{"disambiguationData":[OSD([sQuery(id+"F32.wireOp",EDGE,"E54.bottom"),sQuery(id+"F32.wireOp",EDGE,"E54.top"),sQuery(id+"F32.wireOp",EDGE,"E54.left"),sQuery(id+"F32.wireOp",EDGE,"E54.right")])],"isStart":true})]}),makeQuery(id+"F35.opExtrude","CAP_FACE",FACE,{"disambiguationData":[OSD([sQuery(id+"F34.wireOp",EDGE,"E55.bottom"),sQuery(id+"F34.wireOp",EDGE,"E55.top"),sQuery(id+"F34.wireOp",EDGE,"E55.left"),sQuery(id+"F34.wireOp",EDGE,"E55.right")])],"isStart":true})]}),makeQuery(id+"F37.opExtrude","CAP_FACE",FACE,{"disambiguationData":[OSD([sQuery(id+"F36.wireOp",EDGE,"E56.bottom"),sQuery(id+"F36.wireOp",EDGE,"E56.top"),sQuery(id+"F36.wireOp",EDGE,"E56.left"),sQuery(id+"F36.wireOp",EDGE,"E56.right")])],"isStart":true})]}),makeQuery(id+"F39.opExtrude","CAP_FACE",FACE,{"disambiguationData":[OSD([sQuery(id+"F38.wireOp",EDGE,"E57.bottom"),sQuery(id+"F38.wireOp",EDGE,"E57.top"),sQuery(id+"F38.wireOp",EDGE,"E57.left"),sQuery(id+"F38.wireOp",EDGE,"E57.right")])],"isStart":true})]}),makeQuery(id+"F41.opExtrude","CAP_FACE",FACE,{"disambiguationData":[OSD([sQuery(id+"F40.wireOp",EDGE,"E58.bottom"),sQuery(id+"F40.wireOp",EDGE,"E58.top"),sQuery(id+"F40.wireOp",EDGE,"E58.left"),sQuery(id+"F40.wireOp",EDGE,"E58.right")])],"isStart":true})]});
            extrude(context, id + "F75", {"entities" : qUnion([Q0]), "operationType" : NewBodyOperationType.ADD, "endBound" : BoundingType.UP_TO_SURFACE, "endBoundEntityFace" : qUnion([Q1]), "depth" : 25 * mm});
        }
        {
            var Q0;
            Q0=makeQuery(id+"F75.opExtrude","CAP_FACE",FACE,{"disambiguationData":[OSD([sQuery(id+"F74.wireOp",EDGE,"E83")])],"isStart":false});
            var sketch = newSketch(context, id + "F76", { "sketchPlane" : qUnion([Q0])});
            skCircle(sketch, "E85", {"center": v(20, 4) * mm, "radius": 2.4 * mm});
            skCircle(sketch, "E86.1.0.0", {"center": v(28, 4) * mm, "radius": 2.4 * mm});
            skLineSegment(sketch, "E86.direction1", {"start": v(20, 4) * mm, "end": v(28, 4) * mm, "construction": true});
            skSolve(sketch);
        }
        {
            var Q0;
            Q0 = qSketchRegion(id + "F76", true);
            var Q1;
            Q1=makeQuery(id+"F61.boolean.opBoolean","MERGE",FACE,{"derivedFrom":[makeQuery(id+"F59.boolean.opBoolean","MERGE",FACE,{"derivedFrom":[makeQuery(id+"F57.boolean.opBoolean","MERGE",FACE,{"derivedFrom":[makeQuery(id+"F55.boolean.opBoolean","MERGE",FACE,{"derivedFrom":[makeQuery(id+"F53.boolean.opBoolean","MERGE",FACE,{"derivedFrom":[makeQuery(id+"F51.boolean.opBoolean","MERGE",FACE,{"derivedFrom":[makeQuery(id+"F15.boolean.opBoolean","MERGE",FACE,{"derivedFrom":[makeQuery(id+"F13.boolean.opBoolean","MERGE",FACE,{"derivedFrom":[makeQuery(id+"F11.boolean.opBoolean","MERGE",FACE,{"derivedFrom":[makeQuery(id+"F9.boolean.opBoolean","COPY",FACE,{"derivedFrom":makeQuery(id+"F9.opExtrude","CAP_FACE",FACE,{"disambiguationData":[OSD([sQuery(id+"F8.wireOp",EDGE,"E4.bottom"),sQuery(id+"F8.wireOp",EDGE,"E4.top"),sQuery(id+"F8.wireOp",EDGE,"E4.left"),sQuery(id+"F8.wireOp",EDGE,"E4.right")])],"isStart":false})}),makeQuery(id+"F11.opExtrude","CAP_FACE",FACE,{"disambiguationData":[OSD([sQuery(id+"F10.wireOp",EDGE,"E5.bottom"),sQuery(id+"F10.wireOp",EDGE,"E5.top"),sQuery(id+"F10.wireOp",EDGE,"E5.left"),sQuery(id+"F10.wireOp",EDGE,"E5.right")])],"isStart":false})]}),makeQuery(id+"F13.opExtrude","CAP_FACE",FACE,{"disambiguationData":[OSD([sQuery(id+"F12.wireOp",EDGE,"E6.bottom"),sQuery(id+"F12.wireOp",EDGE,"E6.top"),sQuery(id+"F12.wireOp",EDGE,"E6.left"),sQuery(id+"F12.wireOp",EDGE,"E6.right")])],"isStart":false})]}),makeQuery(id+"F15.opExtrude","CAP_FACE",FACE,{"disambiguationData":[OSD([sQuery(id+"F14.wireOp",EDGE,"E7.bottom"),sQuery(id+"F14.wireOp",EDGE,"E7.top"),sQuery(id+"F14.wireOp",EDGE,"E7.left"),sQuery(id+"F14.wireOp",EDGE,"E7.right")])],"isStart":false})]}),makeQuery(id+"F51.opExtrude","CAP_FACE",FACE,{"disambiguationData":[OSD([sQuery(id+"F50.wireOp",EDGE,"E66.bottom"),sQuery(id+"F50.wireOp",EDGE,"E66.top"),sQuery(id+"F50.wireOp",EDGE,"E66.left"),sQuery(id+"F50.wireOp",EDGE,"E66.right")])],"isStart":false})]}),makeQuery(id+"F53.opExtrude","CAP_FACE",FACE,{"disambiguationData":[OSD([sQuery(id+"F52.wireOp",EDGE,"E67.bottom"),sQuery(id+"F52.wireOp",EDGE,"E67.top"),sQuery(id+"F52.wireOp",EDGE,"E67.left"),sQuery(id+"F52.wireOp",EDGE,"E67.right")])],"isStart":false})]}),makeQuery(id+"F55.opExtrude","CAP_FACE",FACE,{"disambiguationData":[OSD([sQuery(id+"F54.wireOp",EDGE,"E68.bottom"),sQuery(id+"F54.wireOp",EDGE,"E68.top"),sQuery(id+"F54.wireOp",EDGE,"E68.left"),sQuery(id+"F54.wireOp",EDGE,"E68.right")])],"isStart":false})]}),makeQuery(id+"F57.opExtrude","CAP_FACE",FACE,{"disambiguationData":[OSD([sQuery(id+"F56.wireOp",EDGE,"E69.bottom"),sQuery(id+"F56.wireOp",EDGE,"E69.top"),sQuery(id+"F56.wireOp",EDGE,"E69.left"),sQuery(id+"F56.wireOp",EDGE,"E69.right")])],"isStart":false})]}),makeQuery(id+"F59.opExtrude","CAP_FACE",FACE,{"disambiguationData":[OSD([sQuery(id+"F58.wireOp",EDGE,"E70.bottom"),sQuery(id+"F58.wireOp",EDGE,"E70.top"),sQuery(id+"F58.wireOp",EDGE,"E70.left"),sQuery(id+"F58.wireOp",EDGE,"E70.right")])],"isStart":false})]}),makeQuery(id+"F61.opExtrude","CAP_FACE",FACE,{"disambiguationData":[OSD([sQuery(id+"F60.wireOp",EDGE,"E71.bottom"),sQuery(id+"F60.wireOp",EDGE,"E71.top"),sQuery(id+"F60.wireOp",EDGE,"E71.left"),sQuery(id+"F60.wireOp",EDGE,"E71.right")])],"isStart":false})]});
            extrude(context, id + "F77", {"entities" : qUnion([Q0]), "operationType" : NewBodyOperationType.REMOVE, "endBound" : BoundingType.UP_TO_SURFACE, "oppositeDirection" : true, "endBoundEntityFace" : qUnion([Q1]), "depth" : 25 * mm});
        }
        {
            var Q0;
            Q0=makeQuery(id+"F61.boolean.opBoolean","MERGE",FACE,{"derivedFrom":[makeQuery(id+"F59.boolean.opBoolean","MERGE",FACE,{"derivedFrom":[makeQuery(id+"F57.boolean.opBoolean","MERGE",FACE,{"derivedFrom":[makeQuery(id+"F55.boolean.opBoolean","MERGE",FACE,{"derivedFrom":[makeQuery(id+"F53.boolean.opBoolean","MERGE",FACE,{"derivedFrom":[makeQuery(id+"F51.boolean.opBoolean","MERGE",FACE,{"derivedFrom":[makeQuery(id+"F15.boolean.opBoolean","MERGE",FACE,{"derivedFrom":[makeQuery(id+"F13.boolean.opBoolean","MERGE",FACE,{"derivedFrom":[makeQuery(id+"F11.boolean.opBoolean","MERGE",FACE,{"derivedFrom":[makeQuery(id+"F9.boolean.opBoolean","COPY",FACE,{"derivedFrom":makeQuery(id+"F9.opExtrude","CAP_FACE",FACE,{"disambiguationData":[OSD([sQuery(id+"F8.wireOp",EDGE,"E4.bottom"),sQuery(id+"F8.wireOp",EDGE,"E4.top"),sQuery(id+"F8.wireOp",EDGE,"E4.left"),sQuery(id+"F8.wireOp",EDGE,"E4.right")])],"isStart":false})}),makeQuery(id+"F11.opExtrude","CAP_FACE",FACE,{"disambiguationData":[OSD([sQuery(id+"F10.wireOp",EDGE,"E5.bottom"),sQuery(id+"F10.wireOp",EDGE,"E5.top"),sQuery(id+"F10.wireOp",EDGE,"E5.left"),sQuery(id+"F10.wireOp",EDGE,"E5.right")])],"isStart":false})]}),makeQuery(id+"F13.opExtrude","CAP_FACE",FACE,{"disambiguationData":[OSD([sQuery(id+"F12.wireOp",EDGE,"E6.bottom"),sQuery(id+"F12.wireOp",EDGE,"E6.top"),sQuery(id+"F12.wireOp",EDGE,"E6.left"),sQuery(id+"F12.wireOp",EDGE,"E6.right")])],"isStart":false})]}),makeQuery(id+"F15.opExtrude","CAP_FACE",FACE,{"disambiguationData":[OSD([sQuery(id+"F14.wireOp",EDGE,"E7.bottom"),sQuery(id+"F14.wireOp",EDGE,"E7.top"),sQuery(id+"F14.wireOp",EDGE,"E7.left"),sQuery(id+"F14.wireOp",EDGE,"E7.right")])],"isStart":false})]}),makeQuery(id+"F51.opExtrude","CAP_FACE",FACE,{"disambiguationData":[OSD([sQuery(id+"F50.wireOp",EDGE,"E66.bottom"),sQuery(id+"F50.wireOp",EDGE,"E66.top"),sQuery(id+"F50.wireOp",EDGE,"E66.left"),sQuery(id+"F50.wireOp",EDGE,"E66.right")])],"isStart":false})]}),makeQuery(id+"F53.opExtrude","CAP_FACE",FACE,{"disambiguationData":[OSD([sQuery(id+"F52.wireOp",EDGE,"E67.bottom"),sQuery(id+"F52.wireOp",EDGE,"E67.top"),sQuery(id+"F52.wireOp",EDGE,"E67.left"),sQuery(id+"F52.wireOp",EDGE,"E67.right")])],"isStart":false})]}),makeQuery(id+"F55.opExtrude","CAP_FACE",FACE,{"disambiguationData":[OSD([sQuery(id+"F54.wireOp",EDGE,"E68.bottom"),sQuery(id+"F54.wireOp",EDGE,"E68.top"),sQuery(id+"F54.wireOp",EDGE,"E68.left"),sQuery(id+"F54.wireOp",EDGE,"E68.right")])],"isStart":false})]}),makeQuery(id+"F57.opExtrude","CAP_FACE",FACE,{"disambiguationData":[OSD([sQuery(id+"F56.wireOp",EDGE,"E69.bottom"),sQuery(id+"F56.wireOp",EDGE,"E69.top"),sQuery(id+"F56.wireOp",EDGE,"E69.left"),sQuery(id+"F56.wireOp",EDGE,"E69.right")])],"isStart":false})]}),makeQuery(id+"F59.opExtrude","CAP_FACE",FACE,{"disambiguationData":[OSD([sQuery(id+"F58.wireOp",EDGE,"E70.bottom"),sQuery(id+"F58.wireOp",EDGE,"E70.top"),sQuery(id+"F58.wireOp",EDGE,"E70.left"),sQuery(id+"F58.wireOp",EDGE,"E70.right")])],"isStart":false})]}),makeQuery(id+"F61.opExtrude","CAP_FACE",FACE,{"disambiguationData":[OSD([sQuery(id+"F60.wireOp",EDGE,"E71.bottom"),sQuery(id+"F60.wireOp",EDGE,"E71.top"),sQuery(id+"F60.wireOp",EDGE,"E71.left"),sQuery(id+"F60.wireOp",EDGE,"E71.right")])],"isStart":false})]});
            var sketch = newSketch(context, id + "F78", { "sketchPlane" : qUnion([Q0])});
            skCircle(sketch, "E87", {"center": v(36, 16) * mm, "radius": 1.6 * mm});
            skSolve(sketch);
        }
        {
            var Q0;
            Q0 = qSketchRegion(id + "F78", true);
            var Q1;
            Q1=makeQuery(id+"F41.boolean.opBoolean","MERGE",FACE,{"derivedFrom":[makeQuery(id+"F39.boolean.opBoolean","MERGE",FACE,{"derivedFrom":[makeQuery(id+"F37.boolean.opBoolean","MERGE",FACE,{"derivedFrom":[makeQuery(id+"F35.boolean.opBoolean","MERGE",FACE,{"derivedFrom":[makeQuery(id+"F33.boolean.opBoolean","MERGE",FACE,{"derivedFrom":[makeQuery(id+"F7.boolean.opBoolean","MERGE",FACE,{"derivedFrom":[makeQuery(id+"F1.opExtrude","CAP_FACE",FACE,{"disambiguationData":[OSD([sQuery(id+"F0.wireOp",EDGE,"E0.rect.bottom"),sQuery(id+"F0.wireOp",EDGE,"E0.rect.top"),sQuery(id+"F0.wireOp",EDGE,"E0.rect.left"),sQuery(id+"F0.wireOp",EDGE,"E0.rect.right")])],"isStart":true}),makeQuery(id+"F7.opExtrude","CAP_FACE",FACE,{"disambiguationData":[OSD([sQuery(id+"F6.wireOp",EDGE,"E3.bottom"),sQuery(id+"F6.wireOp",EDGE,"E3.top"),sQuery(id+"F6.wireOp",EDGE,"E3.left"),sQuery(id+"F6.wireOp",EDGE,"E3.right")])],"isStart":true})]}),makeQuery(id+"F33.opExtrude","CAP_FACE",FACE,{"disambiguationData":[OSD([sQuery(id+"F32.wireOp",EDGE,"E54.bottom"),sQuery(id+"F32.wireOp",EDGE,"E54.top"),sQuery(id+"F32.wireOp",EDGE,"E54.left"),sQuery(id+"F32.wireOp",EDGE,"E54.right")])],"isStart":true})]}),makeQuery(id+"F35.opExtrude","CAP_FACE",FACE,{"disambiguationData":[OSD([sQuery(id+"F34.wireOp",EDGE,"E55.bottom"),sQuery(id+"F34.wireOp",EDGE,"E55.top"),sQuery(id+"F34.wireOp",EDGE,"E55.left"),sQuery(id+"F34.wireOp",EDGE,"E55.right")])],"isStart":true})]}),makeQuery(id+"F37.opExtrude","CAP_FACE",FACE,{"disambiguationData":[OSD([sQuery(id+"F36.wireOp",EDGE,"E56.bottom"),sQuery(id+"F36.wireOp",EDGE,"E56.top"),sQuery(id+"F36.wireOp",EDGE,"E56.left"),sQuery(id+"F36.wireOp",EDGE,"E56.right")])],"isStart":true})]}),makeQuery(id+"F39.opExtrude","CAP_FACE",FACE,{"disambiguationData":[OSD([sQuery(id+"F38.wireOp",EDGE,"E57.bottom"),sQuery(id+"F38.wireOp",EDGE,"E57.top"),sQuery(id+"F38.wireOp",EDGE,"E57.left"),sQuery(id+"F38.wireOp",EDGE,"E57.right")])],"isStart":true})]}),makeQuery(id+"F41.opExtrude","CAP_FACE",FACE,{"disambiguationData":[OSD([sQuery(id+"F40.wireOp",EDGE,"E58.bottom"),sQuery(id+"F40.wireOp",EDGE,"E58.top"),sQuery(id+"F40.wireOp",EDGE,"E58.left"),sQuery(id+"F40.wireOp",EDGE,"E58.right")])],"isStart":true})]});
            extrude(context, id + "F79", {"entities" : qUnion([Q0]), "operationType" : NewBodyOperationType.ADD, "endBound" : BoundingType.UP_TO_SURFACE, "endBoundEntityFace" : qUnion([Q1]), "depth" : 25 * mm});
        }
        {
            var Q0;
            Q0=makeQuery(id+"F61.boolean.opBoolean","MERGE",FACE,{"derivedFrom":[makeQuery(id+"F59.boolean.opBoolean","MERGE",FACE,{"derivedFrom":[makeQuery(id+"F57.boolean.opBoolean","MERGE",FACE,{"derivedFrom":[makeQuery(id+"F55.boolean.opBoolean","MERGE",FACE,{"derivedFrom":[makeQuery(id+"F53.boolean.opBoolean","MERGE",FACE,{"derivedFrom":[makeQuery(id+"F51.boolean.opBoolean","MERGE",FACE,{"derivedFrom":[makeQuery(id+"F15.boolean.opBoolean","MERGE",FACE,{"derivedFrom":[makeQuery(id+"F13.boolean.opBoolean","MERGE",FACE,{"derivedFrom":[makeQuery(id+"F11.boolean.opBoolean","MERGE",FACE,{"derivedFrom":[makeQuery(id+"F9.boolean.opBoolean","COPY",FACE,{"derivedFrom":makeQuery(id+"F9.opExtrude","CAP_FACE",FACE,{"disambiguationData":[OSD([sQuery(id+"F8.wireOp",EDGE,"E4.bottom"),sQuery(id+"F8.wireOp",EDGE,"E4.top"),sQuery(id+"F8.wireOp",EDGE,"E4.left"),sQuery(id+"F8.wireOp",EDGE,"E4.right")])],"isStart":false})}),makeQuery(id+"F11.opExtrude","CAP_FACE",FACE,{"disambiguationData":[OSD([sQuery(id+"F10.wireOp",EDGE,"E5.bottom"),sQuery(id+"F10.wireOp",EDGE,"E5.top"),sQuery(id+"F10.wireOp",EDGE,"E5.left"),sQuery(id+"F10.wireOp",EDGE,"E5.right")])],"isStart":false})]}),makeQuery(id+"F13.opExtrude","CAP_FACE",FACE,{"disambiguationData":[OSD([sQuery(id+"F12.wireOp",EDGE,"E6.bottom"),sQuery(id+"F12.wireOp",EDGE,"E6.top"),sQuery(id+"F12.wireOp",EDGE,"E6.left"),sQuery(id+"F12.wireOp",EDGE,"E6.right")])],"isStart":false})]}),makeQuery(id+"F15.opExtrude","CAP_FACE",FACE,{"disambiguationData":[OSD([sQuery(id+"F14.wireOp",EDGE,"E7.bottom"),sQuery(id+"F14.wireOp",EDGE,"E7.top"),sQuery(id+"F14.wireOp",EDGE,"E7.left"),sQuery(id+"F14.wireOp",EDGE,"E7.right")])],"isStart":false})]}),makeQuery(id+"F51.opExtrude","CAP_FACE",FACE,{"disambiguationData":[OSD([sQuery(id+"F50.wireOp",EDGE,"E66.bottom"),sQuery(id+"F50.wireOp",EDGE,"E66.top"),sQuery(id+"F50.wireOp",EDGE,"E66.left"),sQuery(id+"F50.wireOp",EDGE,"E66.right")])],"isStart":false})]}),makeQuery(id+"F53.opExtrude","CAP_FACE",FACE,{"disambiguationData":[OSD([sQuery(id+"F52.wireOp",EDGE,"E67.bottom"),sQuery(id+"F52.wireOp",EDGE,"E67.top"),sQuery(id+"F52.wireOp",EDGE,"E67.left"),sQuery(id+"F52.wireOp",EDGE,"E67.right")])],"isStart":false})]}),makeQuery(id+"F55.opExtrude","CAP_FACE",FACE,{"disambiguationData":[OSD([sQuery(id+"F54.wireOp",EDGE,"E68.bottom"),sQuery(id+"F54.wireOp",EDGE,"E68.top"),sQuery(id+"F54.wireOp",EDGE,"E68.left"),sQuery(id+"F54.wireOp",EDGE,"E68.right")])],"isStart":false})]}),makeQuery(id+"F57.opExtrude","CAP_FACE",FACE,{"disambiguationData":[OSD([sQuery(id+"F56.wireOp",EDGE,"E69.bottom"),sQuery(id+"F56.wireOp",EDGE,"E69.top"),sQuery(id+"F56.wireOp",EDGE,"E69.left"),sQuery(id+"F56.wireOp",EDGE,"E69.right")])],"isStart":false})]}),makeQuery(id+"F59.opExtrude","CAP_FACE",FACE,{"disambiguationData":[OSD([sQuery(id+"F58.wireOp",EDGE,"E70.bottom"),sQuery(id+"F58.wireOp",EDGE,"E70.top"),sQuery(id+"F58.wireOp",EDGE,"E70.left"),sQuery(id+"F58.wireOp",EDGE,"E70.right")])],"isStart":false})]}),makeQuery(id+"F61.opExtrude","CAP_FACE",FACE,{"disambiguationData":[OSD([sQuery(id+"F60.wireOp",EDGE,"E71.bottom"),sQuery(id+"F60.wireOp",EDGE,"E71.top"),sQuery(id+"F60.wireOp",EDGE,"E71.left"),sQuery(id+"F60.wireOp",EDGE,"E71.right")])],"isStart":false})]});
            var sketch = newSketch(context, id + "F80", { "sketchPlane" : qUnion([Q0])});
            skCircle(sketch, "E88", {"center": v(40, 20) * mm, "radius": 1.6 * mm});
            skSolve(sketch);
        }
        {
            var Q0;
            Q0 = qSketchRegion(id + "F80", true);
            var Q1;
            Q1=makeQuery(id+"F41.boolean.opBoolean","MERGE",FACE,{"derivedFrom":[makeQuery(id+"F39.boolean.opBoolean","MERGE",FACE,{"derivedFrom":[makeQuery(id+"F37.boolean.opBoolean","MERGE",FACE,{"derivedFrom":[makeQuery(id+"F35.boolean.opBoolean","MERGE",FACE,{"derivedFrom":[makeQuery(id+"F33.boolean.opBoolean","MERGE",FACE,{"derivedFrom":[makeQuery(id+"F7.boolean.opBoolean","MERGE",FACE,{"derivedFrom":[makeQuery(id+"F1.opExtrude","CAP_FACE",FACE,{"disambiguationData":[OSD([sQuery(id+"F0.wireOp",EDGE,"E0.rect.bottom"),sQuery(id+"F0.wireOp",EDGE,"E0.rect.top"),sQuery(id+"F0.wireOp",EDGE,"E0.rect.left"),sQuery(id+"F0.wireOp",EDGE,"E0.rect.right")])],"isStart":true}),makeQuery(id+"F7.opExtrude","CAP_FACE",FACE,{"disambiguationData":[OSD([sQuery(id+"F6.wireOp",EDGE,"E3.bottom"),sQuery(id+"F6.wireOp",EDGE,"E3.top"),sQuery(id+"F6.wireOp",EDGE,"E3.left"),sQuery(id+"F6.wireOp",EDGE,"E3.right")])],"isStart":true})]}),makeQuery(id+"F33.opExtrude","CAP_FACE",FACE,{"disambiguationData":[OSD([sQuery(id+"F32.wireOp",EDGE,"E54.bottom"),sQuery(id+"F32.wireOp",EDGE,"E54.top"),sQuery(id+"F32.wireOp",EDGE,"E54.left"),sQuery(id+"F32.wireOp",EDGE,"E54.right")])],"isStart":true})]}),makeQuery(id+"F35.opExtrude","CAP_FACE",FACE,{"disambiguationData":[OSD([sQuery(id+"F34.wireOp",EDGE,"E55.bottom"),sQuery(id+"F34.wireOp",EDGE,"E55.top"),sQuery(id+"F34.wireOp",EDGE,"E55.left"),sQuery(id+"F34.wireOp",EDGE,"E55.right")])],"isStart":true})]}),makeQuery(id+"F37.opExtrude","CAP_FACE",FACE,{"disambiguationData":[OSD([sQuery(id+"F36.wireOp",EDGE,"E56.bottom"),sQuery(id+"F36.wireOp",EDGE,"E56.top"),sQuery(id+"F36.wireOp",EDGE,"E56.left"),sQuery(id+"F36.wireOp",EDGE,"E56.right")])],"isStart":true})]}),makeQuery(id+"F39.opExtrude","CAP_FACE",FACE,{"disambiguationData":[OSD([sQuery(id+"F38.wireOp",EDGE,"E57.bottom"),sQuery(id+"F38.wireOp",EDGE,"E57.top"),sQuery(id+"F38.wireOp",EDGE,"E57.left"),sQuery(id+"F38.wireOp",EDGE,"E57.right")])],"isStart":true})]}),makeQuery(id+"F41.opExtrude","CAP_FACE",FACE,{"disambiguationData":[OSD([sQuery(id+"F40.wireOp",EDGE,"E58.bottom"),sQuery(id+"F40.wireOp",EDGE,"E58.top"),sQuery(id+"F40.wireOp",EDGE,"E58.left"),sQuery(id+"F40.wireOp",EDGE,"E58.right")])],"isStart":true})]});
            extrude(context, id + "F81", {"entities" : qUnion([Q0]), "operationType" : NewBodyOperationType.ADD, "endBound" : BoundingType.UP_TO_SURFACE, "endBoundEntityFace" : qUnion([Q1]), "depth" : 25 * mm});
        }
        {
            var Q0;
            Q0=makeQuery(id+"F61.boolean.opBoolean","MERGE",FACE,{"derivedFrom":[makeQuery(id+"F59.boolean.opBoolean","MERGE",FACE,{"derivedFrom":[makeQuery(id+"F57.boolean.opBoolean","MERGE",FACE,{"derivedFrom":[makeQuery(id+"F55.boolean.opBoolean","MERGE",FACE,{"derivedFrom":[makeQuery(id+"F53.boolean.opBoolean","MERGE",FACE,{"derivedFrom":[makeQuery(id+"F51.boolean.opBoolean","MERGE",FACE,{"derivedFrom":[makeQuery(id+"F15.boolean.opBoolean","MERGE",FACE,{"derivedFrom":[makeQuery(id+"F13.boolean.opBoolean","MERGE",FACE,{"derivedFrom":[makeQuery(id+"F11.boolean.opBoolean","MERGE",FACE,{"derivedFrom":[makeQuery(id+"F9.boolean.opBoolean","COPY",FACE,{"derivedFrom":makeQuery(id+"F9.opExtrude","CAP_FACE",FACE,{"disambiguationData":[OSD([sQuery(id+"F8.wireOp",EDGE,"E4.bottom"),sQuery(id+"F8.wireOp",EDGE,"E4.top"),sQuery(id+"F8.wireOp",EDGE,"E4.left"),sQuery(id+"F8.wireOp",EDGE,"E4.right")])],"isStart":false})}),makeQuery(id+"F11.opExtrude","CAP_FACE",FACE,{"disambiguationData":[OSD([sQuery(id+"F10.wireOp",EDGE,"E5.bottom"),sQuery(id+"F10.wireOp",EDGE,"E5.top"),sQuery(id+"F10.wireOp",EDGE,"E5.left"),sQuery(id+"F10.wireOp",EDGE,"E5.right")])],"isStart":false})]}),makeQuery(id+"F13.opExtrude","CAP_FACE",FACE,{"disambiguationData":[OSD([sQuery(id+"F12.wireOp",EDGE,"E6.bottom"),sQuery(id+"F12.wireOp",EDGE,"E6.top"),sQuery(id+"F12.wireOp",EDGE,"E6.left"),sQuery(id+"F12.wireOp",EDGE,"E6.right")])],"isStart":false})]}),makeQuery(id+"F15.opExtrude","CAP_FACE",FACE,{"disambiguationData":[OSD([sQuery(id+"F14.wireOp",EDGE,"E7.bottom"),sQuery(id+"F14.wireOp",EDGE,"E7.top"),sQuery(id+"F14.wireOp",EDGE,"E7.left"),sQuery(id+"F14.wireOp",EDGE,"E7.right")])],"isStart":false})]}),makeQuery(id+"F51.opExtrude","CAP_FACE",FACE,{"disambiguationData":[OSD([sQuery(id+"F50.wireOp",EDGE,"E66.bottom"),sQuery(id+"F50.wireOp",EDGE,"E66.top"),sQuery(id+"F50.wireOp",EDGE,"E66.left"),sQuery(id+"F50.wireOp",EDGE,"E66.right")])],"isStart":false})]}),makeQuery(id+"F53.opExtrude","CAP_FACE",FACE,{"disambiguationData":[OSD([sQuery(id+"F52.wireOp",EDGE,"E67.bottom"),sQuery(id+"F52.wireOp",EDGE,"E67.top"),sQuery(id+"F52.wireOp",EDGE,"E67.left"),sQuery(id+"F52.wireOp",EDGE,"E67.right")])],"isStart":false})]}),makeQuery(id+"F55.opExtrude","CAP_FACE",FACE,{"disambiguationData":[OSD([sQuery(id+"F54.wireOp",EDGE,"E68.bottom"),sQuery(id+"F54.wireOp",EDGE,"E68.top"),sQuery(id+"F54.wireOp",EDGE,"E68.left"),sQuery(id+"F54.wireOp",EDGE,"E68.right")])],"isStart":false})]}),makeQuery(id+"F57.opExtrude","CAP_FACE",FACE,{"disambiguationData":[OSD([sQuery(id+"F56.wireOp",EDGE,"E69.bottom"),sQuery(id+"F56.wireOp",EDGE,"E69.top"),sQuery(id+"F56.wireOp",EDGE,"E69.left"),sQuery(id+"F56.wireOp",EDGE,"E69.right")])],"isStart":false})]}),makeQuery(id+"F59.opExtrude","CAP_FACE",FACE,{"disambiguationData":[OSD([sQuery(id+"F58.wireOp",EDGE,"E70.bottom"),sQuery(id+"F58.wireOp",EDGE,"E70.top"),sQuery(id+"F58.wireOp",EDGE,"E70.left"),sQuery(id+"F58.wireOp",EDGE,"E70.right")])],"isStart":false})]}),makeQuery(id+"F61.opExtrude","CAP_FACE",FACE,{"disambiguationData":[OSD([sQuery(id+"F60.wireOp",EDGE,"E71.bottom"),sQuery(id+"F60.wireOp",EDGE,"E71.top"),sQuery(id+"F60.wireOp",EDGE,"E71.left"),sQuery(id+"F60.wireOp",EDGE,"E71.right")])],"isStart":false})]});
            var sketch = newSketch(context, id + "F82", { "sketchPlane" : qUnion([Q0])});
            skCircle(sketch, "E89", {"center": v(40, -12) * mm, "radius": 1.6 * mm});
            skCircle(sketch, "E90.0.1.0", {"center": v(40, -20) * mm, "radius": 1.6 * mm});
            skLineSegment(sketch, "E90.direction1", {"start": v(40, -12) * mm, "end": v(65, -12) * mm, "construction": true});
            skLineSegment(sketch, "E90.direction2", {"start": v(40, -12) * mm, "end": v(40, -20) * mm, "construction": true});
            skSolve(sketch);
        }
        {
            var Q0;
            Q0 = qSketchRegion(id + "F82", true);
            var Q1;
            Q1=makeQuery(id+"F41.boolean.opBoolean","MERGE",FACE,{"derivedFrom":[makeQuery(id+"F39.boolean.opBoolean","MERGE",FACE,{"derivedFrom":[makeQuery(id+"F37.boolean.opBoolean","MERGE",FACE,{"derivedFrom":[makeQuery(id+"F35.boolean.opBoolean","MERGE",FACE,{"derivedFrom":[makeQuery(id+"F33.boolean.opBoolean","MERGE",FACE,{"derivedFrom":[makeQuery(id+"F7.boolean.opBoolean","MERGE",FACE,{"derivedFrom":[makeQuery(id+"F1.opExtrude","CAP_FACE",FACE,{"disambiguationData":[OSD([sQuery(id+"F0.wireOp",EDGE,"E0.rect.bottom"),sQuery(id+"F0.wireOp",EDGE,"E0.rect.top"),sQuery(id+"F0.wireOp",EDGE,"E0.rect.left"),sQuery(id+"F0.wireOp",EDGE,"E0.rect.right")])],"isStart":true}),makeQuery(id+"F7.opExtrude","CAP_FACE",FACE,{"disambiguationData":[OSD([sQuery(id+"F6.wireOp",EDGE,"E3.bottom"),sQuery(id+"F6.wireOp",EDGE,"E3.top"),sQuery(id+"F6.wireOp",EDGE,"E3.left"),sQuery(id+"F6.wireOp",EDGE,"E3.right")])],"isStart":true})]}),makeQuery(id+"F33.opExtrude","CAP_FACE",FACE,{"disambiguationData":[OSD([sQuery(id+"F32.wireOp",EDGE,"E54.bottom"),sQuery(id+"F32.wireOp",EDGE,"E54.top"),sQuery(id+"F32.wireOp",EDGE,"E54.left"),sQuery(id+"F32.wireOp",EDGE,"E54.right")])],"isStart":true})]}),makeQuery(id+"F35.opExtrude","CAP_FACE",FACE,{"disambiguationData":[OSD([sQuery(id+"F34.wireOp",EDGE,"E55.bottom"),sQuery(id+"F34.wireOp",EDGE,"E55.top"),sQuery(id+"F34.wireOp",EDGE,"E55.left"),sQuery(id+"F34.wireOp",EDGE,"E55.right")])],"isStart":true})]}),makeQuery(id+"F37.opExtrude","CAP_FACE",FACE,{"disambiguationData":[OSD([sQuery(id+"F36.wireOp",EDGE,"E56.bottom"),sQuery(id+"F36.wireOp",EDGE,"E56.top"),sQuery(id+"F36.wireOp",EDGE,"E56.left"),sQuery(id+"F36.wireOp",EDGE,"E56.right")])],"isStart":true})]}),makeQuery(id+"F39.opExtrude","CAP_FACE",FACE,{"disambiguationData":[OSD([sQuery(id+"F38.wireOp",EDGE,"E57.bottom"),sQuery(id+"F38.wireOp",EDGE,"E57.top"),sQuery(id+"F38.wireOp",EDGE,"E57.left"),sQuery(id+"F38.wireOp",EDGE,"E57.right")])],"isStart":true})]}),makeQuery(id+"F41.opExtrude","CAP_FACE",FACE,{"disambiguationData":[OSD([sQuery(id+"F40.wireOp",EDGE,"E58.bottom"),sQuery(id+"F40.wireOp",EDGE,"E58.top"),sQuery(id+"F40.wireOp",EDGE,"E58.left"),sQuery(id+"F40.wireOp",EDGE,"E58.right")])],"isStart":true})]});
            extrude(context, id + "F83", {"entities" : qUnion([Q0]), "operationType" : NewBodyOperationType.ADD, "endBound" : BoundingType.UP_TO_SURFACE, "endBoundEntityFace" : qUnion([Q1]), "depth" : 25 * mm});
        }
        {
            var Q0;
            Q0=makeQuery(id+"F61.boolean.opBoolean","MERGE",FACE,{"derivedFrom":[makeQuery(id+"F59.boolean.opBoolean","MERGE",FACE,{"derivedFrom":[makeQuery(id+"F57.boolean.opBoolean","MERGE",FACE,{"derivedFrom":[makeQuery(id+"F55.boolean.opBoolean","MERGE",FACE,{"derivedFrom":[makeQuery(id+"F53.boolean.opBoolean","MERGE",FACE,{"derivedFrom":[makeQuery(id+"F51.boolean.opBoolean","MERGE",FACE,{"derivedFrom":[makeQuery(id+"F15.boolean.opBoolean","MERGE",FACE,{"derivedFrom":[makeQuery(id+"F13.boolean.opBoolean","MERGE",FACE,{"derivedFrom":[makeQuery(id+"F11.boolean.opBoolean","MERGE",FACE,{"derivedFrom":[makeQuery(id+"F9.boolean.opBoolean","COPY",FACE,{"derivedFrom":makeQuery(id+"F9.opExtrude","CAP_FACE",FACE,{"disambiguationData":[OSD([sQuery(id+"F8.wireOp",EDGE,"E4.bottom"),sQuery(id+"F8.wireOp",EDGE,"E4.top"),sQuery(id+"F8.wireOp",EDGE,"E4.left"),sQuery(id+"F8.wireOp",EDGE,"E4.right")])],"isStart":false})}),makeQuery(id+"F11.opExtrude","CAP_FACE",FACE,{"disambiguationData":[OSD([sQuery(id+"F10.wireOp",EDGE,"E5.bottom"),sQuery(id+"F10.wireOp",EDGE,"E5.top"),sQuery(id+"F10.wireOp",EDGE,"E5.left"),sQuery(id+"F10.wireOp",EDGE,"E5.right")])],"isStart":false})]}),makeQuery(id+"F13.opExtrude","CAP_FACE",FACE,{"disambiguationData":[OSD([sQuery(id+"F12.wireOp",EDGE,"E6.bottom"),sQuery(id+"F12.wireOp",EDGE,"E6.top"),sQuery(id+"F12.wireOp",EDGE,"E6.left"),sQuery(id+"F12.wireOp",EDGE,"E6.right")])],"isStart":false})]}),makeQuery(id+"F15.opExtrude","CAP_FACE",FACE,{"disambiguationData":[OSD([sQuery(id+"F14.wireOp",EDGE,"E7.bottom"),sQuery(id+"F14.wireOp",EDGE,"E7.top"),sQuery(id+"F14.wireOp",EDGE,"E7.left"),sQuery(id+"F14.wireOp",EDGE,"E7.right")])],"isStart":false})]}),makeQuery(id+"F51.opExtrude","CAP_FACE",FACE,{"disambiguationData":[OSD([sQuery(id+"F50.wireOp",EDGE,"E66.bottom"),sQuery(id+"F50.wireOp",EDGE,"E66.top"),sQuery(id+"F50.wireOp",EDGE,"E66.left"),sQuery(id+"F50.wireOp",EDGE,"E66.right")])],"isStart":false})]}),makeQuery(id+"F53.opExtrude","CAP_FACE",FACE,{"disambiguationData":[OSD([sQuery(id+"F52.wireOp",EDGE,"E67.bottom"),sQuery(id+"F52.wireOp",EDGE,"E67.top"),sQuery(id+"F52.wireOp",EDGE,"E67.left"),sQuery(id+"F52.wireOp",EDGE,"E67.right")])],"isStart":false})]}),makeQuery(id+"F55.opExtrude","CAP_FACE",FACE,{"disambiguationData":[OSD([sQuery(id+"F54.wireOp",EDGE,"E68.bottom"),sQuery(id+"F54.wireOp",EDGE,"E68.top"),sQuery(id+"F54.wireOp",EDGE,"E68.left"),sQuery(id+"F54.wireOp",EDGE,"E68.right")])],"isStart":false})]}),makeQuery(id+"F57.opExtrude","CAP_FACE",FACE,{"disambiguationData":[OSD([sQuery(id+"F56.wireOp",EDGE,"E69.bottom"),sQuery(id+"F56.wireOp",EDGE,"E69.top"),sQuery(id+"F56.wireOp",EDGE,"E69.left"),sQuery(id+"F56.wireOp",EDGE,"E69.right")])],"isStart":false})]}),makeQuery(id+"F59.opExtrude","CAP_FACE",FACE,{"disambiguationData":[OSD([sQuery(id+"F58.wireOp",EDGE,"E70.bottom"),sQuery(id+"F58.wireOp",EDGE,"E70.top"),sQuery(id+"F58.wireOp",EDGE,"E70.left"),sQuery(id+"F58.wireOp",EDGE,"E70.right")])],"isStart":false})]}),makeQuery(id+"F61.opExtrude","CAP_FACE",FACE,{"disambiguationData":[OSD([sQuery(id+"F60.wireOp",EDGE,"E71.bottom"),sQuery(id+"F60.wireOp",EDGE,"E71.top"),sQuery(id+"F60.wireOp",EDGE,"E71.left"),sQuery(id+"F60.wireOp",EDGE,"E71.right")])],"isStart":false})]});
            var sketch = newSketch(context, id + "F84", { "sketchPlane" : qUnion([Q0])});
            skCircle(sketch, "E91", {"center": v(36, -7.79) * mm, "radius": 1.6 * mm});
            skSolve(sketch);
        }
        {
            var Q0;
            Q0 = qSketchRegion(id + "F84", true);
            var Q1;
            Q1=makeQuery(id+"F41.boolean.opBoolean","MERGE",FACE,{"derivedFrom":[makeQuery(id+"F39.boolean.opBoolean","MERGE",FACE,{"derivedFrom":[makeQuery(id+"F37.boolean.opBoolean","MERGE",FACE,{"derivedFrom":[makeQuery(id+"F35.boolean.opBoolean","MERGE",FACE,{"derivedFrom":[makeQuery(id+"F33.boolean.opBoolean","MERGE",FACE,{"derivedFrom":[makeQuery(id+"F7.boolean.opBoolean","MERGE",FACE,{"derivedFrom":[makeQuery(id+"F1.opExtrude","CAP_FACE",FACE,{"disambiguationData":[OSD([sQuery(id+"F0.wireOp",EDGE,"E0.rect.bottom"),sQuery(id+"F0.wireOp",EDGE,"E0.rect.top"),sQuery(id+"F0.wireOp",EDGE,"E0.rect.left"),sQuery(id+"F0.wireOp",EDGE,"E0.rect.right")])],"isStart":true}),makeQuery(id+"F7.opExtrude","CAP_FACE",FACE,{"disambiguationData":[OSD([sQuery(id+"F6.wireOp",EDGE,"E3.bottom"),sQuery(id+"F6.wireOp",EDGE,"E3.top"),sQuery(id+"F6.wireOp",EDGE,"E3.left"),sQuery(id+"F6.wireOp",EDGE,"E3.right")])],"isStart":true})]}),makeQuery(id+"F33.opExtrude","CAP_FACE",FACE,{"disambiguationData":[OSD([sQuery(id+"F32.wireOp",EDGE,"E54.bottom"),sQuery(id+"F32.wireOp",EDGE,"E54.top"),sQuery(id+"F32.wireOp",EDGE,"E54.left"),sQuery(id+"F32.wireOp",EDGE,"E54.right")])],"isStart":true})]}),makeQuery(id+"F35.opExtrude","CAP_FACE",FACE,{"disambiguationData":[OSD([sQuery(id+"F34.wireOp",EDGE,"E55.bottom"),sQuery(id+"F34.wireOp",EDGE,"E55.top"),sQuery(id+"F34.wireOp",EDGE,"E55.left"),sQuery(id+"F34.wireOp",EDGE,"E55.right")])],"isStart":true})]}),makeQuery(id+"F37.opExtrude","CAP_FACE",FACE,{"disambiguationData":[OSD([sQuery(id+"F36.wireOp",EDGE,"E56.bottom"),sQuery(id+"F36.wireOp",EDGE,"E56.top"),sQuery(id+"F36.wireOp",EDGE,"E56.left"),sQuery(id+"F36.wireOp",EDGE,"E56.right")])],"isStart":true})]}),makeQuery(id+"F39.opExtrude","CAP_FACE",FACE,{"disambiguationData":[OSD([sQuery(id+"F38.wireOp",EDGE,"E57.bottom"),sQuery(id+"F38.wireOp",EDGE,"E57.top"),sQuery(id+"F38.wireOp",EDGE,"E57.left"),sQuery(id+"F38.wireOp",EDGE,"E57.right")])],"isStart":true})]}),makeQuery(id+"F41.opExtrude","CAP_FACE",FACE,{"disambiguationData":[OSD([sQuery(id+"F40.wireOp",EDGE,"E58.bottom"),sQuery(id+"F40.wireOp",EDGE,"E58.top"),sQuery(id+"F40.wireOp",EDGE,"E58.left"),sQuery(id+"F40.wireOp",EDGE,"E58.right")])],"isStart":true})]});
            extrude(context, id + "F85", {"entities" : qUnion([Q0]), "operationType" : NewBodyOperationType.ADD, "endBound" : BoundingType.UP_TO_SURFACE, "endBoundEntityFace" : qUnion([Q1]), "depth" : 25 * mm});
        }
        {
            var Q0;
            Q0=makeQuery(id+"F41.boolean.opBoolean","MERGE",FACE,{"derivedFrom":[makeQuery(id+"F39.boolean.opBoolean","MERGE",FACE,{"derivedFrom":[makeQuery(id+"F37.boolean.opBoolean","MERGE",FACE,{"derivedFrom":[makeQuery(id+"F35.boolean.opBoolean","MERGE",FACE,{"derivedFrom":[makeQuery(id+"F33.boolean.opBoolean","MERGE",FACE,{"derivedFrom":[makeQuery(id+"F7.boolean.opBoolean","MERGE",FACE,{"derivedFrom":[makeQuery(id+"F1.opExtrude","CAP_FACE",FACE,{"disambiguationData":[OSD([sQuery(id+"F0.wireOp",EDGE,"E0.rect.bottom"),sQuery(id+"F0.wireOp",EDGE,"E0.rect.top"),sQuery(id+"F0.wireOp",EDGE,"E0.rect.left"),sQuery(id+"F0.wireOp",EDGE,"E0.rect.right")])],"isStart":true}),makeQuery(id+"F7.opExtrude","CAP_FACE",FACE,{"disambiguationData":[OSD([sQuery(id+"F6.wireOp",EDGE,"E3.bottom"),sQuery(id+"F6.wireOp",EDGE,"E3.top"),sQuery(id+"F6.wireOp",EDGE,"E3.left"),sQuery(id+"F6.wireOp",EDGE,"E3.right")])],"isStart":true})]}),makeQuery(id+"F33.opExtrude","CAP_FACE",FACE,{"disambiguationData":[OSD([sQuery(id+"F32.wireOp",EDGE,"E54.bottom"),sQuery(id+"F32.wireOp",EDGE,"E54.top"),sQuery(id+"F32.wireOp",EDGE,"E54.left"),sQuery(id+"F32.wireOp",EDGE,"E54.right")])],"isStart":true})]}),makeQuery(id+"F35.opExtrude","CAP_FACE",FACE,{"disambiguationData":[OSD([sQuery(id+"F34.wireOp",EDGE,"E55.bottom"),sQuery(id+"F34.wireOp",EDGE,"E55.top"),sQuery(id+"F34.wireOp",EDGE,"E55.left"),sQuery(id+"F34.wireOp",EDGE,"E55.right")])],"isStart":true})]}),makeQuery(id+"F37.opExtrude","CAP_FACE",FACE,{"disambiguationData":[OSD([sQuery(id+"F36.wireOp",EDGE,"E56.bottom"),sQuery(id+"F36.wireOp",EDGE,"E56.top"),sQuery(id+"F36.wireOp",EDGE,"E56.left"),sQuery(id+"F36.wireOp",EDGE,"E56.right")])],"isStart":true})]}),makeQuery(id+"F39.opExtrude","CAP_FACE",FACE,{"disambiguationData":[OSD([sQuery(id+"F38.wireOp",EDGE,"E57.bottom"),sQuery(id+"F38.wireOp",EDGE,"E57.top"),sQuery(id+"F38.wireOp",EDGE,"E57.left"),sQuery(id+"F38.wireOp",EDGE,"E57.right")])],"isStart":true})]}),makeQuery(id+"F41.opExtrude","CAP_FACE",FACE,{"disambiguationData":[OSD([sQuery(id+"F40.wireOp",EDGE,"E58.bottom"),sQuery(id+"F40.wireOp",EDGE,"E58.top"),sQuery(id+"F40.wireOp",EDGE,"E58.left"),sQuery(id+"F40.wireOp",EDGE,"E58.right")])],"isStart":true})]});
            var sketch = newSketch(context, id + "F86", { "sketchPlane" : qUnion([Q0])});
            skLineSegment(sketch, "E92.bottom", {"start": v(-18.8, 24.35) * mm, "end": v(-18.5, 24.35) * mm});
            skLineSegment(sketch, "E92.top", {"start": v(-18.8, 23.75) * mm, "end": v(-18.5, 23.75) * mm});
            skLineSegment(sketch, "E92.left", {"start": v(-18.8, 24.35) * mm, "end": v(-18.8, 23.75) * mm});
            skLineSegment(sketch, "E92.right", {"start": v(-18.5, 24.35) * mm, "end": v(-18.5, 23.75) * mm});
            skLineSegment(sketch, "E93.0.1.0", {"start": v(-18.8, 16.35) * mm, "end": v(-18.5, 16.35) * mm});
            skLineSegment(sketch, "E93.0.1.1", {"start": v(-18.8, 16.35) * mm, "end": v(-18.8, 15.75) * mm});
            skLineSegment(sketch, "E93.0.1.2", {"start": v(-18.5, 16.35) * mm, "end": v(-18.5, 15.75) * mm});
            skLineSegment(sketch, "E93.0.1.3", {"start": v(-18.8, 15.75) * mm, "end": v(-18.5, 15.75) * mm});
            skLineSegment(sketch, "E93.0.2.0", {"start": v(-18.8, 8.35) * mm, "end": v(-18.5, 8.35) * mm});
            skLineSegment(sketch, "E93.0.2.1", {"start": v(-18.8, 8.35) * mm, "end": v(-18.8, 7.75) * mm});
            skLineSegment(sketch, "E93.0.2.2", {"start": v(-18.5, 8.35) * mm, "end": v(-18.5, 7.75) * mm});
            skLineSegment(sketch, "E93.0.2.3", {"start": v(-18.8, 7.75) * mm, "end": v(-18.5, 7.75) * mm});
            skLineSegment(sketch, "E93.0.3.0", {"start": v(-18.8, 0.35) * mm, "end": v(-18.5, 0.35) * mm});
            skLineSegment(sketch, "E93.0.3.1", {"start": v(-18.8, 0.35) * mm, "end": v(-18.8, -0.25) * mm});
            skLineSegment(sketch, "E93.0.3.2", {"start": v(-18.5, 0.35) * mm, "end": v(-18.5, -0.25) * mm});
            skLineSegment(sketch, "E93.0.3.3", {"start": v(-18.8, -0.25) * mm, "end": v(-18.5, -0.25) * mm});
            skLineSegment(sketch, "E93.0.4.0", {"start": v(-18.8, -7.65) * mm, "end": v(-18.5, -7.65) * mm});
            skLineSegment(sketch, "E93.0.4.1", {"start": v(-18.8, -7.65) * mm, "end": v(-18.8, -8.25) * mm});
            skLineSegment(sketch, "E93.0.4.2", {"start": v(-18.5, -7.65) * mm, "end": v(-18.5, -8.25) * mm});
            skLineSegment(sketch, "E93.0.4.3", {"start": v(-18.8, -8.25) * mm, "end": v(-18.5, -8.25) * mm});
            skLineSegment(sketch, "E93.0.5.0", {"start": v(-18.8, -15.65) * mm, "end": v(-18.5, -15.65) * mm});
            skLineSegment(sketch, "E93.0.5.1", {"start": v(-18.8, -15.65) * mm, "end": v(-18.8, -16.25) * mm});
            skLineSegment(sketch, "E93.0.5.2", {"start": v(-18.5, -15.65) * mm, "end": v(-18.5, -16.25) * mm});
            skLineSegment(sketch, "E93.0.5.3", {"start": v(-18.8, -16.25) * mm, "end": v(-18.5, -16.25) * mm});
            skLineSegment(sketch, "E93.0.6.0", {"start": v(-18.8, -23.65) * mm, "end": v(-18.5, -23.65) * mm});
            skLineSegment(sketch, "E93.0.6.1", {"start": v(-18.8, -23.65) * mm, "end": v(-18.8, -24.25) * mm});
            skLineSegment(sketch, "E93.0.6.2", {"start": v(-18.5, -23.65) * mm, "end": v(-18.5, -24.25) * mm});
            skLineSegment(sketch, "E93.0.6.3", {"start": v(-18.8, -24.25) * mm, "end": v(-18.5, -24.25) * mm});
            skLineSegment(sketch, "E93.1.0.0", {"start": v(-5.5, 24.35) * mm, "end": v(-5.2, 24.35) * mm});
            skLineSegment(sketch, "E93.1.0.1", {"start": v(-5.5, 24.35) * mm, "end": v(-5.5, 23.75) * mm});
            skLineSegment(sketch, "E93.1.0.2", {"start": v(-5.2, 24.35) * mm, "end": v(-5.2, 23.75) * mm});
            skLineSegment(sketch, "E93.1.0.3", {"start": v(-5.5, 23.75) * mm, "end": v(-5.2, 23.75) * mm});
            skLineSegment(sketch, "E93.1.1.0", {"start": v(-5.5, 16.35) * mm, "end": v(-5.2, 16.35) * mm});
            skLineSegment(sketch, "E93.1.1.1", {"start": v(-5.5, 16.35) * mm, "end": v(-5.5, 15.75) * mm});
            skLineSegment(sketch, "E93.1.1.2", {"start": v(-5.2, 16.35) * mm, "end": v(-5.2, 15.75) * mm});
            skLineSegment(sketch, "E93.1.1.3", {"start": v(-5.5, 15.75) * mm, "end": v(-5.2, 15.75) * mm});
            skLineSegment(sketch, "E93.1.2.0", {"start": v(-5.5, 8.35) * mm, "end": v(-5.2, 8.35) * mm});
            skLineSegment(sketch, "E93.1.2.1", {"start": v(-5.5, 8.35) * mm, "end": v(-5.5, 7.75) * mm});
            skLineSegment(sketch, "E93.1.2.2", {"start": v(-5.2, 8.35) * mm, "end": v(-5.2, 7.75) * mm});
            skLineSegment(sketch, "E93.1.2.3", {"start": v(-5.5, 7.75) * mm, "end": v(-5.2, 7.75) * mm});
            skLineSegment(sketch, "E93.1.3.0", {"start": v(-5.5, 0.35) * mm, "end": v(-5.2, 0.35) * mm});
            skLineSegment(sketch, "E93.1.3.1", {"start": v(-5.5, 0.35) * mm, "end": v(-5.5, -0.25) * mm});
            skLineSegment(sketch, "E93.1.3.2", {"start": v(-5.2, 0.35) * mm, "end": v(-5.2, -0.25) * mm});
            skLineSegment(sketch, "E93.1.3.3", {"start": v(-5.5, -0.25) * mm, "end": v(-5.2, -0.25) * mm});
            skLineSegment(sketch, "E93.1.4.0", {"start": v(-5.5, -7.65) * mm, "end": v(-5.2, -7.65) * mm});
            skLineSegment(sketch, "E93.1.4.1", {"start": v(-5.5, -7.65) * mm, "end": v(-5.5, -8.25) * mm});
            skLineSegment(sketch, "E93.1.4.2", {"start": v(-5.2, -7.65) * mm, "end": v(-5.2, -8.25) * mm});
            skLineSegment(sketch, "E93.1.4.3", {"start": v(-5.5, -8.25) * mm, "end": v(-5.2, -8.25) * mm});
            skLineSegment(sketch, "E93.1.5.0", {"start": v(-5.5, -15.65) * mm, "end": v(-5.2, -15.65) * mm});
            skLineSegment(sketch, "E93.1.5.1", {"start": v(-5.5, -15.65) * mm, "end": v(-5.5, -16.25) * mm});
            skLineSegment(sketch, "E93.1.5.2", {"start": v(-5.2, -15.65) * mm, "end": v(-5.2, -16.25) * mm});
            skLineSegment(sketch, "E93.1.5.3", {"start": v(-5.5, -16.25) * mm, "end": v(-5.2, -16.25) * mm});
            skLineSegment(sketch, "E93.1.6.0", {"start": v(-5.5, -23.65) * mm, "end": v(-5.2, -23.65) * mm});
            skLineSegment(sketch, "E93.1.6.1", {"start": v(-5.5, -23.65) * mm, "end": v(-5.5, -24.25) * mm});
            skLineSegment(sketch, "E93.1.6.2", {"start": v(-5.2, -23.65) * mm, "end": v(-5.2, -24.25) * mm});
            skLineSegment(sketch, "E93.1.6.3", {"start": v(-5.5, -24.25) * mm, "end": v(-5.2, -24.25) * mm});
            skLineSegment(sketch, "E93.direction1", {"start": v(-18.8, 24.35) * mm, "end": v(-5.5, 24.35) * mm, "construction": true});
            skLineSegment(sketch, "E93.direction2", {"start": v(-18.8, 24.35) * mm, "end": v(-18.8, 16.35) * mm, "construction": true});
            skSolve(sketch);
        }
        {
            var Q0;
            Q0 = qSketchRegion(id + "F86", true);
            var Q1;
            Q1=makeQuery(id+"F61.boolean.opBoolean","MERGE",FACE,{"derivedFrom":[makeQuery(id+"F59.boolean.opBoolean","MERGE",FACE,{"derivedFrom":[makeQuery(id+"F57.boolean.opBoolean","MERGE",FACE,{"derivedFrom":[makeQuery(id+"F55.boolean.opBoolean","MERGE",FACE,{"derivedFrom":[makeQuery(id+"F53.boolean.opBoolean","MERGE",FACE,{"derivedFrom":[makeQuery(id+"F51.boolean.opBoolean","MERGE",FACE,{"derivedFrom":[makeQuery(id+"F15.boolean.opBoolean","MERGE",FACE,{"derivedFrom":[makeQuery(id+"F13.boolean.opBoolean","MERGE",FACE,{"derivedFrom":[makeQuery(id+"F11.boolean.opBoolean","MERGE",FACE,{"derivedFrom":[makeQuery(id+"F9.boolean.opBoolean","COPY",FACE,{"derivedFrom":makeQuery(id+"F9.opExtrude","CAP_FACE",FACE,{"disambiguationData":[OSD([sQuery(id+"F8.wireOp",EDGE,"E4.bottom"),sQuery(id+"F8.wireOp",EDGE,"E4.top"),sQuery(id+"F8.wireOp",EDGE,"E4.left"),sQuery(id+"F8.wireOp",EDGE,"E4.right")])],"isStart":false})}),makeQuery(id+"F11.opExtrude","CAP_FACE",FACE,{"disambiguationData":[OSD([sQuery(id+"F10.wireOp",EDGE,"E5.bottom"),sQuery(id+"F10.wireOp",EDGE,"E5.top"),sQuery(id+"F10.wireOp",EDGE,"E5.left"),sQuery(id+"F10.wireOp",EDGE,"E5.right")])],"isStart":false})]}),makeQuery(id+"F13.opExtrude","CAP_FACE",FACE,{"disambiguationData":[OSD([sQuery(id+"F12.wireOp",EDGE,"E6.bottom"),sQuery(id+"F12.wireOp",EDGE,"E6.top"),sQuery(id+"F12.wireOp",EDGE,"E6.left"),sQuery(id+"F12.wireOp",EDGE,"E6.right")])],"isStart":false})]}),makeQuery(id+"F15.opExtrude","CAP_FACE",FACE,{"disambiguationData":[OSD([sQuery(id+"F14.wireOp",EDGE,"E7.bottom"),sQuery(id+"F14.wireOp",EDGE,"E7.top"),sQuery(id+"F14.wireOp",EDGE,"E7.left"),sQuery(id+"F14.wireOp",EDGE,"E7.right")])],"isStart":false})]}),makeQuery(id+"F51.opExtrude","CAP_FACE",FACE,{"disambiguationData":[OSD([sQuery(id+"F50.wireOp",EDGE,"E66.bottom"),sQuery(id+"F50.wireOp",EDGE,"E66.top"),sQuery(id+"F50.wireOp",EDGE,"E66.left"),sQuery(id+"F50.wireOp",EDGE,"E66.right")])],"isStart":false})]}),makeQuery(id+"F53.opExtrude","CAP_FACE",FACE,{"disambiguationData":[OSD([sQuery(id+"F52.wireOp",EDGE,"E67.bottom"),sQuery(id+"F52.wireOp",EDGE,"E67.top"),sQuery(id+"F52.wireOp",EDGE,"E67.left"),sQuery(id+"F52.wireOp",EDGE,"E67.right")])],"isStart":false})]}),makeQuery(id+"F55.opExtrude","CAP_FACE",FACE,{"disambiguationData":[OSD([sQuery(id+"F54.wireOp",EDGE,"E68.bottom"),sQuery(id+"F54.wireOp",EDGE,"E68.top"),sQuery(id+"F54.wireOp",EDGE,"E68.left"),sQuery(id+"F54.wireOp",EDGE,"E68.right")])],"isStart":false})]}),makeQuery(id+"F57.opExtrude","CAP_FACE",FACE,{"disambiguationData":[OSD([sQuery(id+"F56.wireOp",EDGE,"E69.bottom"),sQuery(id+"F56.wireOp",EDGE,"E69.top"),sQuery(id+"F56.wireOp",EDGE,"E69.left"),sQuery(id+"F56.wireOp",EDGE,"E69.right")])],"isStart":false})]}),makeQuery(id+"F59.opExtrude","CAP_FACE",FACE,{"disambiguationData":[OSD([sQuery(id+"F58.wireOp",EDGE,"E70.bottom"),sQuery(id+"F58.wireOp",EDGE,"E70.top"),sQuery(id+"F58.wireOp",EDGE,"E70.left"),sQuery(id+"F58.wireOp",EDGE,"E70.right")])],"isStart":false})]}),makeQuery(id+"F61.opExtrude","CAP_FACE",FACE,{"disambiguationData":[OSD([sQuery(id+"F60.wireOp",EDGE,"E71.bottom"),sQuery(id+"F60.wireOp",EDGE,"E71.top"),sQuery(id+"F60.wireOp",EDGE,"E71.left"),sQuery(id+"F60.wireOp",EDGE,"E71.right")])],"isStart":false})]});
            extrude(context, id + "F87", {"entities" : qUnion([Q0]), "operationType" : NewBodyOperationType.ADD, "endBound" : BoundingType.UP_TO_SURFACE, "oppositeDirection" : true, "endBoundEntityFace" : qUnion([Q1]), "depth" : 25 * mm});
        }
        {
            var Q0;
            Q0=makeQuery(id+"F87.opExtrude","CAP_FACE",FACE,{"disambiguationData":[OSD([sQuery(id+"F86.wireOp",EDGE,"E93.1.3.0"),sQuery(id+"F86.wireOp",EDGE,"E93.1.3.1"),sQuery(id+"F86.wireOp",EDGE,"E93.1.3.2"),sQuery(id+"F86.wireOp",EDGE,"E93.1.3.3")])],"isStart":true});
            var sketch = newSketch(context, id + "F88", { "sketchPlane" : qUnion([Q0])});
            skLineSegment(sketch, "E94.bottom", {"start": v(-5.5, 0.35) * mm, "end": v(-5.2, 0.35) * mm});
            skLineSegment(sketch, "E94.top", {"start": v(-5.5, -0.25) * mm, "end": v(-5.2, -0.25) * mm});
            skLineSegment(sketch, "E94.left", {"start": v(-5.5, 0.35) * mm, "end": v(-5.5, -0.25) * mm});
            skLineSegment(sketch, "E94.right", {"start": v(-5.2, 0.35) * mm, "end": v(-5.2, -0.25) * mm});
            skSolve(sketch);
        }
        {
            var Q0;
            Q0 = qSketchRegion(id + "F88", true);
            extrude(context, id + "F89", {"entities" : qUnion([Q0]), "operationType" : NewBodyOperationType.REMOVE, "oppositeDirection" : true, "depth" : 5.2 * mm});
        }
        {
            var Q0;
            Q0=makeQuery(id+"F87.boolean.opBoolean","MERGE",FACE,{"derivedFrom":[makeQuery(id+"F41.boolean.opBoolean","MERGE",FACE,{"derivedFrom":[makeQuery(id+"F39.boolean.opBoolean","MERGE",FACE,{"derivedFrom":[makeQuery(id+"F37.boolean.opBoolean","MERGE",FACE,{"derivedFrom":[makeQuery(id+"F35.boolean.opBoolean","MERGE",FACE,{"derivedFrom":[makeQuery(id+"F33.boolean.opBoolean","MERGE",FACE,{"derivedFrom":[makeQuery(id+"F7.boolean.opBoolean","MERGE",FACE,{"derivedFrom":[makeQuery(id+"F1.opExtrude","CAP_FACE",FACE,{"disambiguationData":[OSD([sQuery(id+"F0.wireOp",EDGE,"E0.rect.bottom"),sQuery(id+"F0.wireOp",EDGE,"E0.rect.top"),sQuery(id+"F0.wireOp",EDGE,"E0.rect.left"),sQuery(id+"F0.wireOp",EDGE,"E0.rect.right")])],"isStart":true}),makeQuery(id+"F7.opExtrude","CAP_FACE",FACE,{"disambiguationData":[OSD([sQuery(id+"F6.wireOp",EDGE,"E3.bottom"),sQuery(id+"F6.wireOp",EDGE,"E3.top"),sQuery(id+"F6.wireOp",EDGE,"E3.left"),sQuery(id+"F6.wireOp",EDGE,"E3.right")])],"isStart":true})]}),makeQuery(id+"F33.opExtrude","CAP_FACE",FACE,{"disambiguationData":[OSD([sQuery(id+"F32.wireOp",EDGE,"E54.bottom"),sQuery(id+"F32.wireOp",EDGE,"E54.top"),sQuery(id+"F32.wireOp",EDGE,"E54.left"),sQuery(id+"F32.wireOp",EDGE,"E54.right")])],"isStart":true})]}),makeQuery(id+"F35.opExtrude","CAP_FACE",FACE,{"disambiguationData":[OSD([sQuery(id+"F34.wireOp",EDGE,"E55.bottom"),sQuery(id+"F34.wireOp",EDGE,"E55.top"),sQuery(id+"F34.wireOp",EDGE,"E55.left"),sQuery(id+"F34.wireOp",EDGE,"E55.right")])],"isStart":true})]}),makeQuery(id+"F37.opExtrude","CAP_FACE",FACE,{"disambiguationData":[OSD([sQuery(id+"F36.wireOp",EDGE,"E56.bottom"),sQuery(id+"F36.wireOp",EDGE,"E56.top"),sQuery(id+"F36.wireOp",EDGE,"E56.left"),sQuery(id+"F36.wireOp",EDGE,"E56.right")])],"isStart":true})]}),makeQuery(id+"F39.opExtrude","CAP_FACE",FACE,{"disambiguationData":[OSD([sQuery(id+"F38.wireOp",EDGE,"E57.bottom"),sQuery(id+"F38.wireOp",EDGE,"E57.top"),sQuery(id+"F38.wireOp",EDGE,"E57.left"),sQuery(id+"F38.wireOp",EDGE,"E57.right")])],"isStart":true})]}),makeQuery(id+"F41.opExtrude","CAP_FACE",FACE,{"disambiguationData":[OSD([sQuery(id+"F40.wireOp",EDGE,"E58.bottom"),sQuery(id+"F40.wireOp",EDGE,"E58.top"),sQuery(id+"F40.wireOp",EDGE,"E58.left"),sQuery(id+"F40.wireOp",EDGE,"E58.right")])],"isStart":true})]}),makeQuery(id+"F87.opExtrude","CAP_FACE",FACE,{"disambiguationData":[OSD([sQuery(id+"F86.wireOp",EDGE,"E92.bottom"),sQuery(id+"F86.wireOp",EDGE,"E92.top"),sQuery(id+"F86.wireOp",EDGE,"E92.left"),sQuery(id+"F86.wireOp",EDGE,"E92.right")])],"isStart":true}),makeQuery(id+"F87.opExtrude","CAP_FACE",FACE,{"disambiguationData":[OSD([sQuery(id+"F86.wireOp",EDGE,"E93.0.1.0"),sQuery(id+"F86.wireOp",EDGE,"E93.0.1.1"),sQuery(id+"F86.wireOp",EDGE,"E93.0.1.2"),sQuery(id+"F86.wireOp",EDGE,"E93.0.1.3")])],"isStart":true}),makeQuery(id+"F87.opExtrude","CAP_FACE",FACE,{"disambiguationData":[OSD([sQuery(id+"F86.wireOp",EDGE,"E93.0.2.0"),sQuery(id+"F86.wireOp",EDGE,"E93.0.2.1"),sQuery(id+"F86.wireOp",EDGE,"E93.0.2.2"),sQuery(id+"F86.wireOp",EDGE,"E93.0.2.3")])],"isStart":true}),makeQuery(id+"F87.opExtrude","CAP_FACE",FACE,{"disambiguationData":[OSD([sQuery(id+"F86.wireOp",EDGE,"E93.0.3.0"),sQuery(id+"F86.wireOp",EDGE,"E93.0.3.1"),sQuery(id+"F86.wireOp",EDGE,"E93.0.3.2"),sQuery(id+"F86.wireOp",EDGE,"E93.0.3.3")])],"isStart":true}),makeQuery(id+"F87.opExtrude","CAP_FACE",FACE,{"disambiguationData":[OSD([sQuery(id+"F86.wireOp",EDGE,"E93.0.4.0"),sQuery(id+"F86.wireOp",EDGE,"E93.0.4.1"),sQuery(id+"F86.wireOp",EDGE,"E93.0.4.2"),sQuery(id+"F86.wireOp",EDGE,"E93.0.4.3")])],"isStart":true}),makeQuery(id+"F87.opExtrude","CAP_FACE",FACE,{"disambiguationData":[OSD([sQuery(id+"F86.wireOp",EDGE,"E93.0.5.0"),sQuery(id+"F86.wireOp",EDGE,"E93.0.5.1"),sQuery(id+"F86.wireOp",EDGE,"E93.0.5.2"),sQuery(id+"F86.wireOp",EDGE,"E93.0.5.3")])],"isStart":true}),makeQuery(id+"F87.opExtrude","CAP_FACE",FACE,{"disambiguationData":[OSD([sQuery(id+"F86.wireOp",EDGE,"E93.0.6.0"),sQuery(id+"F86.wireOp",EDGE,"E93.0.6.1"),sQuery(id+"F86.wireOp",EDGE,"E93.0.6.2"),sQuery(id+"F86.wireOp",EDGE,"E93.0.6.3")])],"isStart":true}),makeQuery(id+"F87.opExtrude","CAP_FACE",FACE,{"disambiguationData":[OSD([sQuery(id+"F86.wireOp",EDGE,"E93.1.0.0"),sQuery(id+"F86.wireOp",EDGE,"E93.1.0.1"),sQuery(id+"F86.wireOp",EDGE,"E93.1.0.2"),sQuery(id+"F86.wireOp",EDGE,"E93.1.0.3")])],"isStart":true}),makeQuery(id+"F87.opExtrude","CAP_FACE",FACE,{"disambiguationData":[OSD([sQuery(id+"F86.wireOp",EDGE,"E93.1.1.0"),sQuery(id+"F86.wireOp",EDGE,"E93.1.1.1"),sQuery(id+"F86.wireOp",EDGE,"E93.1.1.2"),sQuery(id+"F86.wireOp",EDGE,"E93.1.1.3")])],"isStart":true}),makeQuery(id+"F87.opExtrude","CAP_FACE",FACE,{"disambiguationData":[OSD([sQuery(id+"F86.wireOp",EDGE,"E93.1.2.0"),sQuery(id+"F86.wireOp",EDGE,"E93.1.2.1"),sQuery(id+"F86.wireOp",EDGE,"E93.1.2.2"),sQuery(id+"F86.wireOp",EDGE,"E93.1.2.3")])],"isStart":true}),makeQuery(id+"F87.opExtrude","CAP_FACE",FACE,{"disambiguationData":[OSD([sQuery(id+"F86.wireOp",EDGE,"E93.1.4.0"),sQuery(id+"F86.wireOp",EDGE,"E93.1.4.1"),sQuery(id+"F86.wireOp",EDGE,"E93.1.4.2"),sQuery(id+"F86.wireOp",EDGE,"E93.1.4.3")])],"isStart":true}),makeQuery(id+"F87.opExtrude","CAP_FACE",FACE,{"disambiguationData":[OSD([sQuery(id+"F86.wireOp",EDGE,"E93.1.5.0"),sQuery(id+"F86.wireOp",EDGE,"E93.1.5.1"),sQuery(id+"F86.wireOp",EDGE,"E93.1.5.2"),sQuery(id+"F86.wireOp",EDGE,"E93.1.5.3")])],"isStart":true}),makeQuery(id+"F87.opExtrude","CAP_FACE",FACE,{"disambiguationData":[OSD([sQuery(id+"F86.wireOp",EDGE,"E93.1.6.0"),sQuery(id+"F86.wireOp",EDGE,"E93.1.6.1"),sQuery(id+"F86.wireOp",EDGE,"E93.1.6.2"),sQuery(id+"F86.wireOp",EDGE,"E93.1.6.3")])],"isStart":true})]});
            var sketch = newSketch(context, id + "F90", { "sketchPlane" : qUnion([Q0])});
            skLineSegment(sketch, "E95.bottom", {"start": v(5.2, 24.35) * mm, "end": v(5.5, 24.35) * mm});
            skLineSegment(sketch, "E95.top", {"start": v(5.2, 23.75) * mm, "end": v(5.5, 23.75) * mm});
            skLineSegment(sketch, "E95.left", {"start": v(5.2, 24.35) * mm, "end": v(5.2, 23.75) * mm});
            skLineSegment(sketch, "E95.right", {"start": v(5.5, 24.35) * mm, "end": v(5.5, 23.75) * mm});
            skLineSegment(sketch, "E96.0.1.0", {"start": v(5.2, 16.35) * mm, "end": v(5.5, 16.35) * mm});
            skLineSegment(sketch, "E96.0.1.1", {"start": v(5.5, 16.35) * mm, "end": v(5.5, 15.75) * mm});
            skLineSegment(sketch, "E96.0.1.2", {"start": v(5.2, 15.75) * mm, "end": v(5.5, 15.75) * mm});
            skLineSegment(sketch, "E96.0.1.3", {"start": v(5.2, 16.35) * mm, "end": v(5.2, 15.75) * mm});
            skLineSegment(sketch, "E96.0.2.0", {"start": v(5.2, 8.35) * mm, "end": v(5.5, 8.35) * mm});
            skLineSegment(sketch, "E96.0.2.1", {"start": v(5.5, 8.35) * mm, "end": v(5.5, 7.75) * mm});
            skLineSegment(sketch, "E96.0.2.2", {"start": v(5.2, 7.75) * mm, "end": v(5.5, 7.75) * mm});
            skLineSegment(sketch, "E96.0.2.3", {"start": v(5.2, 8.35) * mm, "end": v(5.2, 7.75) * mm});
            skLineSegment(sketch, "E96.0.3.0", {"start": v(5.2, 0.35) * mm, "end": v(5.5, 0.35) * mm});
            skLineSegment(sketch, "E96.0.3.1", {"start": v(5.5, 0.35) * mm, "end": v(5.5, -0.25) * mm});
            skLineSegment(sketch, "E96.0.3.2", {"start": v(5.2, -0.25) * mm, "end": v(5.5, -0.25) * mm});
            skLineSegment(sketch, "E96.0.3.3", {"start": v(5.2, 0.35) * mm, "end": v(5.2, -0.25) * mm});
            skLineSegment(sketch, "E96.0.4.0", {"start": v(5.2, -7.65) * mm, "end": v(5.5, -7.65) * mm});
            skLineSegment(sketch, "E96.0.4.1", {"start": v(5.5, -7.65) * mm, "end": v(5.5, -8.25) * mm});
            skLineSegment(sketch, "E96.0.4.2", {"start": v(5.2, -8.25) * mm, "end": v(5.5, -8.25) * mm});
            skLineSegment(sketch, "E96.0.4.3", {"start": v(5.2, -7.65) * mm, "end": v(5.2, -8.25) * mm});
            skLineSegment(sketch, "E96.0.5.0", {"start": v(5.2, -15.65) * mm, "end": v(5.5, -15.65) * mm});
            skLineSegment(sketch, "E96.0.5.1", {"start": v(5.5, -15.65) * mm, "end": v(5.5, -16.25) * mm});
            skLineSegment(sketch, "E96.0.5.2", {"start": v(5.2, -16.25) * mm, "end": v(5.5, -16.25) * mm});
            skLineSegment(sketch, "E96.0.5.3", {"start": v(5.2, -15.65) * mm, "end": v(5.2, -16.25) * mm});
            skLineSegment(sketch, "E96.0.6.0", {"start": v(5.2, -23.65) * mm, "end": v(5.5, -23.65) * mm});
            skLineSegment(sketch, "E96.0.6.1", {"start": v(5.5, -23.65) * mm, "end": v(5.5, -24.25) * mm});
            skLineSegment(sketch, "E96.0.6.2", {"start": v(5.2, -24.25) * mm, "end": v(5.5, -24.25) * mm});
            skLineSegment(sketch, "E96.0.6.3", {"start": v(5.2, -23.65) * mm, "end": v(5.2, -24.25) * mm});
            skLineSegment(sketch, "E96.1.0.0", {"start": v(18.5, 24.35) * mm, "end": v(18.8, 24.35) * mm});
            skLineSegment(sketch, "E96.1.0.1", {"start": v(18.8, 24.35) * mm, "end": v(18.8, 23.75) * mm});
            skLineSegment(sketch, "E96.1.0.2", {"start": v(18.5, 23.75) * mm, "end": v(18.8, 23.75) * mm});
            skLineSegment(sketch, "E96.1.0.3", {"start": v(18.5, 24.35) * mm, "end": v(18.5, 23.75) * mm});
            skLineSegment(sketch, "E96.1.1.0", {"start": v(18.5, 16.35) * mm, "end": v(18.8, 16.35) * mm});
            skLineSegment(sketch, "E96.1.1.1", {"start": v(18.8, 16.35) * mm, "end": v(18.8, 15.75) * mm});
            skLineSegment(sketch, "E96.1.1.2", {"start": v(18.5, 15.75) * mm, "end": v(18.8, 15.75) * mm});
            skLineSegment(sketch, "E96.1.1.3", {"start": v(18.5, 16.35) * mm, "end": v(18.5, 15.75) * mm});
            skLineSegment(sketch, "E96.1.2.0", {"start": v(18.5, 8.35) * mm, "end": v(18.8, 8.35) * mm});
            skLineSegment(sketch, "E96.1.2.1", {"start": v(18.8, 8.35) * mm, "end": v(18.8, 7.75) * mm});
            skLineSegment(sketch, "E96.1.2.2", {"start": v(18.5, 7.75) * mm, "end": v(18.8, 7.75) * mm});
            skLineSegment(sketch, "E96.1.2.3", {"start": v(18.5, 8.35) * mm, "end": v(18.5, 7.75) * mm});
            skLineSegment(sketch, "E96.1.3.0", {"start": v(18.5, 0.35) * mm, "end": v(18.8, 0.35) * mm});
            skLineSegment(sketch, "E96.1.3.1", {"start": v(18.8, 0.35) * mm, "end": v(18.8, -0.25) * mm});
            skLineSegment(sketch, "E96.1.3.2", {"start": v(18.5, -0.25) * mm, "end": v(18.8, -0.25) * mm});
            skLineSegment(sketch, "E96.1.3.3", {"start": v(18.5, 0.35) * mm, "end": v(18.5, -0.25) * mm});
            skLineSegment(sketch, "E96.1.4.0", {"start": v(18.5, -7.65) * mm, "end": v(18.8, -7.65) * mm});
            skLineSegment(sketch, "E96.1.4.1", {"start": v(18.8, -7.65) * mm, "end": v(18.8, -8.25) * mm});
            skLineSegment(sketch, "E96.1.4.2", {"start": v(18.5, -8.25) * mm, "end": v(18.8, -8.25) * mm});
            skLineSegment(sketch, "E96.1.4.3", {"start": v(18.5, -7.65) * mm, "end": v(18.5, -8.25) * mm});
            skLineSegment(sketch, "E96.1.5.0", {"start": v(18.5, -15.65) * mm, "end": v(18.8, -15.65) * mm});
            skLineSegment(sketch, "E96.1.5.1", {"start": v(18.8, -15.65) * mm, "end": v(18.8, -16.25) * mm});
            skLineSegment(sketch, "E96.1.5.2", {"start": v(18.5, -16.25) * mm, "end": v(18.8, -16.25) * mm});
            skLineSegment(sketch, "E96.1.5.3", {"start": v(18.5, -15.65) * mm, "end": v(18.5, -16.25) * mm});
            skLineSegment(sketch, "E96.1.6.0", {"start": v(18.5, -23.65) * mm, "end": v(18.8, -23.65) * mm});
            skLineSegment(sketch, "E96.1.6.1", {"start": v(18.8, -23.65) * mm, "end": v(18.8, -24.25) * mm});
            skLineSegment(sketch, "E96.1.6.2", {"start": v(18.5, -24.25) * mm, "end": v(18.8, -24.25) * mm});
            skLineSegment(sketch, "E96.1.6.3", {"start": v(18.5, -23.65) * mm, "end": v(18.5, -24.25) * mm});
            skLineSegment(sketch, "E96.direction1", {"start": v(5.2, 24.35) * mm, "end": v(18.5, 24.35) * mm, "construction": true});
            skLineSegment(sketch, "E96.direction2", {"start": v(5.2, 24.35) * mm, "end": v(5.2, 16.35) * mm, "construction": true});
            skSolve(sketch);
        }
        {
            var Q0;
            Q0 = qSketchRegion(id + "F90", true);
            var Q1;
            Q1=makeQuery(id+"F89.boolean.opBoolean","MERGE",FACE,{"derivedFrom":[makeQuery(id+"F61.boolean.opBoolean","MERGE",FACE,{"derivedFrom":[makeQuery(id+"F59.boolean.opBoolean","MERGE",FACE,{"derivedFrom":[makeQuery(id+"F57.boolean.opBoolean","MERGE",FACE,{"derivedFrom":[makeQuery(id+"F55.boolean.opBoolean","MERGE",FACE,{"derivedFrom":[makeQuery(id+"F53.boolean.opBoolean","MERGE",FACE,{"derivedFrom":[makeQuery(id+"F51.boolean.opBoolean","MERGE",FACE,{"derivedFrom":[makeQuery(id+"F15.boolean.opBoolean","MERGE",FACE,{"derivedFrom":[makeQuery(id+"F13.boolean.opBoolean","MERGE",FACE,{"derivedFrom":[makeQuery(id+"F11.boolean.opBoolean","MERGE",FACE,{"derivedFrom":[makeQuery(id+"F9.boolean.opBoolean","COPY",FACE,{"derivedFrom":makeQuery(id+"F9.opExtrude","CAP_FACE",FACE,{"disambiguationData":[OSD([sQuery(id+"F8.wireOp",EDGE,"E4.bottom"),sQuery(id+"F8.wireOp",EDGE,"E4.top"),sQuery(id+"F8.wireOp",EDGE,"E4.left"),sQuery(id+"F8.wireOp",EDGE,"E4.right")])],"isStart":false})}),makeQuery(id+"F11.opExtrude","CAP_FACE",FACE,{"disambiguationData":[OSD([sQuery(id+"F10.wireOp",EDGE,"E5.bottom"),sQuery(id+"F10.wireOp",EDGE,"E5.top"),sQuery(id+"F10.wireOp",EDGE,"E5.left"),sQuery(id+"F10.wireOp",EDGE,"E5.right")])],"isStart":false})]}),makeQuery(id+"F13.opExtrude","CAP_FACE",FACE,{"disambiguationData":[OSD([sQuery(id+"F12.wireOp",EDGE,"E6.bottom"),sQuery(id+"F12.wireOp",EDGE,"E6.top"),sQuery(id+"F12.wireOp",EDGE,"E6.left"),sQuery(id+"F12.wireOp",EDGE,"E6.right")])],"isStart":false})]}),makeQuery(id+"F15.opExtrude","CAP_FACE",FACE,{"disambiguationData":[OSD([sQuery(id+"F14.wireOp",EDGE,"E7.bottom"),sQuery(id+"F14.wireOp",EDGE,"E7.top"),sQuery(id+"F14.wireOp",EDGE,"E7.left"),sQuery(id+"F14.wireOp",EDGE,"E7.right")])],"isStart":false})]}),makeQuery(id+"F51.opExtrude","CAP_FACE",FACE,{"disambiguationData":[OSD([sQuery(id+"F50.wireOp",EDGE,"E66.bottom"),sQuery(id+"F50.wireOp",EDGE,"E66.top"),sQuery(id+"F50.wireOp",EDGE,"E66.left"),sQuery(id+"F50.wireOp",EDGE,"E66.right")])],"isStart":false})]}),makeQuery(id+"F53.opExtrude","CAP_FACE",FACE,{"disambiguationData":[OSD([sQuery(id+"F52.wireOp",EDGE,"E67.bottom"),sQuery(id+"F52.wireOp",EDGE,"E67.top"),sQuery(id+"F52.wireOp",EDGE,"E67.left"),sQuery(id+"F52.wireOp",EDGE,"E67.right")])],"isStart":false})]}),makeQuery(id+"F55.opExtrude","CAP_FACE",FACE,{"disambiguationData":[OSD([sQuery(id+"F54.wireOp",EDGE,"E68.bottom"),sQuery(id+"F54.wireOp",EDGE,"E68.top"),sQuery(id+"F54.wireOp",EDGE,"E68.left"),sQuery(id+"F54.wireOp",EDGE,"E68.right")])],"isStart":false})]}),makeQuery(id+"F57.opExtrude","CAP_FACE",FACE,{"disambiguationData":[OSD([sQuery(id+"F56.wireOp",EDGE,"E69.bottom"),sQuery(id+"F56.wireOp",EDGE,"E69.top"),sQuery(id+"F56.wireOp",EDGE,"E69.left"),sQuery(id+"F56.wireOp",EDGE,"E69.right")])],"isStart":false})]}),makeQuery(id+"F59.opExtrude","CAP_FACE",FACE,{"disambiguationData":[OSD([sQuery(id+"F58.wireOp",EDGE,"E70.bottom"),sQuery(id+"F58.wireOp",EDGE,"E70.top"),sQuery(id+"F58.wireOp",EDGE,"E70.left"),sQuery(id+"F58.wireOp",EDGE,"E70.right")])],"isStart":false})]}),makeQuery(id+"F61.opExtrude","CAP_FACE",FACE,{"disambiguationData":[OSD([sQuery(id+"F60.wireOp",EDGE,"E71.bottom"),sQuery(id+"F60.wireOp",EDGE,"E71.top"),sQuery(id+"F60.wireOp",EDGE,"E71.left"),sQuery(id+"F60.wireOp",EDGE,"E71.right")])],"isStart":false})]}),makeQuery(id+"F89.opExtrude","CAP_FACE",FACE,{"disambiguationData":[OSD([sQuery(id+"F88.wireOp",EDGE,"E94.bottom"),sQuery(id+"F88.wireOp",EDGE,"E94.top"),sQuery(id+"F88.wireOp",EDGE,"E94.left"),sQuery(id+"F88.wireOp",EDGE,"E94.right")])],"isStart":false})]});
            extrude(context, id + "F91", {"entities" : qUnion([Q0]), "operationType" : NewBodyOperationType.ADD, "endBound" : BoundingType.UP_TO_SURFACE, "oppositeDirection" : true, "endBoundEntityFace" : qUnion([Q1]), "depth" : 25 * mm});
        }
        {
            var Q0;
            Q0=makeQuery(id+"F91.opExtrude","CAP_FACE",FACE,{"disambiguationData":[OSD([sQuery(id+"F90.wireOp",EDGE,"E96.0.3.0"),sQuery(id+"F90.wireOp",EDGE,"E96.0.3.1"),sQuery(id+"F90.wireOp",EDGE,"E96.0.3.2"),sQuery(id+"F90.wireOp",EDGE,"E96.0.3.3")])],"isStart":true});
            var sketch = newSketch(context, id + "F92", { "sketchPlane" : qUnion([Q0])});
            skLineSegment(sketch, "E97.bottom", {"start": v(5.2, 0.35) * mm, "end": v(5.5, 0.35) * mm});
            skLineSegment(sketch, "E97.top", {"start": v(5.2, -0.25) * mm, "end": v(5.5, -0.25) * mm});
            skLineSegment(sketch, "E97.left", {"start": v(5.2, 0.35) * mm, "end": v(5.2, -0.25) * mm});
            skLineSegment(sketch, "E97.right", {"start": v(5.5, 0.35) * mm, "end": v(5.5, -0.25) * mm});
            skSolve(sketch);
        }
        {
            var Q0;
            Q0 = qSketchRegion(id + "F92", true);
            extrude(context, id + "F93", {"entities" : qUnion([Q0]), "operationType" : NewBodyOperationType.REMOVE, "oppositeDirection" : true, "depth" : 5.2 * mm});
        }
        {
            var Q0;
            Q0=makeQuery(id+"F91.opExtrude","CAP_FACE",FACE,{"disambiguationData":[OSD([sQuery(id+"F90.wireOp",EDGE,"E96.1.3.0"),sQuery(id+"F90.wireOp",EDGE,"E96.1.3.1"),sQuery(id+"F90.wireOp",EDGE,"E96.1.3.2"),sQuery(id+"F90.wireOp",EDGE,"E96.1.3.3")])],"isStart":true});
            var sketch = newSketch(context, id + "F94", { "sketchPlane" : qUnion([Q0])});
            skLineSegment(sketch, "E98.bottom", {"start": v(18.8, -0.25) * mm, "end": v(18.5, -0.25) * mm});
            skLineSegment(sketch, "E98.top", {"start": v(18.8, 0.35) * mm, "end": v(18.5, 0.35) * mm});
            skLineSegment(sketch, "E98.left", {"start": v(18.8, -0.25) * mm, "end": v(18.8, 0.35) * mm});
            skLineSegment(sketch, "E98.right", {"start": v(18.5, -0.25) * mm, "end": v(18.5, 0.35) * mm});
            skLineSegment(sketch, "E99.0.1.0", {"start": v(18.8, 8.35) * mm, "end": v(18.5, 8.35) * mm});
            skLineSegment(sketch, "E99.0.1.1", {"start": v(18.5, 7.75) * mm, "end": v(18.5, 8.35) * mm});
            skLineSegment(sketch, "E99.0.1.2", {"start": v(18.8, 7.75) * mm, "end": v(18.8, 8.35) * mm});
            skLineSegment(sketch, "E99.0.1.3", {"start": v(18.8, 7.75) * mm, "end": v(18.5, 7.75) * mm});
            skLineSegment(sketch, "E99.direction1", {"start": v(18.5, 0.35) * mm, "end": v(43.5, 0.35) * mm, "construction": true});
            skLineSegment(sketch, "E99.direction2", {"start": v(18.5, 0.35) * mm, "end": v(18.5, 8.35) * mm, "construction": true});
            skSolve(sketch);
        }
        {
            var Q0;
            Q0 = qSketchRegion(id + "F94", true);
            extrude(context, id + "F95", {"entities" : qUnion([Q0]), "operationType" : NewBodyOperationType.REMOVE, "oppositeDirection" : true, "depth" : 5.2 * mm});
        }
        {
            var Q0;
            Q0=makeQuery(id+"F95.boolean.opBoolean","MERGE",FACE,{"derivedFrom":[makeQuery(id+"F93.boolean.opBoolean","MERGE",FACE,{"derivedFrom":[makeQuery(id+"F89.boolean.opBoolean","MERGE",FACE,{"derivedFrom":[makeQuery(id+"F61.boolean.opBoolean","MERGE",FACE,{"derivedFrom":[makeQuery(id+"F59.boolean.opBoolean","MERGE",FACE,{"derivedFrom":[makeQuery(id+"F57.boolean.opBoolean","MERGE",FACE,{"derivedFrom":[makeQuery(id+"F55.boolean.opBoolean","MERGE",FACE,{"derivedFrom":[makeQuery(id+"F53.boolean.opBoolean","MERGE",FACE,{"derivedFrom":[makeQuery(id+"F51.boolean.opBoolean","MERGE",FACE,{"derivedFrom":[makeQuery(id+"F15.boolean.opBoolean","MERGE",FACE,{"derivedFrom":[makeQuery(id+"F13.boolean.opBoolean","MERGE",FACE,{"derivedFrom":[makeQuery(id+"F11.boolean.opBoolean","MERGE",FACE,{"derivedFrom":[makeQuery(id+"F9.boolean.opBoolean","COPY",FACE,{"derivedFrom":makeQuery(id+"F9.opExtrude","CAP_FACE",FACE,{"disambiguationData":[OSD([sQuery(id+"F8.wireOp",EDGE,"E4.bottom"),sQuery(id+"F8.wireOp",EDGE,"E4.top"),sQuery(id+"F8.wireOp",EDGE,"E4.left"),sQuery(id+"F8.wireOp",EDGE,"E4.right")])],"isStart":false})}),makeQuery(id+"F11.opExtrude","CAP_FACE",FACE,{"disambiguationData":[OSD([sQuery(id+"F10.wireOp",EDGE,"E5.bottom"),sQuery(id+"F10.wireOp",EDGE,"E5.top"),sQuery(id+"F10.wireOp",EDGE,"E5.left"),sQuery(id+"F10.wireOp",EDGE,"E5.right")])],"isStart":false})]}),makeQuery(id+"F13.opExtrude","CAP_FACE",FACE,{"disambiguationData":[OSD([sQuery(id+"F12.wireOp",EDGE,"E6.bottom"),sQuery(id+"F12.wireOp",EDGE,"E6.top"),sQuery(id+"F12.wireOp",EDGE,"E6.left"),sQuery(id+"F12.wireOp",EDGE,"E6.right")])],"isStart":false})]}),makeQuery(id+"F15.opExtrude","CAP_FACE",FACE,{"disambiguationData":[OSD([sQuery(id+"F14.wireOp",EDGE,"E7.bottom"),sQuery(id+"F14.wireOp",EDGE,"E7.top"),sQuery(id+"F14.wireOp",EDGE,"E7.left"),sQuery(id+"F14.wireOp",EDGE,"E7.right")])],"isStart":false})]}),makeQuery(id+"F51.opExtrude","CAP_FACE",FACE,{"disambiguationData":[OSD([sQuery(id+"F50.wireOp",EDGE,"E66.bottom"),sQuery(id+"F50.wireOp",EDGE,"E66.top"),sQuery(id+"F50.wireOp",EDGE,"E66.left"),sQuery(id+"F50.wireOp",EDGE,"E66.right")])],"isStart":false})]}),makeQuery(id+"F53.opExtrude","CAP_FACE",FACE,{"disambiguationData":[OSD([sQuery(id+"F52.wireOp",EDGE,"E67.bottom"),sQuery(id+"F52.wireOp",EDGE,"E67.top"),sQuery(id+"F52.wireOp",EDGE,"E67.left"),sQuery(id+"F52.wireOp",EDGE,"E67.right")])],"isStart":false})]}),makeQuery(id+"F55.opExtrude","CAP_FACE",FACE,{"disambiguationData":[OSD([sQuery(id+"F54.wireOp",EDGE,"E68.bottom"),sQuery(id+"F54.wireOp",EDGE,"E68.top"),sQuery(id+"F54.wireOp",EDGE,"E68.left"),sQuery(id+"F54.wireOp",EDGE,"E68.right")])],"isStart":false})]}),makeQuery(id+"F57.opExtrude","CAP_FACE",FACE,{"disambiguationData":[OSD([sQuery(id+"F56.wireOp",EDGE,"E69.bottom"),sQuery(id+"F56.wireOp",EDGE,"E69.top"),sQuery(id+"F56.wireOp",EDGE,"E69.left"),sQuery(id+"F56.wireOp",EDGE,"E69.right")])],"isStart":false})]}),makeQuery(id+"F59.opExtrude","CAP_FACE",FACE,{"disambiguationData":[OSD([sQuery(id+"F58.wireOp",EDGE,"E70.bottom"),sQuery(id+"F58.wireOp",EDGE,"E70.top"),sQuery(id+"F58.wireOp",EDGE,"E70.left"),sQuery(id+"F58.wireOp",EDGE,"E70.right")])],"isStart":false})]}),makeQuery(id+"F61.opExtrude","CAP_FACE",FACE,{"disambiguationData":[OSD([sQuery(id+"F60.wireOp",EDGE,"E71.bottom"),sQuery(id+"F60.wireOp",EDGE,"E71.top"),sQuery(id+"F60.wireOp",EDGE,"E71.left"),sQuery(id+"F60.wireOp",EDGE,"E71.right")])],"isStart":false})]}),makeQuery(id+"F89.opExtrude","CAP_FACE",FACE,{"disambiguationData":[OSD([sQuery(id+"F88.wireOp",EDGE,"E94.bottom"),sQuery(id+"F88.wireOp",EDGE,"E94.top"),sQuery(id+"F88.wireOp",EDGE,"E94.left"),sQuery(id+"F88.wireOp",EDGE,"E94.right")])],"isStart":false})]}),makeQuery(id+"F93.opExtrude","CAP_FACE",FACE,{"disambiguationData":[OSD([sQuery(id+"F92.wireOp",EDGE,"E97.bottom"),sQuery(id+"F92.wireOp",EDGE,"E97.top"),sQuery(id+"F92.wireOp",EDGE,"E97.left"),sQuery(id+"F92.wireOp",EDGE,"E97.right")])],"isStart":false})]}),makeQuery(id+"F95.opExtrude","CAP_FACE",FACE,{"disambiguationData":[OSD([sQuery(id+"F94.wireOp",EDGE,"E98.bottom"),sQuery(id+"F94.wireOp",EDGE,"E98.top"),sQuery(id+"F94.wireOp",EDGE,"E98.left"),sQuery(id+"F94.wireOp",EDGE,"E98.right")])],"isStart":false}),makeQuery(id+"F95.opExtrude","CAP_FACE",FACE,{"disambiguationData":[OSD([sQuery(id+"F94.wireOp",EDGE,"E99.0.1.0"),sQuery(id+"F94.wireOp",EDGE,"E99.0.1.1"),sQuery(id+"F94.wireOp",EDGE,"E99.0.1.2"),sQuery(id+"F94.wireOp",EDGE,"E99.0.1.3")])],"isStart":false})]});
            var sketch = newSketch(context, id + "F96", { "sketchPlane" : qUnion([Q0])});
            skLineSegment(sketch, "E100.bottom", {"start": v(23.8, -2.5) * mm, "end": v(24.4, -2.5) * mm});
            skLineSegment(sketch, "E100.top", {"start": v(23.8, -2.8) * mm, "end": v(24.4, -2.8) * mm});
            skLineSegment(sketch, "E100.left", {"start": v(23.8, -2.5) * mm, "end": v(23.8, -2.8) * mm});
            skLineSegment(sketch, "E100.right", {"start": v(24.4, -2.5) * mm, "end": v(24.4, -2.8) * mm});
            skLineSegment(sketch, "E101.0.1.0", {"start": v(23.8, 10.5) * mm, "end": v(24.4, 10.5) * mm});
            skLineSegment(sketch, "E101.0.1.1", {"start": v(24.4, 10.8) * mm, "end": v(24.4, 10.5) * mm});
            skLineSegment(sketch, "E101.0.1.2", {"start": v(23.8, 10.8) * mm, "end": v(24.4, 10.8) * mm});
            skLineSegment(sketch, "E101.0.1.3", {"start": v(23.8, 10.8) * mm, "end": v(23.8, 10.5) * mm});
            skLineSegment(sketch, "E101.direction1", {"start": v(23.8, -2.8) * mm, "end": v(48.8, -2.8) * mm, "construction": true});
            skLineSegment(sketch, "E101.direction2", {"start": v(23.8, -2.8) * mm, "end": v(23.8, 10.5) * mm, "construction": true});
            skSolve(sketch);
        }
        {
            var Q0;
            Q0 = qSketchRegion(id + "F96", true);
            extrude(context, id + "F97", {"entities" : qUnion([Q0]), "operationType" : NewBodyOperationType.ADD, "depth" : 5.2 * mm});
        }
        {
            var Q0;
            Q0=makeQuery(id+"F95.boolean.opBoolean","MERGE",FACE,{"derivedFrom":[makeQuery(id+"F93.boolean.opBoolean","MERGE",FACE,{"derivedFrom":[makeQuery(id+"F89.boolean.opBoolean","MERGE",FACE,{"derivedFrom":[makeQuery(id+"F61.boolean.opBoolean","MERGE",FACE,{"derivedFrom":[makeQuery(id+"F59.boolean.opBoolean","MERGE",FACE,{"derivedFrom":[makeQuery(id+"F57.boolean.opBoolean","MERGE",FACE,{"derivedFrom":[makeQuery(id+"F55.boolean.opBoolean","MERGE",FACE,{"derivedFrom":[makeQuery(id+"F53.boolean.opBoolean","MERGE",FACE,{"derivedFrom":[makeQuery(id+"F51.boolean.opBoolean","MERGE",FACE,{"derivedFrom":[makeQuery(id+"F15.boolean.opBoolean","MERGE",FACE,{"derivedFrom":[makeQuery(id+"F13.boolean.opBoolean","MERGE",FACE,{"derivedFrom":[makeQuery(id+"F11.boolean.opBoolean","MERGE",FACE,{"derivedFrom":[makeQuery(id+"F9.boolean.opBoolean","COPY",FACE,{"derivedFrom":makeQuery(id+"F9.opExtrude","CAP_FACE",FACE,{"disambiguationData":[OSD([sQuery(id+"F8.wireOp",EDGE,"E4.bottom"),sQuery(id+"F8.wireOp",EDGE,"E4.top"),sQuery(id+"F8.wireOp",EDGE,"E4.left"),sQuery(id+"F8.wireOp",EDGE,"E4.right")])],"isStart":false})}),makeQuery(id+"F11.opExtrude","CAP_FACE",FACE,{"disambiguationData":[OSD([sQuery(id+"F10.wireOp",EDGE,"E5.bottom"),sQuery(id+"F10.wireOp",EDGE,"E5.top"),sQuery(id+"F10.wireOp",EDGE,"E5.left"),sQuery(id+"F10.wireOp",EDGE,"E5.right")])],"isStart":false})]}),makeQuery(id+"F13.opExtrude","CAP_FACE",FACE,{"disambiguationData":[OSD([sQuery(id+"F12.wireOp",EDGE,"E6.bottom"),sQuery(id+"F12.wireOp",EDGE,"E6.top"),sQuery(id+"F12.wireOp",EDGE,"E6.left"),sQuery(id+"F12.wireOp",EDGE,"E6.right")])],"isStart":false})]}),makeQuery(id+"F15.opExtrude","CAP_FACE",FACE,{"disambiguationData":[OSD([sQuery(id+"F14.wireOp",EDGE,"E7.bottom"),sQuery(id+"F14.wireOp",EDGE,"E7.top"),sQuery(id+"F14.wireOp",EDGE,"E7.left"),sQuery(id+"F14.wireOp",EDGE,"E7.right")])],"isStart":false})]}),makeQuery(id+"F51.opExtrude","CAP_FACE",FACE,{"disambiguationData":[OSD([sQuery(id+"F50.wireOp",EDGE,"E66.bottom"),sQuery(id+"F50.wireOp",EDGE,"E66.top"),sQuery(id+"F50.wireOp",EDGE,"E66.left"),sQuery(id+"F50.wireOp",EDGE,"E66.right")])],"isStart":false})]}),makeQuery(id+"F53.opExtrude","CAP_FACE",FACE,{"disambiguationData":[OSD([sQuery(id+"F52.wireOp",EDGE,"E67.bottom"),sQuery(id+"F52.wireOp",EDGE,"E67.top"),sQuery(id+"F52.wireOp",EDGE,"E67.left"),sQuery(id+"F52.wireOp",EDGE,"E67.right")])],"isStart":false})]}),makeQuery(id+"F55.opExtrude","CAP_FACE",FACE,{"disambiguationData":[OSD([sQuery(id+"F54.wireOp",EDGE,"E68.bottom"),sQuery(id+"F54.wireOp",EDGE,"E68.top"),sQuery(id+"F54.wireOp",EDGE,"E68.left"),sQuery(id+"F54.wireOp",EDGE,"E68.right")])],"isStart":false})]}),makeQuery(id+"F57.opExtrude","CAP_FACE",FACE,{"disambiguationData":[OSD([sQuery(id+"F56.wireOp",EDGE,"E69.bottom"),sQuery(id+"F56.wireOp",EDGE,"E69.top"),sQuery(id+"F56.wireOp",EDGE,"E69.left"),sQuery(id+"F56.wireOp",EDGE,"E69.right")])],"isStart":false})]}),makeQuery(id+"F59.opExtrude","CAP_FACE",FACE,{"disambiguationData":[OSD([sQuery(id+"F58.wireOp",EDGE,"E70.bottom"),sQuery(id+"F58.wireOp",EDGE,"E70.top"),sQuery(id+"F58.wireOp",EDGE,"E70.left"),sQuery(id+"F58.wireOp",EDGE,"E70.right")])],"isStart":false})]}),makeQuery(id+"F61.opExtrude","CAP_FACE",FACE,{"disambiguationData":[OSD([sQuery(id+"F60.wireOp",EDGE,"E71.bottom"),sQuery(id+"F60.wireOp",EDGE,"E71.top"),sQuery(id+"F60.wireOp",EDGE,"E71.left"),sQuery(id+"F60.wireOp",EDGE,"E71.right")])],"isStart":false})]}),makeQuery(id+"F89.opExtrude","CAP_FACE",FACE,{"disambiguationData":[OSD([sQuery(id+"F88.wireOp",EDGE,"E94.bottom"),sQuery(id+"F88.wireOp",EDGE,"E94.top"),sQuery(id+"F88.wireOp",EDGE,"E94.left"),sQuery(id+"F88.wireOp",EDGE,"E94.right")])],"isStart":false})]}),makeQuery(id+"F93.opExtrude","CAP_FACE",FACE,{"disambiguationData":[OSD([sQuery(id+"F92.wireOp",EDGE,"E97.bottom"),sQuery(id+"F92.wireOp",EDGE,"E97.top"),sQuery(id+"F92.wireOp",EDGE,"E97.left"),sQuery(id+"F92.wireOp",EDGE,"E97.right")])],"isStart":false})]}),makeQuery(id+"F95.opExtrude","CAP_FACE",FACE,{"disambiguationData":[OSD([sQuery(id+"F94.wireOp",EDGE,"E98.bottom"),sQuery(id+"F94.wireOp",EDGE,"E98.top"),sQuery(id+"F94.wireOp",EDGE,"E98.left"),sQuery(id+"F94.wireOp",EDGE,"E98.right")])],"isStart":false}),makeQuery(id+"F95.opExtrude","CAP_FACE",FACE,{"disambiguationData":[OSD([sQuery(id+"F94.wireOp",EDGE,"E99.0.1.0"),sQuery(id+"F94.wireOp",EDGE,"E99.0.1.1"),sQuery(id+"F94.wireOp",EDGE,"E99.0.1.2"),sQuery(id+"F94.wireOp",EDGE,"E99.0.1.3")])],"isStart":false})]});
            var sketch = newSketch(context, id + "F98", { "sketchPlane" : qUnion([Q0])});
            skLineSegment(sketch, "E102.bottom", {"start": v(-5.2, 20.5) * mm, "end": v(-8.81, 20.5) * mm});
            skLineSegment(sketch, "E102.top", {"start": v(-5.2, 19.7) * mm, "end": v(-8.81, 19.7) * mm});
            skLineSegment(sketch, "E102.left", {"start": v(-5.2, 20.5) * mm, "end": v(-5.2, 19.7) * mm});
            skLineSegment(sketch, "E102.right", {"start": v(-8.81, 20.5) * mm, "end": v(-8.81, 19.7) * mm});
            skLineSegment(sketch, "E103.0.1.0", {"start": v(-5.2, 12.5) * mm, "end": v(-8.81, 12.5) * mm});
            skLineSegment(sketch, "E103.0.1.1", {"start": v(-5.2, 11.7) * mm, "end": v(-8.81, 11.7) * mm});
            skLineSegment(sketch, "E103.0.1.2", {"start": v(-5.2, 12.5) * mm, "end": v(-5.2, 11.7) * mm});
            skLineSegment(sketch, "E103.0.1.3", {"start": v(-8.81, 12.5) * mm, "end": v(-8.81, 11.7) * mm});
            skLineSegment(sketch, "E103.0.2.0", {"start": v(-5.2, 4.5) * mm, "end": v(-8.81, 4.5) * mm});
            skLineSegment(sketch, "E103.0.2.1", {"start": v(-5.2, 3.7) * mm, "end": v(-8.81, 3.7) * mm});
            skLineSegment(sketch, "E103.0.2.2", {"start": v(-5.2, 4.5) * mm, "end": v(-5.2, 3.7) * mm});
            skLineSegment(sketch, "E103.0.2.3", {"start": v(-8.81, 4.5) * mm, "end": v(-8.81, 3.7) * mm});
            skLineSegment(sketch, "E103.0.3.0", {"start": v(-5.2, -3.5) * mm, "end": v(-8.81, -3.5) * mm});
            skLineSegment(sketch, "E103.0.3.1", {"start": v(-5.2, -4.3) * mm, "end": v(-8.81, -4.3) * mm});
            skLineSegment(sketch, "E103.0.3.2", {"start": v(-5.2, -3.5) * mm, "end": v(-5.2, -4.3) * mm});
            skLineSegment(sketch, "E103.0.3.3", {"start": v(-8.81, -3.5) * mm, "end": v(-8.81, -4.3) * mm});
            skLineSegment(sketch, "E103.0.4.0", {"start": v(-5.2, -11.5) * mm, "end": v(-8.81, -11.5) * mm});
            skLineSegment(sketch, "E103.0.4.1", {"start": v(-5.2, -12.3) * mm, "end": v(-8.81, -12.3) * mm});
            skLineSegment(sketch, "E103.0.4.2", {"start": v(-5.2, -11.5) * mm, "end": v(-5.2, -12.3) * mm});
            skLineSegment(sketch, "E103.0.4.3", {"start": v(-8.81, -11.5) * mm, "end": v(-8.81, -12.3) * mm});
            skLineSegment(sketch, "E103.0.5.0", {"start": v(-5.2, -19.5) * mm, "end": v(-8.81, -19.5) * mm});
            skLineSegment(sketch, "E103.0.5.1", {"start": v(-5.2, -20.3) * mm, "end": v(-8.81, -20.3) * mm});
            skLineSegment(sketch, "E103.0.5.2", {"start": v(-5.2, -19.5) * mm, "end": v(-5.2, -20.3) * mm});
            skLineSegment(sketch, "E103.0.5.3", {"start": v(-8.81, -19.5) * mm, "end": v(-8.81, -20.3) * mm});
            skLineSegment(sketch, "E103.1.0.0", {"start": v(-15.2, 20.5) * mm, "end": v(-18.81, 20.5) * mm});
            skLineSegment(sketch, "E103.1.0.1", {"start": v(-15.2, 19.7) * mm, "end": v(-18.81, 19.7) * mm});
            skLineSegment(sketch, "E103.1.0.2", {"start": v(-15.2, 20.5) * mm, "end": v(-15.2, 19.7) * mm});
            skLineSegment(sketch, "E103.1.0.3", {"start": v(-18.81, 20.5) * mm, "end": v(-18.81, 19.7) * mm});
            skLineSegment(sketch, "E103.1.1.0", {"start": v(-15.2, 12.5) * mm, "end": v(-18.81, 12.5) * mm});
            skLineSegment(sketch, "E103.1.1.1", {"start": v(-15.2, 11.7) * mm, "end": v(-18.81, 11.7) * mm});
            skLineSegment(sketch, "E103.1.1.2", {"start": v(-15.2, 12.5) * mm, "end": v(-15.2, 11.7) * mm});
            skLineSegment(sketch, "E103.1.1.3", {"start": v(-18.81, 12.5) * mm, "end": v(-18.81, 11.7) * mm});
            skLineSegment(sketch, "E103.1.2.0", {"start": v(-15.2, 4.5) * mm, "end": v(-18.81, 4.5) * mm});
            skLineSegment(sketch, "E103.1.2.1", {"start": v(-15.2, 3.7) * mm, "end": v(-18.81, 3.7) * mm});
            skLineSegment(sketch, "E103.1.2.2", {"start": v(-15.2, 4.5) * mm, "end": v(-15.2, 3.7) * mm});
            skLineSegment(sketch, "E103.1.2.3", {"start": v(-18.81, 4.5) * mm, "end": v(-18.81, 3.7) * mm});
            skLineSegment(sketch, "E103.1.3.0", {"start": v(-15.2, -3.5) * mm, "end": v(-18.81, -3.5) * mm});
            skLineSegment(sketch, "E103.1.3.1", {"start": v(-15.2, -4.3) * mm, "end": v(-18.81, -4.3) * mm});
            skLineSegment(sketch, "E103.1.3.2", {"start": v(-15.2, -3.5) * mm, "end": v(-15.2, -4.3) * mm});
            skLineSegment(sketch, "E103.1.3.3", {"start": v(-18.81, -3.5) * mm, "end": v(-18.81, -4.3) * mm});
            skLineSegment(sketch, "E103.1.4.0", {"start": v(-15.2, -11.5) * mm, "end": v(-18.81, -11.5) * mm});
            skLineSegment(sketch, "E103.1.4.1", {"start": v(-15.2, -12.3) * mm, "end": v(-18.81, -12.3) * mm});
            skLineSegment(sketch, "E103.1.4.2", {"start": v(-15.2, -11.5) * mm, "end": v(-15.2, -12.3) * mm});
            skLineSegment(sketch, "E103.1.4.3", {"start": v(-18.81, -11.5) * mm, "end": v(-18.81, -12.3) * mm});
            skLineSegment(sketch, "E103.1.5.0", {"start": v(-15.2, -19.5) * mm, "end": v(-18.81, -19.5) * mm});
            skLineSegment(sketch, "E103.1.5.1", {"start": v(-15.2, -20.3) * mm, "end": v(-18.81, -20.3) * mm});
            skLineSegment(sketch, "E103.1.5.2", {"start": v(-15.2, -19.5) * mm, "end": v(-15.2, -20.3) * mm});
            skLineSegment(sketch, "E103.1.5.3", {"start": v(-18.81, -19.5) * mm, "end": v(-18.81, -20.3) * mm});
            skLineSegment(sketch, "E103.direction1", {"start": v(-8.81, 20.5) * mm, "end": v(-18.81, 20.5) * mm, "construction": true});
            skLineSegment(sketch, "E103.direction2", {"start": v(-8.81, 20.5) * mm, "end": v(-8.81, 12.5) * mm, "construction": true});
            skSolve(sketch);
        }
        {
            var Q0;
            Q0 = qSketchRegion(id + "F98", true);
            extrude(context, id + "F99", {"entities" : qUnion([Q0]), "operationType" : NewBodyOperationType.ADD, "depth" : 1.2 * mm});
        }
        {
            var Q0;
            {var subQ0=sQuery(id+"F12.wireOp",EDGE,"E6.left");var subQ2=sQuery(id+"F60.wireOp",EDGE,"E71.top");var subQ3=sQuery(id+"F58.wireOp",EDGE,"E70.right");var subQ4=sQuery(id+"F52.wireOp",EDGE,"E67.top");var subQ5=sQuery(id+"F14.wireOp",EDGE,"E7.right");var subQ6=sQuery(id+"F60.wireOp",EDGE,"E71.right");var subQ7=sQuery(id+"F14.wireOp",EDGE,"E7.top");var subQ8=sQuery(id+"F14.wireOp",EDGE,"E7.bottom");var subQ9=sQuery(id+"F58.wireOp",EDGE,"E70.bottom");var subQ10=sQuery(id+"F12.wireOp",EDGE,"E6.top");var subQ11=sQuery(id+"F50.wireOp",EDGE,"E66.right");var subQ12=sQuery(id+"F10.wireOp",EDGE,"E5.bottom");var subQ13=sQuery(id+"F12.wireOp",EDGE,"E6.right");var subQ14=sQuery(id+"F8.wireOp",EDGE,"E4.right");var subQ15=sQuery(id+"F60.wireOp",EDGE,"E71.left");var subQ16=sQuery(id+"F12.wireOp",EDGE,"E6.bottom");var subQ17=sQuery(id+"F8.wireOp",EDGE,"E4.left");var subQ18=sQuery(id+"F50.wireOp",EDGE,"E66.left");var subQ19=sQuery(id+"F52.wireOp",EDGE,"E67.bottom");var subQ20=sQuery(id+"F50.wireOp",EDGE,"E66.bottom");var subQ21=sQuery(id+"F54.wireOp",EDGE,"E68.left");var subQ22=sQuery(id+"F54.wireOp",EDGE,"E68.bottom");var subQ23=sQuery(id+"F56.wireOp",EDGE,"E69.right");var subQ24=sQuery(id+"F52.wireOp",EDGE,"E67.left");var subQ25=sQuery(id+"F10.wireOp",EDGE,"E5.top");var subQ26=sQuery(id+"F54.wireOp",EDGE,"E68.right");var subQ27=sQuery(id+"F56.wireOp",EDGE,"E69.top");var subQ28=sQuery(id+"F56.wireOp",EDGE,"E69.left");var subQ29=sQuery(id+"F58.wireOp",EDGE,"E70.top");Q0=makeQuery(id+"F99.boolean.opBoolean","SPLIT",FACE,{"disambiguationData":[TD([makeQuery(id+"F11.boolean.opBoolean","COPY",FACE,{"derivedFrom":makeQuery(id+"F11.opExtrude","SWEPT_FACE",FACE,{"disambiguationData":[OSD([subQ12])]})})])],"derivedFrom":makeQuery(id+"F95.boolean.opBoolean","MERGE",FACE,{"derivedFrom":[makeQuery(id+"F93.boolean.opBoolean","MERGE",FACE,{"derivedFrom":[makeQuery(id+"F89.boolean.opBoolean","MERGE",FACE,{"derivedFrom":[makeQuery(id+"F61.boolean.opBoolean","MERGE",FACE,{"derivedFrom":[makeQuery(id+"F59.boolean.opBoolean","MERGE",FACE,{"derivedFrom":[makeQuery(id+"F57.boolean.opBoolean","MERGE",FACE,{"derivedFrom":[makeQuery(id+"F55.boolean.opBoolean","MERGE",FACE,{"derivedFrom":[makeQuery(id+"F53.boolean.opBoolean","MERGE",FACE,{"derivedFrom":[makeQuery(id+"F51.boolean.opBoolean","MERGE",FACE,{"derivedFrom":[makeQuery(id+"F15.boolean.opBoolean","MERGE",FACE,{"derivedFrom":[makeQuery(id+"F13.boolean.opBoolean","MERGE",FACE,{"derivedFrom":[makeQuery(id+"F11.boolean.opBoolean","MERGE",FACE,{"derivedFrom":[makeQuery(id+"F9.boolean.opBoolean","COPY",FACE,{"derivedFrom":makeQuery(id+"F9.opExtrude","CAP_FACE",FACE,{"disambiguationData":[OSD([sQuery(id+"F8.wireOp",EDGE,"E4.bottom"),sQuery(id+"F8.wireOp",EDGE,"E4.top"),subQ17,subQ14])],"isStart":false})}),makeQuery(id+"F11.opExtrude","CAP_FACE",FACE,{"disambiguationData":[OSD([subQ12,subQ25,sQuery(id+"F10.wireOp",EDGE,"E5.left"),sQuery(id+"F10.wireOp",EDGE,"E5.right")])],"isStart":false})]}),makeQuery(id+"F13.opExtrude","CAP_FACE",FACE,{"disambiguationData":[OSD([subQ16,subQ10,subQ0,subQ13])],"isStart":false})]}),makeQuery(id+"F15.opExtrude","CAP_FACE",FACE,{"disambiguationData":[OSD([subQ8,subQ7,sQuery(id+"F14.wireOp",EDGE,"E7.left"),subQ5])],"isStart":false})]}),makeQuery(id+"F51.opExtrude","CAP_FACE",FACE,{"disambiguationData":[OSD([subQ20,sQuery(id+"F50.wireOp",EDGE,"E66.top"),subQ18,subQ11])],"isStart":false})]}),makeQuery(id+"F53.opExtrude","CAP_FACE",FACE,{"disambiguationData":[OSD([subQ19,subQ4,subQ24,sQuery(id+"F52.wireOp",EDGE,"E67.right")])],"isStart":false})]}),makeQuery(id+"F55.opExtrude","CAP_FACE",FACE,{"disambiguationData":[OSD([subQ22,sQuery(id+"F54.wireOp",EDGE,"E68.top"),subQ21,subQ26])],"isStart":false})]}),makeQuery(id+"F57.opExtrude","CAP_FACE",FACE,{"disambiguationData":[OSD([sQuery(id+"F56.wireOp",EDGE,"E69.bottom"),subQ27,subQ28,subQ23])],"isStart":false})]}),makeQuery(id+"F59.opExtrude","CAP_FACE",FACE,{"disambiguationData":[OSD([subQ9,subQ29,sQuery(id+"F58.wireOp",EDGE,"E70.left"),subQ3])],"isStart":false})]}),makeQuery(id+"F61.opExtrude","CAP_FACE",FACE,{"disambiguationData":[OSD([sQuery(id+"F60.wireOp",EDGE,"E71.bottom"),subQ2,subQ15,subQ6])],"isStart":false})]}),makeQuery(id+"F89.opExtrude","CAP_FACE",FACE,{"disambiguationData":[OSD([sQuery(id+"F88.wireOp",EDGE,"E94.bottom"),sQuery(id+"F88.wireOp",EDGE,"E94.top"),sQuery(id+"F88.wireOp",EDGE,"E94.left"),sQuery(id+"F88.wireOp",EDGE,"E94.right")])],"isStart":false})]}),makeQuery(id+"F93.opExtrude","CAP_FACE",FACE,{"disambiguationData":[OSD([sQuery(id+"F92.wireOp",EDGE,"E97.bottom"),sQuery(id+"F92.wireOp",EDGE,"E97.top"),sQuery(id+"F92.wireOp",EDGE,"E97.left"),sQuery(id+"F92.wireOp",EDGE,"E97.right")])],"isStart":false})]}),makeQuery(id+"F95.opExtrude","CAP_FACE",FACE,{"disambiguationData":[OSD([sQuery(id+"F94.wireOp",EDGE,"E98.bottom"),sQuery(id+"F94.wireOp",EDGE,"E98.top"),sQuery(id+"F94.wireOp",EDGE,"E98.left"),sQuery(id+"F94.wireOp",EDGE,"E98.right")])],"isStart":false}),makeQuery(id+"F95.opExtrude","CAP_FACE",FACE,{"disambiguationData":[OSD([sQuery(id+"F94.wireOp",EDGE,"E99.0.1.0"),sQuery(id+"F94.wireOp",EDGE,"E99.0.1.1"),sQuery(id+"F94.wireOp",EDGE,"E99.0.1.2"),sQuery(id+"F94.wireOp",EDGE,"E99.0.1.3")])],"isStart":false})]})});}
            var sketch = newSketch(context, id + "F100", { "sketchPlane" : qUnion([Q0])});
            skLineSegment(sketch, "E104.bottom", {"start": v(15.17, 20.5) * mm, "end": v(18.8, 20.5) * mm});
            skLineSegment(sketch, "E104.top", {"start": v(15.17, 19.7) * mm, "end": v(18.8, 19.7) * mm});
            skLineSegment(sketch, "E104.left", {"start": v(15.17, 20.5) * mm, "end": v(15.17, 19.7) * mm});
            skLineSegment(sketch, "E104.right", {"start": v(18.8, 20.5) * mm, "end": v(18.8, 19.7) * mm});
            skLineSegment(sketch, "E105.0.1.0", {"start": v(15.17, 12.5) * mm, "end": v(18.8, 12.5) * mm});
            skLineSegment(sketch, "E105.0.1.1", {"start": v(18.8, 12.5) * mm, "end": v(18.8, 11.7) * mm});
            skLineSegment(sketch, "E105.0.1.2", {"start": v(15.17, 11.7) * mm, "end": v(18.8, 11.7) * mm});
            skLineSegment(sketch, "E105.0.1.3", {"start": v(15.17, 12.5) * mm, "end": v(15.17, 11.7) * mm});
            skLineSegment(sketch, "E105.0.2.0", {"start": v(15.17, 4.5) * mm, "end": v(18.8, 4.5) * mm});
            skLineSegment(sketch, "E105.0.2.1", {"start": v(18.8, 4.5) * mm, "end": v(18.8, 3.7) * mm});
            skLineSegment(sketch, "E105.0.2.2", {"start": v(15.17, 3.7) * mm, "end": v(18.8, 3.7) * mm});
            skLineSegment(sketch, "E105.0.2.3", {"start": v(15.17, 4.5) * mm, "end": v(15.17, 3.7) * mm});
            skLineSegment(sketch, "E105.0.3.0", {"start": v(15.17, -3.5) * mm, "end": v(18.8, -3.5) * mm});
            skLineSegment(sketch, "E105.0.3.1", {"start": v(18.8, -3.5) * mm, "end": v(18.8, -4.3) * mm});
            skLineSegment(sketch, "E105.0.3.2", {"start": v(15.17, -4.3) * mm, "end": v(18.8, -4.3) * mm});
            skLineSegment(sketch, "E105.0.3.3", {"start": v(15.17, -3.5) * mm, "end": v(15.17, -4.3) * mm});
            skLineSegment(sketch, "E105.0.4.0", {"start": v(15.17, -11.5) * mm, "end": v(18.8, -11.5) * mm});
            skLineSegment(sketch, "E105.0.4.1", {"start": v(18.8, -11.5) * mm, "end": v(18.8, -12.3) * mm});
            skLineSegment(sketch, "E105.0.4.2", {"start": v(15.17, -12.3) * mm, "end": v(18.8, -12.3) * mm});
            skLineSegment(sketch, "E105.0.4.3", {"start": v(15.17, -11.5) * mm, "end": v(15.17, -12.3) * mm});
            skLineSegment(sketch, "E105.0.5.0", {"start": v(15.17, -19.5) * mm, "end": v(18.8, -19.5) * mm});
            skLineSegment(sketch, "E105.0.5.1", {"start": v(18.8, -19.5) * mm, "end": v(18.8, -20.3) * mm});
            skLineSegment(sketch, "E105.0.5.2", {"start": v(15.17, -20.3) * mm, "end": v(18.8, -20.3) * mm});
            skLineSegment(sketch, "E105.0.5.3", {"start": v(15.17, -19.5) * mm, "end": v(15.17, -20.3) * mm});
            skLineSegment(sketch, "E105.1.0.0", {"start": v(5.17, 20.5) * mm, "end": v(8.8, 20.5) * mm});
            skLineSegment(sketch, "E105.1.0.1", {"start": v(8.8, 20.5) * mm, "end": v(8.8, 19.7) * mm});
            skLineSegment(sketch, "E105.1.0.2", {"start": v(5.17, 19.7) * mm, "end": v(8.8, 19.7) * mm});
            skLineSegment(sketch, "E105.1.0.3", {"start": v(5.17, 20.5) * mm, "end": v(5.17, 19.7) * mm});
            skLineSegment(sketch, "E105.1.1.0", {"start": v(5.17, 12.5) * mm, "end": v(8.8, 12.5) * mm});
            skLineSegment(sketch, "E105.1.1.1", {"start": v(8.8, 12.5) * mm, "end": v(8.8, 11.7) * mm});
            skLineSegment(sketch, "E105.1.1.2", {"start": v(5.17, 11.7) * mm, "end": v(8.8, 11.7) * mm});
            skLineSegment(sketch, "E105.1.1.3", {"start": v(5.17, 12.5) * mm, "end": v(5.17, 11.7) * mm});
            skLineSegment(sketch, "E105.1.2.0", {"start": v(5.17, 4.5) * mm, "end": v(8.8, 4.5) * mm});
            skLineSegment(sketch, "E105.1.2.1", {"start": v(8.8, 4.5) * mm, "end": v(8.8, 3.7) * mm});
            skLineSegment(sketch, "E105.1.2.2", {"start": v(5.17, 3.7) * mm, "end": v(8.8, 3.7) * mm});
            skLineSegment(sketch, "E105.1.2.3", {"start": v(5.17, 4.5) * mm, "end": v(5.17, 3.7) * mm});
            skLineSegment(sketch, "E105.1.3.0", {"start": v(5.17, -3.5) * mm, "end": v(8.8, -3.5) * mm});
            skLineSegment(sketch, "E105.1.3.1", {"start": v(8.8, -3.5) * mm, "end": v(8.8, -4.3) * mm});
            skLineSegment(sketch, "E105.1.3.2", {"start": v(5.17, -4.3) * mm, "end": v(8.8, -4.3) * mm});
            skLineSegment(sketch, "E105.1.3.3", {"start": v(5.17, -3.5) * mm, "end": v(5.17, -4.3) * mm});
            skLineSegment(sketch, "E105.1.4.0", {"start": v(5.17, -11.5) * mm, "end": v(8.8, -11.5) * mm});
            skLineSegment(sketch, "E105.1.4.1", {"start": v(8.8, -11.5) * mm, "end": v(8.8, -12.3) * mm});
            skLineSegment(sketch, "E105.1.4.2", {"start": v(5.17, -12.3) * mm, "end": v(8.8, -12.3) * mm});
            skLineSegment(sketch, "E105.1.4.3", {"start": v(5.17, -11.5) * mm, "end": v(5.17, -12.3) * mm});
            skLineSegment(sketch, "E105.1.5.0", {"start": v(5.17, -19.5) * mm, "end": v(8.8, -19.5) * mm});
            skLineSegment(sketch, "E105.1.5.1", {"start": v(8.8, -19.5) * mm, "end": v(8.8, -20.3) * mm});
            skLineSegment(sketch, "E105.1.5.2", {"start": v(5.17, -20.3) * mm, "end": v(8.8, -20.3) * mm});
            skLineSegment(sketch, "E105.1.5.3", {"start": v(5.17, -19.5) * mm, "end": v(5.17, -20.3) * mm});
            skLineSegment(sketch, "E105.direction1", {"start": v(15.17, 20.5) * mm, "end": v(5.17, 20.5) * mm, "construction": true});
            skLineSegment(sketch, "E105.direction2", {"start": v(15.17, 20.5) * mm, "end": v(15.17, 12.5) * mm, "construction": true});
            skSolve(sketch);
        }
        {
            var Q0;
            Q0 = qSketchRegion(id + "F100", true);
            extrude(context, id + "F101", {"entities" : qUnion([Q0]), "operationType" : NewBodyOperationType.ADD, "depth" : 1.2 * mm});
        }
        {
            var Q0;
            {var subQ0=sQuery(id+"F100.wireOp",EDGE,"E105.0.2.2");var subQ1=sQuery(id+"F100.wireOp",EDGE,"E105.0.2.0");Q0=makeQuery(id+"F101.boolean.opBoolean","SPLIT",FACE,{"disambiguationData":[TD([makeQuery(id+"F71.opExtrude","SWEPT_FACE",FACE,{"disambiguationData":[OSD([sQuery(id+"F70.wireOp",EDGE,"E80.1.2.0")])]})])],"derivedFrom":makeQuery(id+"F101.opExtrude","CAP_FACE",FACE,{"disambiguationData":[OSD([subQ1,sQuery(id+"F100.wireOp",EDGE,"E105.0.2.1"),subQ0,sQuery(id+"F100.wireOp",EDGE,"E105.0.2.3")])],"isStart":false})});}
            var sketch = newSketch(context, id + "F102", { "sketchPlane" : qUnion([Q0])});
            skLineSegment(sketch, "E106.bottom", {"start": v(15.17, 4.5) * mm, "end": v(16.76, 4.5) * mm});
            skLineSegment(sketch, "E106.top", {"start": v(15.17, 3.7) * mm, "end": v(16.76, 3.7) * mm});
            skLineSegment(sketch, "E106.left", {"start": v(15.17, 4.5) * mm, "end": v(15.17, 3.7) * mm});
            skLineSegment(sketch, "E106.right", {"start": v(16.76, 4.5) * mm, "end": v(16.76, 3.7) * mm});
            skLineSegment(sketch, "E107.bottom", {"start": v(17.69, 4.5) * mm, "end": v(18.93, 4.5) * mm});
            skLineSegment(sketch, "E107.top", {"start": v(17.69, 3.7) * mm, "end": v(18.93, 3.7) * mm});
            skLineSegment(sketch, "E107.left", {"start": v(17.69, 4.5) * mm, "end": v(17.69, 3.7) * mm});
            skLineSegment(sketch, "E107.right", {"start": v(18.93, 4.5) * mm, "end": v(18.93, 3.7) * mm});
            skSolve(sketch);
        }
        {
            var Q0;
            Q0 = qSketchRegion(id + "F102", true);
            extrude(context, id + "F103", {"entities" : qUnion([Q0]), "operationType" : NewBodyOperationType.REMOVE, "oppositeDirection" : true, "depth" : 1.2 * mm});
        }
    });
